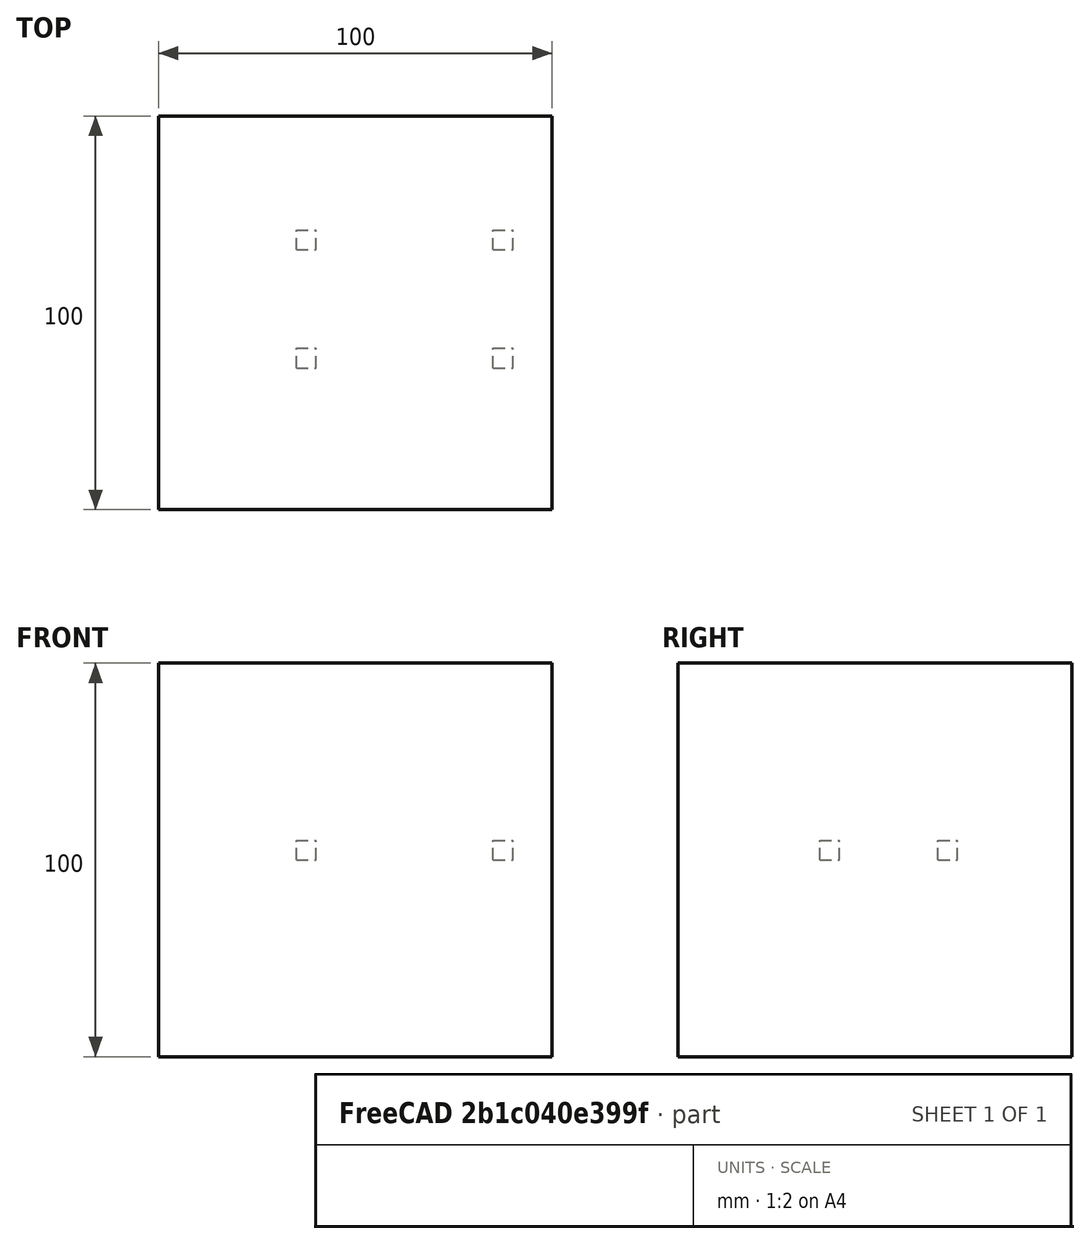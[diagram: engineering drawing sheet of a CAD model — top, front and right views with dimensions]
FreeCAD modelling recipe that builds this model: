
FCSTD DOCUMENT  (FreeCAD 0.19RUnknown)
Label: arrayTest-3
License: All rights reserved
LicenseURL: http://en.wikipedia.org/wiki/All_rights_reserved
objects: App::DocumentObjectGroupPython×1248, Part::FeaturePython×2, App::Part×2, Part::Box×1
note: 3 computed .brp shape members not serialized (recipe doc carries the construction recipe); baked Part::Feature solids carry a one-line shape summary decoded from their .brp

FEATURE [App::DocumentObjectGroupPython] HALFPI  # scripted group (container) (typed FeaturePython)
  name = HALFPI
  value = pi/2.
FEATURE [App::DocumentObjectGroupPython] PI  # scripted group (container) (typed FeaturePython)
  name = PI
  value = 1.*pi
FEATURE [App::DocumentObjectGroupPython] TWOPI  # scripted group (container) (typed FeaturePython)
  name = TWOPI
  value = 2.*pi
FEATURE [App::DocumentObjectGroupPython] Constants  # scripted group (container) (typed FeaturePython)
  Group = -> [HALFPI,PI,TWOPI]
FEATURE [App::DocumentObjectGroupPython] Variables  # scripted group (container) (typed FeaturePython)
FEATURE [App::DocumentObjectGroupPython] Quantities  # scripted group (container) (typed FeaturePython)
FEATURE [App::DocumentObjectGroupPython] Isotopes  # scripted group (container) (typed FeaturePython)
FEATURE [App::DocumentObjectGroupPython] Elements  # scripted group (container) (typed FeaturePython)
FEATURE [App::DocumentObjectGroupPython] G4Isotopes  # scripted group (container) (typed FeaturePython)
FEATURE [App::DocumentObjectGroupPython] H_element  # scripted group (container) (typed FeaturePython)
  Z = 1
  atom_value = 1.008
  formula = H
  name = H_element
FEATURE [App::DocumentObjectGroupPython] He_element  # scripted group (container) (typed FeaturePython)
  Z = 2
  atom_value = 4.0026
  formula = He
  name = He_element
FEATURE [App::DocumentObjectGroupPython] Li_element  # scripted group (container) (typed FeaturePython)
  Z = 3
  atom_value = 6.94
  formula = Li
  name = Li_element
FEATURE [App::DocumentObjectGroupPython] Be_element  # scripted group (container) (typed FeaturePython)
  Z = 4
  atom_value = 9.01218
  formula = Be
  name = Be_element
FEATURE [App::DocumentObjectGroupPython] B_element  # scripted group (container) (typed FeaturePython)
  Z = 5
  atom_value = 10.81
  formula = B
  name = B_element
FEATURE [App::DocumentObjectGroupPython] C_element  # scripted group (container) (typed FeaturePython)
  Z = 6
  atom_value = 12.011
  formula = C
  name = C_element
FEATURE [App::DocumentObjectGroupPython] N_element  # scripted group (container) (typed FeaturePython)
  Z = 7
  atom_value = 14.007
  formula = N
  name = N_element
FEATURE [App::DocumentObjectGroupPython] O_element  # scripted group (container) (typed FeaturePython)
  Z = 8
  atom_value = 15.999
  formula = O
  name = O_element
FEATURE [App::DocumentObjectGroupPython] F_element  # scripted group (container) (typed FeaturePython)
  Z = 9
  atom_value = 18.9984
  formula = F
  name = F_element
FEATURE [App::DocumentObjectGroupPython] Ne_element  # scripted group (container) (typed FeaturePython)
  Z = 10
  atom_value = 20.1797
  formula = Ne
  name = Ne_element
FEATURE [App::DocumentObjectGroupPython] Na_element  # scripted group (container) (typed FeaturePython)
  Z = 11
  atom_value = 22.9898
  formula = Na
  name = Na_element
FEATURE [App::DocumentObjectGroupPython] Mg_element  # scripted group (container) (typed FeaturePython)
  Z = 12
  atom_value = 24.305
  formula = Mg
  name = Mg_element
FEATURE [App::DocumentObjectGroupPython] Al_element  # scripted group (container) (typed FeaturePython)
  Z = 13
  atom_value = 26.9815
  formula = Al
  name = Al_element
FEATURE [App::DocumentObjectGroupPython] Si_element  # scripted group (container) (typed FeaturePython)
  Z = 14
  atom_value = 28.085
  formula = Si
  name = Si_element
FEATURE [App::DocumentObjectGroupPython] P_element  # scripted group (container) (typed FeaturePython)
  Z = 15
  atom_value = 30.9738
  formula = P
  name = P_element
FEATURE [App::DocumentObjectGroupPython] S_element  # scripted group (container) (typed FeaturePython)
  Z = 16
  atom_value = 32.06
  formula = S
  name = S_element
FEATURE [App::DocumentObjectGroupPython] Cl_element  # scripted group (container) (typed FeaturePython)
  Z = 17
  atom_value = 35.45
  formula = Cl
  name = Cl_element
FEATURE [App::DocumentObjectGroupPython] Ar_element  # scripted group (container) (typed FeaturePython)
  Z = 18
  atom_value = 39.95
  formula = Ar
  name = Ar_element
FEATURE [App::DocumentObjectGroupPython] K_element  # scripted group (container) (typed FeaturePython)
  Z = 19
  atom_value = 39.0983
  formula = K
  name = K_element
FEATURE [App::DocumentObjectGroupPython] Ca_element  # scripted group (container) (typed FeaturePython)
  Z = 20
  atom_value = 40.078
  formula = Ca
  name = Ca_element
FEATURE [App::DocumentObjectGroupPython] Sc_element  # scripted group (container) (typed FeaturePython)
  Z = 21
  atom_value = 44.9559
  formula = Sc
  name = Sc_element
FEATURE [App::DocumentObjectGroupPython] Ti_element  # scripted group (container) (typed FeaturePython)
  Z = 22
  atom_value = 47.867
  formula = Ti
  name = Ti_element
FEATURE [App::DocumentObjectGroupPython] V_element  # scripted group (container) (typed FeaturePython)
  Z = 23
  atom_value = 50.9415
  formula = V
  name = V_element
FEATURE [App::DocumentObjectGroupPython] Cr_element  # scripted group (container) (typed FeaturePython)
  Z = 24
  atom_value = 51.9961
  formula = Cr
  name = Cr_element
FEATURE [App::DocumentObjectGroupPython] Mn_element  # scripted group (container) (typed FeaturePython)
  Z = 25
  atom_value = 54.938
  formula = Mn
  name = Mn_element
FEATURE [App::DocumentObjectGroupPython] Fe_element  # scripted group (container) (typed FeaturePython)
  Z = 26
  atom_value = 55.845
  formula = Fe
  name = Fe_element
FEATURE [App::DocumentObjectGroupPython] Co_element  # scripted group (container) (typed FeaturePython)
  Z = 27
  atom_value = 58.9332
  formula = Co
  name = Co_element
FEATURE [App::DocumentObjectGroupPython] Ni_element  # scripted group (container) (typed FeaturePython)
  Z = 28
  atom_value = 58.6934
  formula = Ni
  name = Ni_element
FEATURE [App::DocumentObjectGroupPython] Cu_element  # scripted group (container) (typed FeaturePython)
  Z = 29
  atom_value = 63.546
  formula = Cu
  name = Cu_element
FEATURE [App::DocumentObjectGroupPython] Zn_element  # scripted group (container) (typed FeaturePython)
  Z = 30
  atom_value = 65.38
  formula = Zn
  name = Zn_element
FEATURE [App::DocumentObjectGroupPython] Ga_element  # scripted group (container) (typed FeaturePython)
  Z = 31
  atom_value = 69.723
  formula = Ga
  name = Ga_element
FEATURE [App::DocumentObjectGroupPython] Ge_element  # scripted group (container) (typed FeaturePython)
  Z = 32
  atom_value = 72.63
  formula = Ge
  name = Ge_element
FEATURE [App::DocumentObjectGroupPython] As_element  # scripted group (container) (typed FeaturePython)
  Z = 33
  atom_value = 74.9216
  formula = As
  name = As_element
FEATURE [App::DocumentObjectGroupPython] Se_element  # scripted group (container) (typed FeaturePython)
  Z = 34
  atom_value = 78.971
  formula = Se
  name = Se_element
FEATURE [App::DocumentObjectGroupPython] Br_element  # scripted group (container) (typed FeaturePython)
  Z = 35
  atom_value = 79.904
  formula = Br
  name = Br_element
FEATURE [App::DocumentObjectGroupPython] Kr_element  # scripted group (container) (typed FeaturePython)
  Z = 36
  atom_value = 83.798
  formula = Kr
  name = Kr_element
FEATURE [App::DocumentObjectGroupPython] Rb_element  # scripted group (container) (typed FeaturePython)
  Z = 37
  atom_value = 85.4678
  formula = Rb
  name = Rb_element
FEATURE [App::DocumentObjectGroupPython] Sr_element  # scripted group (container) (typed FeaturePython)
  Z = 38
  atom_value = 87.62
  formula = Sr
  name = Sr_element
FEATURE [App::DocumentObjectGroupPython] Y_element  # scripted group (container) (typed FeaturePython)
  Z = 39
  atom_value = 88.9058
  formula = Y
  name = Y_element
FEATURE [App::DocumentObjectGroupPython] Zr_element  # scripted group (container) (typed FeaturePython)
  Z = 40
  atom_value = 91.224
  formula = Zr
  name = Zr_element
FEATURE [App::DocumentObjectGroupPython] Nb_element  # scripted group (container) (typed FeaturePython)
  Z = 41
  atom_value = 92.9064
  formula = Nb
  name = Nb_element
FEATURE [App::DocumentObjectGroupPython] Mo_element  # scripted group (container) (typed FeaturePython)
  Z = 42
  atom_value = 95.95
  formula = Mo
  name = Mo_element
FEATURE [App::DocumentObjectGroupPython] Tc_element  # scripted group (container) (typed FeaturePython)
  Z = 43
  atom_value = 97
  formula = Tc
  name = Tc_element
FEATURE [App::DocumentObjectGroupPython] Ru_element  # scripted group (container) (typed FeaturePython)
  Z = 44
  atom_value = 101.07
  formula = Ru
  name = Ru_element
FEATURE [App::DocumentObjectGroupPython] Rh_element  # scripted group (container) (typed FeaturePython)
  Z = 45
  atom_value = 102.905
  formula = Rh
  name = Rh_element
FEATURE [App::DocumentObjectGroupPython] Pd_element  # scripted group (container) (typed FeaturePython)
  Z = 46
  atom_value = 106.42
  formula = Pd
  name = Pd_element
FEATURE [App::DocumentObjectGroupPython] Ag_element  # scripted group (container) (typed FeaturePython)
  Z = 47
  atom_value = 107.868
  formula = Ag
  name = Ag_element
FEATURE [App::DocumentObjectGroupPython] Cd_element  # scripted group (container) (typed FeaturePython)
  Z = 48
  atom_value = 112.414
  formula = Cd
  name = Cd_element
FEATURE [App::DocumentObjectGroupPython] In_element  # scripted group (container) (typed FeaturePython)
  Z = 49
  atom_value = 114.818
  formula = In
  name = In_element
FEATURE [App::DocumentObjectGroupPython] Sn_element  # scripted group (container) (typed FeaturePython)
  Z = 50
  atom_value = 118.71
  formula = Sn
  name = Sn_element
FEATURE [App::DocumentObjectGroupPython] Sb_element  # scripted group (container) (typed FeaturePython)
  Z = 51
  atom_value = 121.76
  formula = Sb
  name = Sb_element
FEATURE [App::DocumentObjectGroupPython] Te_element  # scripted group (container) (typed FeaturePython)
  Z = 52
  atom_value = 127.6
  formula = Te
  name = Te_element
FEATURE [App::DocumentObjectGroupPython] I_element  # scripted group (container) (typed FeaturePython)
  Z = 53
  atom_value = 126.904
  formula = I
  name = I_element
FEATURE [App::DocumentObjectGroupPython] Xe_element  # scripted group (container) (typed FeaturePython)
  Z = 54
  atom_value = 131.293
  formula = Xe
  name = Xe_element
FEATURE [App::DocumentObjectGroupPython] Cs_element  # scripted group (container) (typed FeaturePython)
  Z = 55
  atom_value = 132.905
  formula = Cs
  name = Cs_element
FEATURE [App::DocumentObjectGroupPython] Ba_element  # scripted group (container) (typed FeaturePython)
  Z = 56
  atom_value = 137.327
  formula = Ba
  name = Ba_element
FEATURE [App::DocumentObjectGroupPython] La_element  # scripted group (container) (typed FeaturePython)
  Z = 57
  atom_value = 138.905
  formula = La
  name = La_element
FEATURE [App::DocumentObjectGroupPython] Ce_element  # scripted group (container) (typed FeaturePython)
  Z = 58
  atom_value = 140.116
  formula = Ce
  name = Ce_element
FEATURE [App::DocumentObjectGroupPython] Pr_element  # scripted group (container) (typed FeaturePython)
  Z = 59
  atom_value = 140.908
  formula = Pr
  name = Pr_element
FEATURE [App::DocumentObjectGroupPython] Nd_element  # scripted group (container) (typed FeaturePython)
  Z = 60
  atom_value = 144.242
  formula = Nd
  name = Nd_element
FEATURE [App::DocumentObjectGroupPython] Pm_element  # scripted group (container) (typed FeaturePython)
  Z = 61
  atom_value = 145
  formula = Pm
  name = Pm_element
FEATURE [App::DocumentObjectGroupPython] Sm_element  # scripted group (container) (typed FeaturePython)
  Z = 62
  atom_value = 150.36
  formula = Sm
  name = Sm_element
FEATURE [App::DocumentObjectGroupPython] Eu_element  # scripted group (container) (typed FeaturePython)
  Z = 63
  atom_value = 151.964
  formula = Eu
  name = Eu_element
FEATURE [App::DocumentObjectGroupPython] Gd_element  # scripted group (container) (typed FeaturePython)
  Z = 64
  atom_value = 157.25
  formula = Gd
  name = Gd_element
FEATURE [App::DocumentObjectGroupPython] Tb_element  # scripted group (container) (typed FeaturePython)
  Z = 65
  atom_value = 158.925
  formula = Tb
  name = Tb_element
FEATURE [App::DocumentObjectGroupPython] Dy_element  # scripted group (container) (typed FeaturePython)
  Z = 66
  atom_value = 162.5
  formula = Dy
  name = Dy_element
FEATURE [App::DocumentObjectGroupPython] Ho_element  # scripted group (container) (typed FeaturePython)
  Z = 67
  atom_value = 164.93
  formula = Ho
  name = Ho_element
FEATURE [App::DocumentObjectGroupPython] Er_element  # scripted group (container) (typed FeaturePython)
  Z = 68
  atom_value = 167.259
  formula = Er
  name = Er_element
FEATURE [App::DocumentObjectGroupPython] Tm_element  # scripted group (container) (typed FeaturePython)
  Z = 69
  atom_value = 168.934
  formula = Tm
  name = Tm_element
FEATURE [App::DocumentObjectGroupPython] Yb_element  # scripted group (container) (typed FeaturePython)
  Z = 70
  atom_value = 173.045
  formula = Yb
  name = Yb_element
FEATURE [App::DocumentObjectGroupPython] Lu_element  # scripted group (container) (typed FeaturePython)
  Z = 71
  atom_value = 174.967
  formula = Lu
  name = Lu_element
FEATURE [App::DocumentObjectGroupPython] Hf_element  # scripted group (container) (typed FeaturePython)
  Z = 72
  atom_value = 178.49
  formula = Hf
  name = Hf_element
FEATURE [App::DocumentObjectGroupPython] Ta_element  # scripted group (container) (typed FeaturePython)
  Z = 73
  atom_value = 180.948
  formula = Ta
  name = Ta_element
FEATURE [App::DocumentObjectGroupPython] W_element  # scripted group (container) (typed FeaturePython)
  Z = 74
  atom_value = 183.84
  formula = W
  name = W_element
FEATURE [App::DocumentObjectGroupPython] Re_element  # scripted group (container) (typed FeaturePython)
  Z = 75
  atom_value = 186.207
  formula = Re
  name = Re_element
FEATURE [App::DocumentObjectGroupPython] Os_element  # scripted group (container) (typed FeaturePython)
  Z = 76
  atom_value = 190.23
  formula = Os
  name = Os_element
FEATURE [App::DocumentObjectGroupPython] Ir_element  # scripted group (container) (typed FeaturePython)
  Z = 77
  atom_value = 192.217
  formula = Ir
  name = Ir_element
FEATURE [App::DocumentObjectGroupPython] Pt_element  # scripted group (container) (typed FeaturePython)
  Z = 78
  atom_value = 195.084
  formula = Pt
  name = Pt_element
FEATURE [App::DocumentObjectGroupPython] Au_element  # scripted group (container) (typed FeaturePython)
  Z = 79
  atom_value = 196.967
  formula = Au
  name = Au_element
FEATURE [App::DocumentObjectGroupPython] Hg_element  # scripted group (container) (typed FeaturePython)
  Z = 80
  atom_value = 200.592
  formula = Hg
  name = Hg_element
FEATURE [App::DocumentObjectGroupPython] Tl_element  # scripted group (container) (typed FeaturePython)
  Z = 81
  atom_value = 204.38
  formula = Tl
  name = Tl_element
FEATURE [App::DocumentObjectGroupPython] Pb_element  # scripted group (container) (typed FeaturePython)
  Z = 82
  atom_value = 207.2
  formula = Pb
  name = Pb_element
FEATURE [App::DocumentObjectGroupPython] Bi_element  # scripted group (container) (typed FeaturePython)
  Z = 83
  atom_value = 208.98
  formula = Bi
  name = Bi_element
FEATURE [App::DocumentObjectGroupPython] Po_element  # scripted group (container) (typed FeaturePython)
  Z = 84
  atom_value = 209
  formula = Po
  name = Po_element
FEATURE [App::DocumentObjectGroupPython] At_element  # scripted group (container) (typed FeaturePython)
  Z = 85
  atom_value = 210
  formula = At
  name = At_element
FEATURE [App::DocumentObjectGroupPython] Rn_element  # scripted group (container) (typed FeaturePython)
  Z = 86
  atom_value = 222
  formula = Rn
  name = Rn_element
FEATURE [App::DocumentObjectGroupPython] Fr_element  # scripted group (container) (typed FeaturePython)
  Z = 87
  atom_value = 223
  formula = Fr
  name = Fr_element
FEATURE [App::DocumentObjectGroupPython] Ra_element  # scripted group (container) (typed FeaturePython)
  Z = 88
  atom_value = 226
  formula = Ra
  name = Ra_element
FEATURE [App::DocumentObjectGroupPython] Ac_element  # scripted group (container) (typed FeaturePython)
  Z = 89
  atom_value = 227
  formula = Ac
  name = Ac_element
FEATURE [App::DocumentObjectGroupPython] Th_element  # scripted group (container) (typed FeaturePython)
  Z = 90
  atom_value = 232.038
  formula = Th
  name = Th_element
FEATURE [App::DocumentObjectGroupPython] Pa_element  # scripted group (container) (typed FeaturePython)
  Z = 91
  atom_value = 231.036
  formula = Pa
  name = Pa_element
FEATURE [App::DocumentObjectGroupPython] U_element  # scripted group (container) (typed FeaturePython)
  Z = 92
  atom_value = 238.029
  formula = U
  name = U_element
FEATURE [App::DocumentObjectGroupPython] Np_element  # scripted group (container) (typed FeaturePython)
  Z = 93
  atom_value = 237
  formula = Np
  name = Np_element
FEATURE [App::DocumentObjectGroupPython] Pu_element  # scripted group (container) (typed FeaturePython)
  Z = 94
  atom_value = 244
  formula = Pu
  name = Pu_element
FEATURE [App::DocumentObjectGroupPython] Am_element  # scripted group (container) (typed FeaturePython)
  Z = 95
  atom_value = 243
  formula = Am
  name = Am_element
FEATURE [App::DocumentObjectGroupPython] Cm_element  # scripted group (container) (typed FeaturePython)
  Z = 96
  atom_value = 247
  formula = Cm
  name = Cm_element
FEATURE [App::DocumentObjectGroupPython] Bk_element  # scripted group (container) (typed FeaturePython)
  Z = 97
  atom_value = 247
  formula = Bk
  name = Bk_element
FEATURE [App::DocumentObjectGroupPython] Cf_element  # scripted group (container) (typed FeaturePython)
  Z = 98
  atom_value = 251
  formula = Cf
  name = Cf_element
FEATURE [App::DocumentObjectGroupPython] G4Elements  # scripted group (container) (typed FeaturePython)
  Group = -> [H_element,He_element,Li_element,Be_element,B_element,C_element,N_element,O_element,F_element,Ne_element,Na_element,Mg_element,Al_element,Si_element,P_element,S_element,Cl_element,Ar_element,K_element,Ca_element,Sc_element,Ti_element,V_element,Cr_element,Mn_element,Fe_element,Co_element,Ni_element,Cu_element,Zn_element,Ga_element,Ge_element,As_element,Se_element,Br_element,Kr_element,Rb_element,+61 more]
FEATURE [App::DocumentObjectGroupPython] H_element001  label="H_element : 0.101"  # scripted group (container) (typed FeaturePython)
  n = 0.101327
FEATURE [App::DocumentObjectGroupPython] C_element001  label="C_element : 0.775"  # scripted group (container) (typed FeaturePython)
  n = 0.7755
FEATURE [App::DocumentObjectGroupPython] N_element001  label="N_element : 0.035"  # scripted group (container) (typed FeaturePython)
  n = 0.035057
FEATURE [App::DocumentObjectGroupPython] O_element001  label="O_element : 0.052"  # scripted group (container) (typed FeaturePython)
  n = 0.0523159
FEATURE [App::DocumentObjectGroupPython] F_element001  label="F_element : 0.017"  # scripted group (container) (typed FeaturePython)
  n = 0.017422
FEATURE [App::DocumentObjectGroupPython] Ca_element001  label="Ca_element : 0.018"  # scripted group (container) (typed FeaturePython)
  n = 0.018378
FEATURE [App::DocumentObjectGroupPython] G4_A_150_TISSUE  label="G4_A-150_TISSUE"  # scripted group (container) (typed FeaturePython)
  Dunit = g/cm3
  Dvalue = 1.127
  Group = -> [H_element001,C_element001,N_element001,O_element001,F_element001,Ca_element001]
  conduct = 2
  density = 1
  expand = 3
  formula = G4_A-150_TISSUE
  name = G4_A-150_TISSUE
  specific = 4
FEATURE [App::DocumentObjectGroupPython] C_element002  label="C_element : 3"  # scripted group (container) (typed FeaturePython)
  n = 3
  ref = C_element
FEATURE [App::DocumentObjectGroupPython] H_element002  label="H_element : 6"  # scripted group (container) (typed FeaturePython)
  n = 6
  ref = H_element
FEATURE [App::DocumentObjectGroupPython] O_element002  label="O_element : 1"  # scripted group (container) (typed FeaturePython)
  n = 1
  ref = O_element
FEATURE [App::DocumentObjectGroupPython] G4_ACETONE  # scripted group (container) (typed FeaturePython)
  Dunit = g/cm3
  Dvalue = 0.7899
  Group = -> [C_element002,H_element002,O_element002]
  conduct = 2
  density = 1
  expand = 3
  formula = G4_ACETONE
  name = G4_ACETONE
  specific = 4
FEATURE [App::DocumentObjectGroupPython] C_element003  label="C_element : 2"  # scripted group (container) (typed FeaturePython)
  n = 2
  ref = C_element
FEATURE [App::DocumentObjectGroupPython] H_element003  label="H_element : 2"  # scripted group (container) (typed FeaturePython)
  n = 2
  ref = H_element
FEATURE [App::DocumentObjectGroupPython] G4_ACETYLENE  # scripted group (container) (typed FeaturePython)
  Dunit = g/cm3
  Dvalue = 0.0010967
  Group = -> [C_element003,H_element003]
  conduct = 2
  density = 1
  expand = 3
  formula = G4_ACETYLENE
  name = G4_ACETYLENE
  specific = 4
FEATURE [App::DocumentObjectGroupPython] C_element004  label="C_element : 5"  # scripted group (container) (typed FeaturePython)
  n = 5
  ref = C_element
FEATURE [App::DocumentObjectGroupPython] H_element004  label="H_element : 5"  # scripted group (container) (typed FeaturePython)
  n = 5
  ref = H_element
FEATURE [App::DocumentObjectGroupPython] N_element002  label="N_element : 5"  # scripted group (container) (typed FeaturePython)
  n = 5
  ref = N_element
FEATURE [App::DocumentObjectGroupPython] G4_ADENINE  # scripted group (container) (typed FeaturePython)
  Dunit = g/cm3
  Dvalue = 1.6
  Group = -> [C_element004,H_element004,N_element002]
  conduct = 2
  density = 1
  expand = 3
  formula = G4_ADENINE
  name = G4_ADENINE
  specific = 4
FEATURE [App::DocumentObjectGroupPython] H_element005  label="H_element : 0.114"  # scripted group (container) (typed FeaturePython)
  n = 0.114
FEATURE [App::DocumentObjectGroupPython] C_element005  label="C_element : 0.598"  # scripted group (container) (typed FeaturePython)
  n = 0.598
FEATURE [App::DocumentObjectGroupPython] N_element003  label="N_element : 0.007"  # scripted group (container) (typed FeaturePython)
  n = 0.007
FEATURE [App::DocumentObjectGroupPython] O_element003  label="O_element : 0.278"  # scripted group (container) (typed FeaturePython)
  n = 0.278
FEATURE [App::DocumentObjectGroupPython] Na_element001  label="Na_element : 0.001"  # scripted group (container) (typed FeaturePython)
  n = 0.001
FEATURE [App::DocumentObjectGroupPython] S_element001  label="S_element : 0.001"  # scripted group (container) (typed FeaturePython)
  n = 0.001
FEATURE [App::DocumentObjectGroupPython] Cl_element001  label="Cl_element : 0.001"  # scripted group (container) (typed FeaturePython)
  n = 0.001
FEATURE [App::DocumentObjectGroupPython] G4_ADIPOSE_TISSUE_ICRP  # scripted group (container) (typed FeaturePython)
  Dunit = g/cm3
  Dvalue = 0.95
  Group = -> [H_element005,C_element005,N_element003,O_element003,Na_element001,S_element001,Cl_element001]
  conduct = 2
  density = 1
  expand = 3
  formula = G4_ADIPOSE_TISSUE_ICRP
  name = G4_ADIPOSE_TISSUE_ICRP
  specific = 4
FEATURE [App::DocumentObjectGroupPython] C_element006  label="C_element : 0.000"  # scripted group (container) (typed FeaturePython)
  n = 0.000124
FEATURE [App::DocumentObjectGroupPython] N_element004  label="N_element : 0.755"  # scripted group (container) (typed FeaturePython)
  n = 0.755268
FEATURE [App::DocumentObjectGroupPython] O_element004  label="O_element : 0.232"  # scripted group (container) (typed FeaturePython)
  n = 0.231781
FEATURE [App::DocumentObjectGroupPython] Ar_element001  label="Ar_element : 0.013"  # scripted group (container) (typed FeaturePython)
  n = 0.012827
FEATURE [App::DocumentObjectGroupPython] G4_AIR  # scripted group (container) (typed FeaturePython)
  Dunit = g/cm3
  Dvalue = 0.00120479
  Group = -> [C_element006,N_element004,O_element004,Ar_element001]
  conduct = 2
  density = 1
  expand = 3
  formula = G4_AIR
  name = G4_AIR
  specific = 4
FEATURE [App::DocumentObjectGroupPython] C_element007  label="C_element : 006"  # scripted group (container) (typed FeaturePython)
  n = 3
  ref = C_element
FEATURE [App::DocumentObjectGroupPython] H_element006  label="H_element : 7"  # scripted group (container) (typed FeaturePython)
  n = 7
  ref = H_element
FEATURE [App::DocumentObjectGroupPython] N_element005  label="N_element : 1"  # scripted group (container) (typed FeaturePython)
  n = 1
  ref = N_element
FEATURE [App::DocumentObjectGroupPython] O_element005  label="O_element : 2"  # scripted group (container) (typed FeaturePython)
  n = 2
  ref = O_element
FEATURE [App::DocumentObjectGroupPython] G4_ALANINE  # scripted group (container) (typed FeaturePython)
  Dunit = g/cm3
  Dvalue = 1.42
  Group = -> [C_element007,H_element006,N_element005,O_element005]
  conduct = 2
  density = 1
  expand = 3
  formula = G4_ALANINE
  name = G4_ALANINE
  specific = 4
FEATURE [App::DocumentObjectGroupPython] Al_element001  label="Al_element : 2"  # scripted group (container) (typed FeaturePython)
  n = 2
  ref = Al_element
FEATURE [App::DocumentObjectGroupPython] O_element006  label="O_element : 3"  # scripted group (container) (typed FeaturePython)
  n = 3
  ref = O_element
FEATURE [App::DocumentObjectGroupPython] G4_ALUMINUM_OXIDE  # scripted group (container) (typed FeaturePython)
  Dunit = g/cm3
  Dvalue = 3.97
  Group = -> [Al_element001,O_element006]
  conduct = 2
  density = 1
  expand = 3
  formula = G4_ALUMINUM_OXIDE
  name = G4_ALUMINUM_OXIDE
  specific = 4
FEATURE [App::DocumentObjectGroupPython] H_element007  label="H_element : 0.106"  # scripted group (container) (typed FeaturePython)
  n = 0.10593
FEATURE [App::DocumentObjectGroupPython] C_element008  label="C_element : 0.789"  # scripted group (container) (typed FeaturePython)
  n = 0.788974
FEATURE [App::DocumentObjectGroupPython] O_element007  label="O_element : 0.105"  # scripted group (container) (typed FeaturePython)
  n = 0.105096
FEATURE [App::DocumentObjectGroupPython] G4_AMBER  # scripted group (container) (typed FeaturePython)
  Dunit = g/cm3
  Dvalue = 1.1
  Group = -> [H_element007,C_element008,O_element007]
  conduct = 2
  density = 1
  expand = 3
  formula = G4_AMBER
  name = G4_AMBER
  specific = 4
FEATURE [App::DocumentObjectGroupPython] N_element006  label="N_element : 006"  # scripted group (container) (typed FeaturePython)
  n = 1
  ref = N_element
FEATURE [App::DocumentObjectGroupPython] H_element008  label="H_element : 3"  # scripted group (container) (typed FeaturePython)
  n = 3
  ref = H_element
FEATURE [App::DocumentObjectGroupPython] G4_AMMONIA  # scripted group (container) (typed FeaturePython)
  Dunit = g/cm3
  Dvalue = 0.000826019
  Group = -> [N_element006,H_element008]
  conduct = 2
  density = 1
  expand = 3
  formula = G4_AMMONIA
  name = G4_AMMONIA
  specific = 4
FEATURE [App::DocumentObjectGroupPython] C_element009  label="C_element : 6"  # scripted group (container) (typed FeaturePython)
  n = 6
  ref = C_element
FEATURE [App::DocumentObjectGroupPython] H_element009  label="H_element : 008"  # scripted group (container) (typed FeaturePython)
  n = 7
  ref = H_element
FEATURE [App::DocumentObjectGroupPython] N_element007  label="N_element : 007"  # scripted group (container) (typed FeaturePython)
  n = 1
  ref = N_element
FEATURE [App::DocumentObjectGroupPython] G4_ANILINE  # scripted group (container) (typed FeaturePython)
  Dunit = g/cm3
  Dvalue = 1.0235
  Group = -> [C_element009,H_element009,N_element007]
  conduct = 2
  density = 1
  expand = 3
  formula = G4_ANILINE
  name = G4_ANILINE
  specific = 4
FEATURE [App::DocumentObjectGroupPython] C_element010  label="C_element : 14"  # scripted group (container) (typed FeaturePython)
  n = 14
  ref = C_element
FEATURE [App::DocumentObjectGroupPython] H_element010  label="H_element : 10"  # scripted group (container) (typed FeaturePython)
  n = 10
  ref = H_element
FEATURE [App::DocumentObjectGroupPython] G4_ANTHRACENE  # scripted group (container) (typed FeaturePython)
  Dunit = g/cm3
  Dvalue = 1.283
  Group = -> [C_element010,H_element010]
  conduct = 2
  density = 1
  expand = 3
  formula = G4_ANTHRACENE
  name = G4_ANTHRACENE
  specific = 4
FEATURE [App::DocumentObjectGroupPython] H_element011  label="H_element : 0.065"  # scripted group (container) (typed FeaturePython)
  n = 0.0654709
FEATURE [App::DocumentObjectGroupPython] C_element011  label="C_element : 0.537"  # scripted group (container) (typed FeaturePython)
  n = 0.536944
FEATURE [App::DocumentObjectGroupPython] N_element008  label="N_element : 0.021"  # scripted group (container) (typed FeaturePython)
  n = 0.0215
FEATURE [App::DocumentObjectGroupPython] O_element008  label="O_element : 0.032"  # scripted group (container) (typed FeaturePython)
  n = 0.032085
FEATURE [App::DocumentObjectGroupPython] F_element002  label="F_element : 0.167"  # scripted group (container) (typed FeaturePython)
  n = 0.167411
FEATURE [App::DocumentObjectGroupPython] Ca_element002  label="Ca_element : 0.177"  # scripted group (container) (typed FeaturePython)
  n = 0.176589
FEATURE [App::DocumentObjectGroupPython] G4_B_100_BONE  label="G4_B-100_BONE"  # scripted group (container) (typed FeaturePython)
  Dunit = g/cm3
  Dvalue = 1.45
  Group = -> [H_element011,C_element011,N_element008,O_element008,F_element002,Ca_element002]
  conduct = 2
  density = 1
  expand = 3
  formula = G4_B-100_BONE
  name = G4_B-100_BONE
  specific = 4
FEATURE [App::DocumentObjectGroupPython] H_element012  label="H_element : 0.057"  # scripted group (container) (typed FeaturePython)
  n = 0.057441
FEATURE [App::DocumentObjectGroupPython] C_element012  label="C_element : 0.790"  # scripted group (container) (typed FeaturePython)
  n = 0.774591
FEATURE [App::DocumentObjectGroupPython] O_element009  label="O_element : 0.168"  # scripted group (container) (typed FeaturePython)
  n = 0.167968
FEATURE [App::DocumentObjectGroupPython] G4_BAKELITE  # scripted group (container) (typed FeaturePython)
  Dunit = g/cm3
  Dvalue = 1.25
  Group = -> [H_element012,C_element012,O_element009]
  conduct = 2
  density = 1
  expand = 3
  formula = G4_BAKELITE
  name = G4_BAKELITE
  specific = 4
FEATURE [App::DocumentObjectGroupPython] Ba_element001  label="Ba_element : 1"  # scripted group (container) (typed FeaturePython)
  n = 1
  ref = Ba_element
FEATURE [App::DocumentObjectGroupPython] F_element003  label="F_element : 2"  # scripted group (container) (typed FeaturePython)
  n = 2
  ref = F_element
FEATURE [App::DocumentObjectGroupPython] G4_BARIUM_FLUORIDE  # scripted group (container) (typed FeaturePython)
  Dunit = g/cm3
  Dvalue = 4.89
  Group = -> [Ba_element001,F_element003]
  conduct = 2
  density = 1
  expand = 3
  formula = G4_BARIUM_FLUORIDE
  name = G4_BARIUM_FLUORIDE
  specific = 4
FEATURE [App::DocumentObjectGroupPython] Ba_element002  label="Ba_element : 002"  # scripted group (container) (typed FeaturePython)
  n = 1
  ref = Ba_element
FEATURE [App::DocumentObjectGroupPython] S_element002  label="S_element : 1"  # scripted group (container) (typed FeaturePython)
  n = 1
  ref = S_element
FEATURE [App::DocumentObjectGroupPython] O_element010  label="O_element : 4"  # scripted group (container) (typed FeaturePython)
  n = 4
  ref = O_element
FEATURE [App::DocumentObjectGroupPython] G4_BARIUM_SULFATE  # scripted group (container) (typed FeaturePython)
  Dunit = g/cm3
  Dvalue = 4.5
  Group = -> [Ba_element002,S_element002,O_element010]
  conduct = 2
  density = 1
  expand = 3
  formula = G4_BARIUM_SULFATE
  name = G4_BARIUM_SULFATE
  specific = 4
FEATURE [App::DocumentObjectGroupPython] C_element013  label="C_element : 007"  # scripted group (container) (typed FeaturePython)
  n = 6
  ref = C_element
FEATURE [App::DocumentObjectGroupPython] H_element013  label="H_element : 009"  # scripted group (container) (typed FeaturePython)
  n = 6
  ref = H_element
FEATURE [App::DocumentObjectGroupPython] G4_BENZENE  # scripted group (container) (typed FeaturePython)
  Dunit = g/cm3
  Dvalue = 0.87865
  Group = -> [C_element013,H_element013]
  conduct = 2
  density = 1
  expand = 3
  formula = G4_BENZENE
  name = G4_BENZENE
  specific = 4
FEATURE [App::DocumentObjectGroupPython] Be_element001  label="Be_element : 1"  # scripted group (container) (typed FeaturePython)
  n = 1
  ref = Be_element
FEATURE [App::DocumentObjectGroupPython] O_element011  label="O_element : 005"  # scripted group (container) (typed FeaturePython)
  n = 1
  ref = O_element
FEATURE [App::DocumentObjectGroupPython] G4_BERYLLIUM_OXIDE  # scripted group (container) (typed FeaturePython)
  Dunit = g/cm3
  Dvalue = 3.01
  Group = -> [Be_element001,O_element011]
  conduct = 2
  density = 1
  expand = 3
  formula = G4_BERYLLIUM_OXIDE
  name = G4_BERYLLIUM_OXIDE
  specific = 4
FEATURE [App::DocumentObjectGroupPython] Bi_element001  label="Bi_element : 4"  # scripted group (container) (typed FeaturePython)
  n = 4
  ref = Bi_element
FEATURE [App::DocumentObjectGroupPython] Ge_element001  label="Ge_element : 3"  # scripted group (container) (typed FeaturePython)
  n = 3
  ref = Ge_element
FEATURE [App::DocumentObjectGroupPython] O_element012  label="O_element : 12"  # scripted group (container) (typed FeaturePython)
  n = 12
  ref = O_element
FEATURE [App::DocumentObjectGroupPython] G4_BGO  # scripted group (container) (typed FeaturePython)
  Dunit = g/cm3
  Dvalue = 7.13
  Group = -> [Bi_element001,Ge_element001,O_element012]
  conduct = 2
  density = 1
  expand = 3
  formula = G4_BGO
  name = G4_BGO
  specific = 4
FEATURE [App::DocumentObjectGroupPython] H_element014  label="H_element : 0.102"  # scripted group (container) (typed FeaturePython)
  n = 0.102
FEATURE [App::DocumentObjectGroupPython] C_element014  label="C_element : 0.110"  # scripted group (container) (typed FeaturePython)
  n = 0.11
FEATURE [App::DocumentObjectGroupPython] N_element009  label="N_element : 0.033"  # scripted group (container) (typed FeaturePython)
  n = 0.033
FEATURE [App::DocumentObjectGroupPython] O_element013  label="O_element : 0.745"  # scripted group (container) (typed FeaturePython)
  n = 0.745
FEATURE [App::DocumentObjectGroupPython] Na_element002  label="Na_element : 0.002"  # scripted group (container) (typed FeaturePython)
  n = 0.001
FEATURE [App::DocumentObjectGroupPython] P_element001  label="P_element : 0.001"  # scripted group (container) (typed FeaturePython)
  n = 0.001
FEATURE [App::DocumentObjectGroupPython] S_element003  label="S_element : 0.002"  # scripted group (container) (typed FeaturePython)
  n = 0.002
FEATURE [App::DocumentObjectGroupPython] Cl_element002  label="Cl_element : 0.003"  # scripted group (container) (typed FeaturePython)
  n = 0.003
FEATURE [App::DocumentObjectGroupPython] K_element001  label="K_element : 0.002"  # scripted group (container) (typed FeaturePython)
  n = 0.002
FEATURE [App::DocumentObjectGroupPython] Fe_element001  label="Fe_element : 0.001"  # scripted group (container) (typed FeaturePython)
  n = 0.001
FEATURE [App::DocumentObjectGroupPython] G4_BLOOD_ICRP  # scripted group (container) (typed FeaturePython)
  Dunit = g/cm3
  Dvalue = 1.06
  Group = -> [H_element014,C_element014,N_element009,O_element013,Na_element002,P_element001,S_element003,Cl_element002,K_element001,Fe_element001]
  conduct = 2
  density = 1
  expand = 3
  formula = G4_BLOOD_ICRP
  name = G4_BLOOD_ICRP
  specific = 4
FEATURE [App::DocumentObjectGroupPython] H_element015  label="H_element : 0.064"  # scripted group (container) (typed FeaturePython)
  n = 0.064
FEATURE [App::DocumentObjectGroupPython] C_element015  label="C_element : 0.278"  # scripted group (container) (typed FeaturePython)
  n = 0.278
FEATURE [App::DocumentObjectGroupPython] N_element010  label="N_element : 0.027"  # scripted group (container) (typed FeaturePython)
  n = 0.027
FEATURE [App::DocumentObjectGroupPython] O_element014  label="O_element : 0.410"  # scripted group (container) (typed FeaturePython)
  n = 0.41
FEATURE [App::DocumentObjectGroupPython] Mg_element001  label="Mg_element : 0.002"  # scripted group (container) (typed FeaturePython)
  n = 0.002
FEATURE [App::DocumentObjectGroupPython] P_element002  label="P_element : 0.070"  # scripted group (container) (typed FeaturePython)
  n = 0.07
FEATURE [App::DocumentObjectGroupPython] S_element004  label="S_element : 0.003"  # scripted group (container) (typed FeaturePython)
  n = 0.002
FEATURE [App::DocumentObjectGroupPython] Ca_element003  label="Ca_element : 0.147"  # scripted group (container) (typed FeaturePython)
  n = 0.147
FEATURE [App::DocumentObjectGroupPython] G4_BONE_COMPACT_ICRU  # scripted group (container) (typed FeaturePython)
  Dunit = g/cm3
  Dvalue = 1.85
  Group = -> [H_element015,C_element015,N_element010,O_element014,Mg_element001,P_element002,S_element004,Ca_element003]
  conduct = 2
  density = 1
  expand = 3
  formula = G4_BONE_COMPACT_ICRU
  name = G4_BONE_COMPACT_ICRU
  specific = 4
FEATURE [App::DocumentObjectGroupPython] H_element016  label="H_element : 0.034"  # scripted group (container) (typed FeaturePython)
  n = 0.034
FEATURE [App::DocumentObjectGroupPython] C_element016  label="C_element : 0.155"  # scripted group (container) (typed FeaturePython)
  n = 0.155
FEATURE [App::DocumentObjectGroupPython] N_element011  label="N_element : 0.042"  # scripted group (container) (typed FeaturePython)
  n = 0.042
FEATURE [App::DocumentObjectGroupPython] O_element015  label="O_element : 0.435"  # scripted group (container) (typed FeaturePython)
  n = 0.435
FEATURE [App::DocumentObjectGroupPython] Na_element003  label="Na_element : 0.003"  # scripted group (container) (typed FeaturePython)
  n = 0.001
FEATURE [App::DocumentObjectGroupPython] Mg_element002  label="Mg_element : 0.003"  # scripted group (container) (typed FeaturePython)
  n = 0.002
FEATURE [App::DocumentObjectGroupPython] P_element003  label="P_element : 0.103"  # scripted group (container) (typed FeaturePython)
  n = 0.103
FEATURE [App::DocumentObjectGroupPython] S_element005  label="S_element : 0.004"  # scripted group (container) (typed FeaturePython)
  n = 0.003
FEATURE [App::DocumentObjectGroupPython] Ca_element004  label="Ca_element : 0.225"  # scripted group (container) (typed FeaturePython)
  n = 0.225
FEATURE [App::DocumentObjectGroupPython] G4_BONE_CORTICAL_ICRP  # scripted group (container) (typed FeaturePython)
  Dunit = g/cm3
  Dvalue = 1.92
  Group = -> [H_element016,C_element016,N_element011,O_element015,Na_element003,Mg_element002,P_element003,S_element005,Ca_element004]
  conduct = 2
  density = 1
  expand = 3
  formula = G4_BONE_CORTICAL_ICRP
  name = G4_BONE_CORTICAL_ICRP
  specific = 4
FEATURE [App::DocumentObjectGroupPython] B_element001  label="B_element : 4"  # scripted group (container) (typed FeaturePython)
  n = 4
  ref = B_element
FEATURE [App::DocumentObjectGroupPython] C_element017  label="C_element : 1"  # scripted group (container) (typed FeaturePython)
  n = 1
  ref = C_element
FEATURE [App::DocumentObjectGroupPython] G4_BORON_CARBIDE  # scripted group (container) (typed FeaturePython)
  Dunit = g/cm3
  Dvalue = 2.52
  Group = -> [B_element001,C_element017]
  conduct = 2
  density = 1
  expand = 3
  formula = G4_BORON_CARBIDE
  name = G4_BORON_CARBIDE
  specific = 4
FEATURE [App::DocumentObjectGroupPython] B_element002  label="B_element : 2"  # scripted group (container) (typed FeaturePython)
  n = 2
  ref = B_element
FEATURE [App::DocumentObjectGroupPython] O_element016  label="O_element : 006"  # scripted group (container) (typed FeaturePython)
  n = 3
  ref = O_element
FEATURE [App::DocumentObjectGroupPython] G4_BORON_OXIDE  # scripted group (container) (typed FeaturePython)
  Dunit = g/cm3
  Dvalue = 1.812
  Group = -> [B_element002,O_element016]
  conduct = 2
  density = 1
  expand = 3
  formula = G4_BORON_OXIDE
  name = G4_BORON_OXIDE
  specific = 4
FEATURE [App::DocumentObjectGroupPython] H_element017  label="H_element : 0.107"  # scripted group (container) (typed FeaturePython)
  n = 0.107
FEATURE [App::DocumentObjectGroupPython] C_element018  label="C_element : 0.145"  # scripted group (container) (typed FeaturePython)
  n = 0.145
FEATURE [App::DocumentObjectGroupPython] N_element012  label="N_element : 0.022"  # scripted group (container) (typed FeaturePython)
  n = 0.022
FEATURE [App::DocumentObjectGroupPython] O_element017  label="O_element : 0.712"  # scripted group (container) (typed FeaturePython)
  n = 0.712
FEATURE [App::DocumentObjectGroupPython] Na_element004  label="Na_element : 0.004"  # scripted group (container) (typed FeaturePython)
  n = 0.002
FEATURE [App::DocumentObjectGroupPython] P_element004  label="P_element : 0.004"  # scripted group (container) (typed FeaturePython)
  n = 0.004
FEATURE [App::DocumentObjectGroupPython] S_element006  label="S_element : 0.005"  # scripted group (container) (typed FeaturePython)
  n = 0.002
FEATURE [App::DocumentObjectGroupPython] Cl_element003  label="Cl_element : 0.004"  # scripted group (container) (typed FeaturePython)
  n = 0.003
FEATURE [App::DocumentObjectGroupPython] K_element002  label="K_element : 0.003"  # scripted group (container) (typed FeaturePython)
  n = 0.003
FEATURE [App::DocumentObjectGroupPython] G4_BRAIN_ICRP  # scripted group (container) (typed FeaturePython)
  Dunit = g/cm3
  Dvalue = 1.04
  Group = -> [H_element017,C_element018,N_element012,O_element017,Na_element004,P_element004,S_element006,Cl_element003,K_element002]
  conduct = 2
  density = 1
  expand = 3
  formula = G4_BRAIN_ICRP
  name = G4_BRAIN_ICRP
  specific = 4
FEATURE [App::DocumentObjectGroupPython] C_element019  label="C_element : 4"  # scripted group (container) (typed FeaturePython)
  n = 4
  ref = C_element
FEATURE [App::DocumentObjectGroupPython] H_element018  label="H_element : 010"  # scripted group (container) (typed FeaturePython)
  n = 10
  ref = H_element
FEATURE [App::DocumentObjectGroupPython] G4_BUTANE  # scripted group (container) (typed FeaturePython)
  Dunit = g/cm3
  Dvalue = 0.00249343
  Group = -> [C_element019,H_element018]
  conduct = 2
  density = 1
  expand = 3
  formula = G4_BUTANE
  name = G4_BUTANE
  specific = 4
FEATURE [App::DocumentObjectGroupPython] C_element020  label="C_element : 008"  # scripted group (container) (typed FeaturePython)
  n = 4
  ref = C_element
FEATURE [App::DocumentObjectGroupPython] H_element019  label="H_element : 011"  # scripted group (container) (typed FeaturePython)
  n = 10
  ref = H_element
FEATURE [App::DocumentObjectGroupPython] O_element018  label="O_element : 007"  # scripted group (container) (typed FeaturePython)
  n = 1
  ref = O_element
FEATURE [App::DocumentObjectGroupPython] G4_N_BUTYL_ALCOHOL  label="G4_N-BUTYL_ALCOHOL"  # scripted group (container) (typed FeaturePython)
  Dunit = g/cm3
  Dvalue = 0.8098
  Group = -> [C_element020,H_element019,O_element018]
  conduct = 2
  density = 1
  expand = 3
  formula = G4_N-BUTYL_ALCOHOL
  name = G4_N-BUTYL_ALCOHOL
  specific = 4
FEATURE [App::DocumentObjectGroupPython] H_element020  label="H_element : 0.025"  # scripted group (container) (typed FeaturePython)
  n = 0.02468
FEATURE [App::DocumentObjectGroupPython] C_element021  label="C_element : 0.502"  # scripted group (container) (typed FeaturePython)
  n = 0.501611
FEATURE [App::DocumentObjectGroupPython] O_element019  label="O_element : 0.005"  # scripted group (container) (typed FeaturePython)
  n = 0.004527
FEATURE [App::DocumentObjectGroupPython] F_element004  label="F_element : 0.465"  # scripted group (container) (typed FeaturePython)
  n = 0.465209
FEATURE [App::DocumentObjectGroupPython] Si_element001  label="Si_element : 0.004"  # scripted group (container) (typed FeaturePython)
  n = 0.003973
FEATURE [App::DocumentObjectGroupPython] G4_C_552  label="G4_C-552"  # scripted group (container) (typed FeaturePython)
  Dunit = g/cm3
  Dvalue = 1.76
  Group = -> [H_element020,C_element021,O_element019,F_element004,Si_element001]
  conduct = 2
  density = 1
  expand = 3
  formula = G4_C-552
  name = G4_C-552
  specific = 4
FEATURE [App::DocumentObjectGroupPython] Cd_element001  label="Cd_element : 1"  # scripted group (container) (typed FeaturePython)
  n = 1
  ref = Cd_element
FEATURE [App::DocumentObjectGroupPython] Te_element001  label="Te_element : 1"  # scripted group (container) (typed FeaturePython)
  n = 1
  ref = Te_element
FEATURE [App::DocumentObjectGroupPython] G4_CADMIUM_TELLURIDE  # scripted group (container) (typed FeaturePython)
  Dunit = g/cm3
  Dvalue = 6.2
  Group = -> [Cd_element001,Te_element001]
  conduct = 2
  density = 1
  expand = 3
  formula = G4_CADMIUM_TELLURIDE
  name = G4_CADMIUM_TELLURIDE
  specific = 4
FEATURE [App::DocumentObjectGroupPython] Cd_element002  label="Cd_element : 002"  # scripted group (container) (typed FeaturePython)
  n = 1
  ref = Cd_element
FEATURE [App::DocumentObjectGroupPython] W_element001  label="W_element : 1"  # scripted group (container) (typed FeaturePython)
  n = 1
  ref = W_element
FEATURE [App::DocumentObjectGroupPython] O_element020  label="O_element : 008"  # scripted group (container) (typed FeaturePython)
  n = 4
  ref = O_element
FEATURE [App::DocumentObjectGroupPython] G4_CADMIUM_TUNGSTATE  # scripted group (container) (typed FeaturePython)
  Dunit = g/cm3
  Dvalue = 7.9
  Group = -> [Cd_element002,W_element001,O_element020]
  conduct = 2
  density = 1
  expand = 3
  formula = G4_CADMIUM_TUNGSTATE
  name = G4_CADMIUM_TUNGSTATE
  specific = 4
FEATURE [App::DocumentObjectGroupPython] Ca_element005  label="Ca_element : 1"  # scripted group (container) (typed FeaturePython)
  n = 1
  ref = Ca_element
FEATURE [App::DocumentObjectGroupPython] C_element022  label="C_element : 009"  # scripted group (container) (typed FeaturePython)
  n = 1
  ref = C_element
FEATURE [App::DocumentObjectGroupPython] O_element021  label="O_element : 009"  # scripted group (container) (typed FeaturePython)
  n = 3
  ref = O_element
FEATURE [App::DocumentObjectGroupPython] G4_CALCIUM_CARBONATE  # scripted group (container) (typed FeaturePython)
  Dunit = g/cm3
  Dvalue = 2.8
  Group = -> [Ca_element005,C_element022,O_element021]
  conduct = 2
  density = 1
  expand = 3
  formula = G4_CALCIUM_CARBONATE
  name = G4_CALCIUM_CARBONATE
  specific = 4
FEATURE [App::DocumentObjectGroupPython] Ca_element006  label="Ca_element : 002"  # scripted group (container) (typed FeaturePython)
  n = 1
  ref = Ca_element
FEATURE [App::DocumentObjectGroupPython] F_element005  label="F_element : 003"  # scripted group (container) (typed FeaturePython)
  n = 2
  ref = F_element
FEATURE [App::DocumentObjectGroupPython] G4_CALCIUM_FLUORIDE  # scripted group (container) (typed FeaturePython)
  Dunit = g/cm3
  Dvalue = 3.18
  Group = -> [Ca_element006,F_element005]
  conduct = 2
  density = 1
  expand = 3
  formula = G4_CALCIUM_FLUORIDE
  name = G4_CALCIUM_FLUORIDE
  specific = 4
FEATURE [App::DocumentObjectGroupPython] Ca_element007  label="Ca_element : 003"  # scripted group (container) (typed FeaturePython)
  n = 1
  ref = Ca_element
FEATURE [App::DocumentObjectGroupPython] O_element022  label="O_element : 010"  # scripted group (container) (typed FeaturePython)
  n = 1
  ref = O_element
FEATURE [App::DocumentObjectGroupPython] G4_CALCIUM_OXIDE  # scripted group (container) (typed FeaturePython)
  Dunit = g/cm3
  Dvalue = 3.3
  Group = -> [Ca_element007,O_element022]
  conduct = 2
  density = 1
  expand = 3
  formula = G4_CALCIUM_OXIDE
  name = G4_CALCIUM_OXIDE
  specific = 4
FEATURE [App::DocumentObjectGroupPython] Ca_element008  label="Ca_element : 004"  # scripted group (container) (typed FeaturePython)
  n = 1
  ref = Ca_element
FEATURE [App::DocumentObjectGroupPython] S_element007  label="S_element : 002"  # scripted group (container) (typed FeaturePython)
  n = 1
  ref = S_element
FEATURE [App::DocumentObjectGroupPython] O_element023  label="O_element : 011"  # scripted group (container) (typed FeaturePython)
  n = 4
  ref = O_element
FEATURE [App::DocumentObjectGroupPython] G4_CALCIUM_SULFATE  # scripted group (container) (typed FeaturePython)
  Dunit = g/cm3
  Dvalue = 2.96
  Group = -> [Ca_element008,S_element007,O_element023]
  conduct = 2
  density = 1
  expand = 3
  formula = G4_CALCIUM_SULFATE
  name = G4_CALCIUM_SULFATE
  specific = 4
FEATURE [App::DocumentObjectGroupPython] Ca_element009  label="Ca_element : 005"  # scripted group (container) (typed FeaturePython)
  n = 1
  ref = Ca_element
FEATURE [App::DocumentObjectGroupPython] W_element002  label="W_element : 002"  # scripted group (container) (typed FeaturePython)
  n = 1
  ref = W_element
FEATURE [App::DocumentObjectGroupPython] O_element024  label="O_element : 012"  # scripted group (container) (typed FeaturePython)
  n = 4
  ref = O_element
FEATURE [App::DocumentObjectGroupPython] G4_CALCIUM_TUNGSTATE  # scripted group (container) (typed FeaturePython)
  Dunit = g/cm3
  Dvalue = 6.062
  Group = -> [Ca_element009,W_element002,O_element024]
  conduct = 2
  density = 1
  expand = 3
  formula = G4_CALCIUM_TUNGSTATE
  name = G4_CALCIUM_TUNGSTATE
  specific = 4
FEATURE [App::DocumentObjectGroupPython] C_element023  label="C_element : 010"  # scripted group (container) (typed FeaturePython)
  n = 1
  ref = C_element
FEATURE [App::DocumentObjectGroupPython] O_element025  label="O_element : 013"  # scripted group (container) (typed FeaturePython)
  n = 2
  ref = O_element
FEATURE [App::DocumentObjectGroupPython] G4_CARBON_DIOXIDE  # scripted group (container) (typed FeaturePython)
  Dunit = g/cm3
  Dvalue = 0.00184212
  Group = -> [C_element023,O_element025]
  conduct = 2
  density = 1
  expand = 3
  formula = G4_CARBON_DIOXIDE
  name = G4_CARBON_DIOXIDE
  specific = 4
FEATURE [App::DocumentObjectGroupPython] C_element024  label="C_element : 011"  # scripted group (container) (typed FeaturePython)
  n = 1
  ref = C_element
FEATURE [App::DocumentObjectGroupPython] Cl_element004  label="Cl_element : 4"  # scripted group (container) (typed FeaturePython)
  n = 4
  ref = Cl_element
FEATURE [App::DocumentObjectGroupPython] G4_CARBON_TETRACHLORIDE  # scripted group (container) (typed FeaturePython)
  Dunit = g/cm3
  Dvalue = 1.594
  Group = -> [C_element024,Cl_element004]
  conduct = 2
  density = 1
  expand = 3
  formula = G4_CARBON_TETRACHLORIDE
  name = G4_CARBON_TETRACHLORIDE
  specific = 4
FEATURE [App::DocumentObjectGroupPython] C_element025  label="C_element : 012"  # scripted group (container) (typed FeaturePython)
  n = 6
  ref = C_element
FEATURE [App::DocumentObjectGroupPython] H_element021  label="H_element : 012"  # scripted group (container) (typed FeaturePython)
  n = 10
  ref = H_element
FEATURE [App::DocumentObjectGroupPython] O_element026  label="O_element : 5"  # scripted group (container) (typed FeaturePython)
  n = 5
  ref = O_element
FEATURE [App::DocumentObjectGroupPython] G4_CELLULOSE_CELLOPHANE  # scripted group (container) (typed FeaturePython)
  Dunit = g/cm3
  Dvalue = 1.42
  Group = -> [C_element025,H_element021,O_element026]
  conduct = 2
  density = 1
  expand = 3
  formula = G4_CELLULOSE_CELLOPHANE
  name = G4_CELLULOSE_CELLOPHANE
  specific = 4
FEATURE [App::DocumentObjectGroupPython] H_element022  label="H_element : 0.067"  # scripted group (container) (typed FeaturePython)
  n = 0.067125
FEATURE [App::DocumentObjectGroupPython] C_element026  label="C_element : 0.545"  # scripted group (container) (typed FeaturePython)
  n = 0.545403
FEATURE [App::DocumentObjectGroupPython] O_element027  label="O_element : 0.387"  # scripted group (container) (typed FeaturePython)
  n = 0.387472
FEATURE [App::DocumentObjectGroupPython] G4_CELLULOSE_BUTYRATE  # scripted group (container) (typed FeaturePython)
  Dunit = g/cm3
  Dvalue = 1.2
  Group = -> [H_element022,C_element026,O_element027]
  conduct = 2
  density = 1
  expand = 3
  formula = G4_CELLULOSE_BUTYRATE
  name = G4_CELLULOSE_BUTYRATE
  specific = 4
FEATURE [App::DocumentObjectGroupPython] H_element023  label="H_element : 0.029"  # scripted group (container) (typed FeaturePython)
  n = 0.029216
FEATURE [App::DocumentObjectGroupPython] C_element027  label="C_element : 0.271"  # scripted group (container) (typed FeaturePython)
  n = 0.271296
FEATURE [App::DocumentObjectGroupPython] N_element013  label="N_element : 0.121"  # scripted group (container) (typed FeaturePython)
  n = 0.121276
FEATURE [App::DocumentObjectGroupPython] O_element028  label="O_element : 0.578"  # scripted group (container) (typed FeaturePython)
  n = 0.578212
FEATURE [App::DocumentObjectGroupPython] G4_CELLULOSE_NITRATE  # scripted group (container) (typed FeaturePython)
  Dunit = g/cm3
  Dvalue = 1.49
  Group = -> [H_element023,C_element027,N_element013,O_element028]
  conduct = 2
  density = 1
  expand = 3
  formula = G4_CELLULOSE_NITRATE
  name = G4_CELLULOSE_NITRATE
  specific = 4
FEATURE [App::DocumentObjectGroupPython] H_element024  label="H_element : 0.108"  # scripted group (container) (typed FeaturePython)
  n = 0.107596
FEATURE [App::DocumentObjectGroupPython] N_element014  label="N_element : 0.001"  # scripted group (container) (typed FeaturePython)
  n = 0.0008
FEATURE [App::DocumentObjectGroupPython] O_element029  label="O_element : 0.875"  # scripted group (container) (typed FeaturePython)
  n = 0.874976
FEATURE [App::DocumentObjectGroupPython] S_element008  label="S_element : 0.015"  # scripted group (container) (typed FeaturePython)
  n = 0.014627
FEATURE [App::DocumentObjectGroupPython] Ce_element001  label="Ce_element : 0.002"  # scripted group (container) (typed FeaturePython)
  n = 0.002001
FEATURE [App::DocumentObjectGroupPython] G4_CERIC_SULFATE  # scripted group (container) (typed FeaturePython)
  Dunit = g/cm3
  Dvalue = 1.03
  Group = -> [H_element024,N_element014,O_element029,S_element008,Ce_element001]
  conduct = 2
  density = 1
  expand = 3
  formula = G4_CERIC_SULFATE
  name = G4_CERIC_SULFATE
  specific = 4
FEATURE [App::DocumentObjectGroupPython] Cs_element001  label="Cs_element : 1"  # scripted group (container) (typed FeaturePython)
  n = 1
  ref = Cs_element
FEATURE [App::DocumentObjectGroupPython] F_element006  label="F_element : 1"  # scripted group (container) (typed FeaturePython)
  n = 1
  ref = F_element
FEATURE [App::DocumentObjectGroupPython] G4_CESIUM_FLUORIDE  # scripted group (container) (typed FeaturePython)
  Dunit = g/cm3
  Dvalue = 4.115
  Group = -> [Cs_element001,F_element006]
  conduct = 2
  density = 1
  expand = 3
  formula = G4_CESIUM_FLUORIDE
  name = G4_CESIUM_FLUORIDE
  specific = 4
FEATURE [App::DocumentObjectGroupPython] Cs_element002  label="Cs_element : 002"  # scripted group (container) (typed FeaturePython)
  n = 1
  ref = Cs_element
FEATURE [App::DocumentObjectGroupPython] I_element001  label="I_element : 1"  # scripted group (container) (typed FeaturePython)
  n = 1
  ref = I_element
FEATURE [App::DocumentObjectGroupPython] G4_CESIUM_IODIDE  # scripted group (container) (typed FeaturePython)
  Dunit = g/cm3
  Dvalue = 4.51
  Group = -> [Cs_element002,I_element001]
  conduct = 2
  density = 1
  expand = 3
  formula = G4_CESIUM_IODIDE
  name = G4_CESIUM_IODIDE
  specific = 4
FEATURE [App::DocumentObjectGroupPython] C_element028  label="C_element : 013"  # scripted group (container) (typed FeaturePython)
  n = 6
  ref = C_element
FEATURE [App::DocumentObjectGroupPython] H_element025  label="H_element : 013"  # scripted group (container) (typed FeaturePython)
  n = 5
  ref = H_element
FEATURE [App::DocumentObjectGroupPython] Cl_element005  label="Cl_element : 1"  # scripted group (container) (typed FeaturePython)
  n = 1
  ref = Cl_element
FEATURE [App::DocumentObjectGroupPython] G4_CHLOROBENZENE  # scripted group (container) (typed FeaturePython)
  Dunit = g/cm3
  Dvalue = 1.1058
  Group = -> [C_element028,H_element025,Cl_element005]
  conduct = 2
  density = 1
  expand = 3
  formula = G4_CHLOROBENZENE
  name = G4_CHLOROBENZENE
  specific = 4
FEATURE [App::DocumentObjectGroupPython] C_element029  label="C_element : 014"  # scripted group (container) (typed FeaturePython)
  n = 1
  ref = C_element
FEATURE [App::DocumentObjectGroupPython] H_element026  label="H_element : 1"  # scripted group (container) (typed FeaturePython)
  n = 1
  ref = H_element
FEATURE [App::DocumentObjectGroupPython] Cl_element006  label="Cl_element : 3"  # scripted group (container) (typed FeaturePython)
  n = 3
  ref = Cl_element
FEATURE [App::DocumentObjectGroupPython] G4_CHLOROFORM  # scripted group (container) (typed FeaturePython)
  Dunit = g/cm3
  Dvalue = 1.4832
  Group = -> [C_element029,H_element026,Cl_element006]
  conduct = 2
  density = 1
  expand = 3
  formula = G4_CHLOROFORM
  name = G4_CHLOROFORM
  specific = 4
FEATURE [App::DocumentObjectGroupPython] H_element027  label="H_element : 0.010"  # scripted group (container) (typed FeaturePython)
  n = 0.01
FEATURE [App::DocumentObjectGroupPython] C_element030  label="C_element : 0.001"  # scripted group (container) (typed FeaturePython)
  n = 0.001
FEATURE [App::DocumentObjectGroupPython] O_element030  label="O_element : 0.529"  # scripted group (container) (typed FeaturePython)
  n = 0.529107
FEATURE [App::DocumentObjectGroupPython] Na_element005  label="Na_element : 0.016"  # scripted group (container) (typed FeaturePython)
  n = 0.016
FEATURE [App::DocumentObjectGroupPython] Mg_element003  label="Mg_element : 0.004"  # scripted group (container) (typed FeaturePython)
  n = 0.002
FEATURE [App::DocumentObjectGroupPython] Al_element002  label="Al_element : 0.034"  # scripted group (container) (typed FeaturePython)
  n = 0.033872
FEATURE [App::DocumentObjectGroupPython] Si_element002  label="Si_element : 0.337"  # scripted group (container) (typed FeaturePython)
  n = 0.337021
FEATURE [App::DocumentObjectGroupPython] K_element003  label="K_element : 0.013"  # scripted group (container) (typed FeaturePython)
  n = 0.013
FEATURE [App::DocumentObjectGroupPython] Ca_element010  label="Ca_element : 0.044"  # scripted group (container) (typed FeaturePython)
  n = 0.044
FEATURE [App::DocumentObjectGroupPython] Fe_element002  label="Fe_element : 0.014"  # scripted group (container) (typed FeaturePython)
  n = 0.014
FEATURE [App::DocumentObjectGroupPython] G4_CONCRETE  # scripted group (container) (typed FeaturePython)
  Dunit = g/cm3
  Dvalue = 2.3
  Group = -> [H_element027,C_element030,O_element030,Na_element005,Mg_element003,Al_element002,Si_element002,K_element003,Ca_element010,Fe_element002]
  conduct = 2
  density = 1
  expand = 3
  formula = G4_CONCRETE
  name = G4_CONCRETE
  specific = 4
FEATURE [App::DocumentObjectGroupPython] C_element031  label="C_element : 015"  # scripted group (container) (typed FeaturePython)
  n = 6
  ref = C_element
FEATURE [App::DocumentObjectGroupPython] H_element028  label="H_element : 12"  # scripted group (container) (typed FeaturePython)
  n = 12
  ref = H_element
FEATURE [App::DocumentObjectGroupPython] G4_CYCLOHEXANE  # scripted group (container) (typed FeaturePython)
  Dunit = g/cm3
  Dvalue = 0.779
  Group = -> [C_element031,H_element028]
  conduct = 2
  density = 1
  expand = 3
  formula = G4_CYCLOHEXANE
  name = G4_CYCLOHEXANE
  specific = 4
FEATURE [App::DocumentObjectGroupPython] C_element032  label="C_element : 016"  # scripted group (container) (typed FeaturePython)
  n = 6
  ref = C_element
FEATURE [App::DocumentObjectGroupPython] H_element029  label="H_element : 4"  # scripted group (container) (typed FeaturePython)
  n = 4
  ref = H_element
FEATURE [App::DocumentObjectGroupPython] Cl_element007  label="Cl_element : 2"  # scripted group (container) (typed FeaturePython)
  n = 2
  ref = Cl_element
FEATURE [App::DocumentObjectGroupPython] G4_1_2_DICHLOROBENZENE  label="G4_1.2-DICHLOROBENZENE"  # scripted group (container) (typed FeaturePython)
  Dunit = g/cm3
  Dvalue = 1.3048
  Group = -> [C_element032,H_element029,Cl_element007]
  conduct = 2
  density = 1
  expand = 3
  formula = G4_1.2-DICHLOROBENZENE
  name = G4_1.2-DICHLOROBENZENE
  specific = 4
FEATURE [App::DocumentObjectGroupPython] C_element033  label="C_element : 017"  # scripted group (container) (typed FeaturePython)
  n = 4
  ref = C_element
FEATURE [App::DocumentObjectGroupPython] H_element030  label="H_element : 8"  # scripted group (container) (typed FeaturePython)
  n = 8
  ref = H_element
FEATURE [App::DocumentObjectGroupPython] O_element031  label="O_element : 014"  # scripted group (container) (typed FeaturePython)
  n = 1
  ref = O_element
FEATURE [App::DocumentObjectGroupPython] Cl_element008  label="Cl_element : 005"  # scripted group (container) (typed FeaturePython)
  n = 2
  ref = Cl_element
FEATURE [App::DocumentObjectGroupPython] G4_DICHLORODIETHYL_ETHER  # scripted group (container) (typed FeaturePython)
  Dunit = g/cm3
  Dvalue = 1.2199
  Group = -> [C_element033,H_element030,O_element031,Cl_element008]
  conduct = 2
  density = 1
  expand = 3
  formula = G4_DICHLORODIETHYL_ETHER
  name = G4_DICHLORODIETHYL_ETHER
  specific = 4
FEATURE [App::DocumentObjectGroupPython] C_element034  label="C_element : 018"  # scripted group (container) (typed FeaturePython)
  n = 2
  ref = C_element
FEATURE [App::DocumentObjectGroupPython] H_element031  label="H_element : 014"  # scripted group (container) (typed FeaturePython)
  n = 4
  ref = H_element
FEATURE [App::DocumentObjectGroupPython] Cl_element009  label="Cl_element : 006"  # scripted group (container) (typed FeaturePython)
  n = 2
  ref = Cl_element
FEATURE [App::DocumentObjectGroupPython] G4_1_2_DICHLOROETHANE  label="G4_1.2-DICHLOROETHANE"  # scripted group (container) (typed FeaturePython)
  Dunit = g/cm3
  Dvalue = 1.2351
  Group = -> [C_element034,H_element031,Cl_element009]
  conduct = 2
  density = 1
  expand = 3
  formula = G4_1.2-DICHLOROETHANE
  name = G4_1.2-DICHLOROETHANE
  specific = 4
FEATURE [App::DocumentObjectGroupPython] C_element035  label="C_element : 019"  # scripted group (container) (typed FeaturePython)
  n = 4
  ref = C_element
FEATURE [App::DocumentObjectGroupPython] H_element032  label="H_element : 015"  # scripted group (container) (typed FeaturePython)
  n = 10
  ref = H_element
FEATURE [App::DocumentObjectGroupPython] O_element032  label="O_element : 015"  # scripted group (container) (typed FeaturePython)
  n = 1
  ref = O_element
FEATURE [App::DocumentObjectGroupPython] G4_DIETHYL_ETHER  # scripted group (container) (typed FeaturePython)
  Dunit = g/cm3
  Dvalue = 0.71378
  Group = -> [C_element035,H_element032,O_element032]
  conduct = 2
  density = 1
  expand = 3
  formula = G4_DIETHYL_ETHER
  name = G4_DIETHYL_ETHER
  specific = 4
FEATURE [App::DocumentObjectGroupPython] C_element036  label="C_element : 020"  # scripted group (container) (typed FeaturePython)
  n = 3
  ref = C_element
FEATURE [App::DocumentObjectGroupPython] H_element033  label="H_element : 016"  # scripted group (container) (typed FeaturePython)
  n = 7
  ref = H_element
FEATURE [App::DocumentObjectGroupPython] N_element015  label="N_element : 008"  # scripted group (container) (typed FeaturePython)
  n = 1
  ref = N_element
FEATURE [App::DocumentObjectGroupPython] O_element033  label="O_element : 016"  # scripted group (container) (typed FeaturePython)
  n = 1
  ref = O_element
FEATURE [App::DocumentObjectGroupPython] G4_N_N_DIMETHYL_FORMAMIDE  label="G4_N.N-DIMETHYL_FORMAMIDE"  # scripted group (container) (typed FeaturePython)
  Dunit = g/cm3
  Dvalue = 0.9487
  Group = -> [C_element036,H_element033,N_element015,O_element033]
  conduct = 2
  density = 1
  expand = 3
  formula = G4_N.N-DIMETHYL_FORMAMIDE
  name = G4_N.N-DIMETHYL_FORMAMIDE
  specific = 4
FEATURE [App::DocumentObjectGroupPython] C_element037  label="C_element : 021"  # scripted group (container) (typed FeaturePython)
  n = 2
  ref = C_element
FEATURE [App::DocumentObjectGroupPython] H_element034  label="H_element : 017"  # scripted group (container) (typed FeaturePython)
  n = 6
  ref = H_element
FEATURE [App::DocumentObjectGroupPython] O_element034  label="O_element : 017"  # scripted group (container) (typed FeaturePython)
  n = 1
  ref = O_element
FEATURE [App::DocumentObjectGroupPython] S_element009  label="S_element : 003"  # scripted group (container) (typed FeaturePython)
  n = 1
  ref = S_element
FEATURE [App::DocumentObjectGroupPython] G4_DIMETHYL_SULFOXIDE  # scripted group (container) (typed FeaturePython)
  Dunit = g/cm3
  Dvalue = 1.1014
  Group = -> [C_element037,H_element034,O_element034,S_element009]
  conduct = 2
  density = 1
  expand = 3
  formula = G4_DIMETHYL_SULFOXIDE
  name = G4_DIMETHYL_SULFOXIDE
  specific = 4
FEATURE [App::DocumentObjectGroupPython] C_element038  label="C_element : 022"  # scripted group (container) (typed FeaturePython)
  n = 2
  ref = C_element
FEATURE [App::DocumentObjectGroupPython] H_element035  label="H_element : 018"  # scripted group (container) (typed FeaturePython)
  n = 6
  ref = H_element
FEATURE [App::DocumentObjectGroupPython] G4_ETHANE  # scripted group (container) (typed FeaturePython)
  Dunit = g/cm3
  Dvalue = 0.00125324
  Group = -> [C_element038,H_element035]
  conduct = 2
  density = 1
  expand = 3
  formula = G4_ETHANE
  name = G4_ETHANE
  specific = 4
FEATURE [App::DocumentObjectGroupPython] C_element039  label="C_element : 023"  # scripted group (container) (typed FeaturePython)
  n = 2
  ref = C_element
FEATURE [App::DocumentObjectGroupPython] H_element036  label="H_element : 019"  # scripted group (container) (typed FeaturePython)
  n = 6
  ref = H_element
FEATURE [App::DocumentObjectGroupPython] O_element035  label="O_element : 018"  # scripted group (container) (typed FeaturePython)
  n = 1
  ref = O_element
FEATURE [App::DocumentObjectGroupPython] G4_ETHYL_ALCOHOL  # scripted group (container) (typed FeaturePython)
  Dunit = g/cm3
  Dvalue = 0.7893
  Group = -> [C_element039,H_element036,O_element035]
  conduct = 2
  density = 1
  expand = 3
  formula = G4_ETHYL_ALCOHOL
  name = G4_ETHYL_ALCOHOL
  specific = 4
FEATURE [App::DocumentObjectGroupPython] H_element037  label="H_element : 0.090"  # scripted group (container) (typed FeaturePython)
  n = 0.090027
FEATURE [App::DocumentObjectGroupPython] C_element040  label="C_element : 0.585"  # scripted group (container) (typed FeaturePython)
  n = 0.585182
FEATURE [App::DocumentObjectGroupPython] O_element036  label="O_element : 0.325"  # scripted group (container) (typed FeaturePython)
  n = 0.324791
FEATURE [App::DocumentObjectGroupPython] G4_ETHYL_CELLULOSE  # scripted group (container) (typed FeaturePython)
  Dunit = g/cm3
  Dvalue = 1.13
  Group = -> [H_element037,C_element040,O_element036]
  conduct = 2
  density = 1
  expand = 3
  formula = G4_ETHYL_CELLULOSE
  name = G4_ETHYL_CELLULOSE
  specific = 4
FEATURE [App::DocumentObjectGroupPython] C_element041  label="C_element : 024"  # scripted group (container) (typed FeaturePython)
  n = 2
  ref = C_element
FEATURE [App::DocumentObjectGroupPython] H_element038  label="H_element : 020"  # scripted group (container) (typed FeaturePython)
  n = 4
  ref = H_element
FEATURE [App::DocumentObjectGroupPython] G4_ETHYLENE  # scripted group (container) (typed FeaturePython)
  Dunit = g/cm3
  Dvalue = 0.00117497
  Group = -> [C_element041,H_element038]
  conduct = 2
  density = 1
  expand = 3
  formula = G4_ETHYLENE
  name = G4_ETHYLENE
  specific = 4
FEATURE [App::DocumentObjectGroupPython] H_element039  label="H_element : 0.096"  # scripted group (container) (typed FeaturePython)
  n = 0.096
FEATURE [App::DocumentObjectGroupPython] C_element042  label="C_element : 0.195"  # scripted group (container) (typed FeaturePython)
  n = 0.195
FEATURE [App::DocumentObjectGroupPython] N_element016  label="N_element : 0.057"  # scripted group (container) (typed FeaturePython)
  n = 0.057
FEATURE [App::DocumentObjectGroupPython] O_element037  label="O_element : 0.646"  # scripted group (container) (typed FeaturePython)
  n = 0.646
FEATURE [App::DocumentObjectGroupPython] Na_element006  label="Na_element : 0.017"  # scripted group (container) (typed FeaturePython)
  n = 0.001
FEATURE [App::DocumentObjectGroupPython] P_element005  label="P_element : 0.104"  # scripted group (container) (typed FeaturePython)
  n = 0.001
FEATURE [App::DocumentObjectGroupPython] S_element010  label="S_element : 0.016"  # scripted group (container) (typed FeaturePython)
  n = 0.003
FEATURE [App::DocumentObjectGroupPython] Cl_element010  label="Cl_element : 0.005"  # scripted group (container) (typed FeaturePython)
  n = 0.001
FEATURE [App::DocumentObjectGroupPython] G4_EYE_LENS_ICRP  # scripted group (container) (typed FeaturePython)
  Dunit = g/cm3
  Dvalue = 1.07
  Group = -> [H_element039,C_element042,N_element016,O_element037,Na_element006,P_element005,S_element010,Cl_element010]
  conduct = 2
  density = 1
  expand = 3
  formula = G4_EYE_LENS_ICRP
  name = G4_EYE_LENS_ICRP
  specific = 4
FEATURE [App::DocumentObjectGroupPython] Fe_element003  label="Fe_element : 2"  # scripted group (container) (typed FeaturePython)
  n = 2
  ref = Fe_element
FEATURE [App::DocumentObjectGroupPython] O_element038  label="O_element : 019"  # scripted group (container) (typed FeaturePython)
  n = 3
  ref = O_element
FEATURE [App::DocumentObjectGroupPython] G4_FERRIC_OXIDE  # scripted group (container) (typed FeaturePython)
  Dunit = g/cm3
  Dvalue = 5.2
  Group = -> [Fe_element003,O_element038]
  conduct = 2
  density = 1
  expand = 3
  formula = G4_FERRIC_OXIDE
  name = G4_FERRIC_OXIDE
  specific = 4
FEATURE [App::DocumentObjectGroupPython] Fe_element004  label="Fe_element : 1"  # scripted group (container) (typed FeaturePython)
  n = 1
  ref = Fe_element
FEATURE [App::DocumentObjectGroupPython] B_element003  label="B_element : 1"  # scripted group (container) (typed FeaturePython)
  n = 1
  ref = B_element
FEATURE [App::DocumentObjectGroupPython] G4_FERROBORIDE  # scripted group (container) (typed FeaturePython)
  Dunit = g/cm3
  Dvalue = 7.15
  Group = -> [Fe_element004,B_element003]
  conduct = 2
  density = 1
  expand = 3
  formula = G4_FERROBORIDE
  name = G4_FERROBORIDE
  specific = 4
FEATURE [App::DocumentObjectGroupPython] Fe_element005  label="Fe_element : 003"  # scripted group (container) (typed FeaturePython)
  n = 1
  ref = Fe_element
FEATURE [App::DocumentObjectGroupPython] O_element039  label="O_element : 020"  # scripted group (container) (typed FeaturePython)
  n = 1
  ref = O_element
FEATURE [App::DocumentObjectGroupPython] G4_FERROUS_OXIDE  # scripted group (container) (typed FeaturePython)
  Dunit = g/cm3
  Dvalue = 5.7
  Group = -> [Fe_element005,O_element039]
  conduct = 2
  density = 1
  expand = 3
  formula = G4_FERROUS_OXIDE
  name = G4_FERROUS_OXIDE
  specific = 4
FEATURE [App::DocumentObjectGroupPython] H_element040  label="H_element : 0.115"  # scripted group (container) (typed FeaturePython)
  n = 0.108259
FEATURE [App::DocumentObjectGroupPython] N_element017  label="N_element : 0.000"  # scripted group (container) (typed FeaturePython)
  n = 2.7e-05
FEATURE [App::DocumentObjectGroupPython] O_element040  label="O_element : 0.879"  # scripted group (container) (typed FeaturePython)
  n = 0.878636
FEATURE [App::DocumentObjectGroupPython] Na_element007  label="Na_element : 0.000"  # scripted group (container) (typed FeaturePython)
  n = 2.2e-05
FEATURE [App::DocumentObjectGroupPython] S_element011  label="S_element : 0.013"  # scripted group (container) (typed FeaturePython)
  n = 0.012968
FEATURE [App::DocumentObjectGroupPython] Cl_element011  label="Cl_element : 0.000"  # scripted group (container) (typed FeaturePython)
  n = 3.4e-05
FEATURE [App::DocumentObjectGroupPython] Fe_element006  label="Fe_element : 0.000"  # scripted group (container) (typed FeaturePython)
  n = 5.4e-05
FEATURE [App::DocumentObjectGroupPython] G4_FERROUS_SULFATE  # scripted group (container) (typed FeaturePython)
  Dunit = g/cm3
  Dvalue = 1.024
  Group = -> [H_element040,N_element017,O_element040,Na_element007,S_element011,Cl_element011,Fe_element006]
  conduct = 2
  density = 1
  expand = 3
  formula = G4_FERROUS_SULFATE
  name = G4_FERROUS_SULFATE
  specific = 4
FEATURE [App::DocumentObjectGroupPython] C_element043  label="C_element : 0.099"  # scripted group (container) (typed FeaturePython)
  n = 0.099335
FEATURE [App::DocumentObjectGroupPython] F_element007  label="F_element : 0.314"  # scripted group (container) (typed FeaturePython)
  n = 0.314247
FEATURE [App::DocumentObjectGroupPython] Cl_element012  label="Cl_element : 0.586"  # scripted group (container) (typed FeaturePython)
  n = 0.586418
FEATURE [App::DocumentObjectGroupPython] G4_FREON_12  label="G4_FREON-12"  # scripted group (container) (typed FeaturePython)
  Dunit = g/cm3
  Dvalue = 1.12
  Group = -> [C_element043,F_element007,Cl_element012]
  conduct = 2
  density = 1
  expand = 3
  formula = G4_FREON-12
  name = G4_FREON-12
  specific = 4
FEATURE [App::DocumentObjectGroupPython] C_element044  label="C_element : 0.057"  # scripted group (container) (typed FeaturePython)
  n = 0.057245
FEATURE [App::DocumentObjectGroupPython] F_element008  label="F_element : 0.181"  # scripted group (container) (typed FeaturePython)
  n = 0.181096
FEATURE [App::DocumentObjectGroupPython] Br_element001  label="Br_element : 0.762"  # scripted group (container) (typed FeaturePython)
  n = 0.761659
FEATURE [App::DocumentObjectGroupPython] G4_FREON_12B2  label="G4_FREON-12B2"  # scripted group (container) (typed FeaturePython)
  Dunit = g/cm3
  Dvalue = 1.8
  Group = -> [C_element044,F_element008,Br_element001]
  conduct = 2
  density = 1
  expand = 3
  formula = G4_FREON-12B2
  name = G4_FREON-12B2
  specific = 4
FEATURE [App::DocumentObjectGroupPython] C_element045  label="C_element : 0.115"  # scripted group (container) (typed FeaturePython)
  n = 0.114983
FEATURE [App::DocumentObjectGroupPython] F_element009  label="F_element : 0.546"  # scripted group (container) (typed FeaturePython)
  n = 0.545621
FEATURE [App::DocumentObjectGroupPython] Cl_element013  label="Cl_element : 0.339"  # scripted group (container) (typed FeaturePython)
  n = 0.339396
FEATURE [App::DocumentObjectGroupPython] G4_FREON_13  label="G4_FREON-13"  # scripted group (container) (typed FeaturePython)
  Dunit = g/cm3
  Dvalue = 0.95
  Group = -> [C_element045,F_element009,Cl_element013]
  conduct = 2
  density = 1
  expand = 3
  formula = G4_FREON-13
  name = G4_FREON-13
  specific = 4
FEATURE [App::DocumentObjectGroupPython] C_element046  label="C_element : 025"  # scripted group (container) (typed FeaturePython)
  n = 1
  ref = C_element
FEATURE [App::DocumentObjectGroupPython] F_element010  label="F_element : 3"  # scripted group (container) (typed FeaturePython)
  n = 3
  ref = F_element
FEATURE [App::DocumentObjectGroupPython] Br_element002  label="Br_element : 1"  # scripted group (container) (typed FeaturePython)
  n = 1
  ref = Br_element
FEATURE [App::DocumentObjectGroupPython] G4_FREON_13B1  label="G4_FREON-13B1"  # scripted group (container) (typed FeaturePython)
  Dunit = g/cm3
  Dvalue = 1.5
  Group = -> [C_element046,F_element010,Br_element002]
  conduct = 2
  density = 1
  expand = 3
  formula = G4_FREON-13B1
  name = G4_FREON-13B1
  specific = 4
FEATURE [App::DocumentObjectGroupPython] C_element047  label="C_element : 0.061"  # scripted group (container) (typed FeaturePython)
  n = 0.061309
FEATURE [App::DocumentObjectGroupPython] F_element011  label="F_element : 0.291"  # scripted group (container) (typed FeaturePython)
  n = 0.290924
FEATURE [App::DocumentObjectGroupPython] I_element002  label="I_element : 0.648"  # scripted group (container) (typed FeaturePython)
  n = 0.647767
FEATURE [App::DocumentObjectGroupPython] G4_FREON_13I1  label="G4_FREON-13I1"  # scripted group (container) (typed FeaturePython)
  Dunit = g/cm3
  Dvalue = 1.8
  Group = -> [C_element047,F_element011,I_element002]
  conduct = 2
  density = 1
  expand = 3
  formula = G4_FREON-13I1
  name = G4_FREON-13I1
  specific = 4
FEATURE [App::DocumentObjectGroupPython] Gd_element001  label="Gd_element : 2"  # scripted group (container) (typed FeaturePython)
  n = 2
  ref = Gd_element
FEATURE [App::DocumentObjectGroupPython] O_element041  label="O_element : 021"  # scripted group (container) (typed FeaturePython)
  n = 2
  ref = O_element
FEATURE [App::DocumentObjectGroupPython] S_element012  label="S_element : 004"  # scripted group (container) (typed FeaturePython)
  n = 1
  ref = S_element
FEATURE [App::DocumentObjectGroupPython] G4_GADOLINIUM_OXYSULFIDE  # scripted group (container) (typed FeaturePython)
  Dunit = g/cm3
  Dvalue = 7.44
  Group = -> [Gd_element001,O_element041,S_element012]
  conduct = 2
  density = 1
  expand = 3
  formula = G4_GADOLINIUM_OXYSULFIDE
  name = G4_GADOLINIUM_OXYSULFIDE
  specific = 4
FEATURE [App::DocumentObjectGroupPython] Ga_element001  label="Ga_element : 1"  # scripted group (container) (typed FeaturePython)
  n = 1
  ref = Ga_element
FEATURE [App::DocumentObjectGroupPython] As_element001  label="As_element : 1"  # scripted group (container) (typed FeaturePython)
  n = 1
  ref = As_element
FEATURE [App::DocumentObjectGroupPython] G4_GALLIUM_ARSENIDE  # scripted group (container) (typed FeaturePython)
  Dunit = g/cm3
  Dvalue = 5.31
  Group = -> [Ga_element001,As_element001]
  conduct = 2
  density = 1
  expand = 3
  formula = G4_GALLIUM_ARSENIDE
  name = G4_GALLIUM_ARSENIDE
  specific = 4
FEATURE [App::DocumentObjectGroupPython] H_element041  label="H_element : 0.081"  # scripted group (container) (typed FeaturePython)
  n = 0.08118
FEATURE [App::DocumentObjectGroupPython] C_element048  label="C_element : 0.416"  # scripted group (container) (typed FeaturePython)
  n = 0.41606
FEATURE [App::DocumentObjectGroupPython] N_element018  label="N_element : 0.111"  # scripted group (container) (typed FeaturePython)
  n = 0.11124
FEATURE [App::DocumentObjectGroupPython] O_element042  label="O_element : 0.381"  # scripted group (container) (typed FeaturePython)
  n = 0.38064
FEATURE [App::DocumentObjectGroupPython] S_element013  label="S_element : 0.011"  # scripted group (container) (typed FeaturePython)
  n = 0.01088
FEATURE [App::DocumentObjectGroupPython] G4_GEL_PHOTO_EMULSION  # scripted group (container) (typed FeaturePython)
  Dunit = g/cm3
  Dvalue = 1.2914
  Group = -> [H_element041,C_element048,N_element018,O_element042,S_element013]
  conduct = 2
  density = 1
  expand = 3
  formula = G4_GEL_PHOTO_EMULSION
  name = G4_GEL_PHOTO_EMULSION
  specific = 4
FEATURE [App::DocumentObjectGroupPython] B_element004  label="B_element : 0.040"  # scripted group (container) (typed FeaturePython)
  n = 0.0400639
FEATURE [App::DocumentObjectGroupPython] O_element043  label="O_element : 0.540"  # scripted group (container) (typed FeaturePython)
  n = 0.539561
FEATURE [App::DocumentObjectGroupPython] Na_element008  label="Na_element : 0.028"  # scripted group (container) (typed FeaturePython)
  n = 0.0281909
FEATURE [App::DocumentObjectGroupPython] Al_element003  label="Al_element : 0.012"  # scripted group (container) (typed FeaturePython)
  n = 0.011644
FEATURE [App::DocumentObjectGroupPython] Si_element003  label="Si_element : 0.377"  # scripted group (container) (typed FeaturePython)
  n = 0.377219
FEATURE [App::DocumentObjectGroupPython] K_element004  label="K_element : 0.014"  # scripted group (container) (typed FeaturePython)
  n = 0.00332099
FEATURE [App::DocumentObjectGroupPython] G4_Pyrex_Glass  # scripted group (container) (typed FeaturePython)
  Dunit = g/cm3
  Dvalue = 2.23
  Group = -> [B_element004,O_element043,Na_element008,Al_element003,Si_element003,K_element004]
  conduct = 2
  density = 1
  expand = 3
  formula = G4_Pyrex_Glass
  name = G4_Pyrex_Glass
  specific = 4
FEATURE [App::DocumentObjectGroupPython] O_element044  label="O_element : 0.156"  # scripted group (container) (typed FeaturePython)
  n = 0.156453
FEATURE [App::DocumentObjectGroupPython] Si_element004  label="Si_element : 0.081"  # scripted group (container) (typed FeaturePython)
  n = 0.080866
FEATURE [App::DocumentObjectGroupPython] Ti_element001  label="Ti_element : 0.008"  # scripted group (container) (typed FeaturePython)
  n = 0.008092
FEATURE [App::DocumentObjectGroupPython] As_element002  label="As_element : 0.003"  # scripted group (container) (typed FeaturePython)
  n = 0.002651
FEATURE [App::DocumentObjectGroupPython] Pb_element001  label="Pb_element : 0.752"  # scripted group (container) (typed FeaturePython)
  n = 0.751938
FEATURE [App::DocumentObjectGroupPython] G4_GLASS_LEAD  # scripted group (container) (typed FeaturePython)
  Dunit = g/cm3
  Dvalue = 6.22
  Group = -> [O_element044,Si_element004,Ti_element001,As_element002,Pb_element001]
  conduct = 2
  density = 1
  expand = 3
  formula = G4_GLASS_LEAD
  name = G4_GLASS_LEAD
  specific = 4
FEATURE [App::DocumentObjectGroupPython] O_element045  label="O_element : 0.460"  # scripted group (container) (typed FeaturePython)
  n = 0.4598
FEATURE [App::DocumentObjectGroupPython] Na_element009  label="Na_element : 0.096"  # scripted group (container) (typed FeaturePython)
  n = 0.0964411
FEATURE [App::DocumentObjectGroupPython] Si_element005  label="Si_element : 0.378"  # scripted group (container) (typed FeaturePython)
  n = 0.336553
FEATURE [App::DocumentObjectGroupPython] Ca_element011  label="Ca_element : 0.107"  # scripted group (container) (typed FeaturePython)
  n = 0.107205
FEATURE [App::DocumentObjectGroupPython] G4_GLASS_PLATE  # scripted group (container) (typed FeaturePython)
  Dunit = g/cm3
  Dvalue = 2.4
  Group = -> [O_element045,Na_element009,Si_element005,Ca_element011]
  conduct = 2
  density = 1
  expand = 3
  formula = G4_GLASS_PLATE
  name = G4_GLASS_PLATE
  specific = 4
FEATURE [App::DocumentObjectGroupPython] C_element049  label="C_element : 026"  # scripted group (container) (typed FeaturePython)
  n = 5
  ref = C_element
FEATURE [App::DocumentObjectGroupPython] H_element042  label="H_element : 021"  # scripted group (container) (typed FeaturePython)
  n = 10
  ref = H_element
FEATURE [App::DocumentObjectGroupPython] N_element019  label="N_element : 2"  # scripted group (container) (typed FeaturePython)
  n = 2
  ref = N_element
FEATURE [App::DocumentObjectGroupPython] O_element046  label="O_element : 022"  # scripted group (container) (typed FeaturePython)
  n = 3
  ref = O_element
FEATURE [App::DocumentObjectGroupPython] G4_GLUTAMINE  # scripted group (container) (typed FeaturePython)
  Dunit = g/cm3
  Dvalue = 1.46
  Group = -> [C_element049,H_element042,N_element019,O_element046]
  conduct = 2
  density = 1
  expand = 3
  formula = G4_GLUTAMINE
  name = G4_GLUTAMINE
  specific = 4
FEATURE [App::DocumentObjectGroupPython] C_element050  label="C_element : 027"  # scripted group (container) (typed FeaturePython)
  n = 3
  ref = C_element
FEATURE [App::DocumentObjectGroupPython] H_element043  label="H_element : 022"  # scripted group (container) (typed FeaturePython)
  n = 8
  ref = H_element
FEATURE [App::DocumentObjectGroupPython] O_element047  label="O_element : 023"  # scripted group (container) (typed FeaturePython)
  n = 3
  ref = O_element
FEATURE [App::DocumentObjectGroupPython] G4_GLYCEROL  # scripted group (container) (typed FeaturePython)
  Dunit = g/cm3
  Dvalue = 1.2613
  Group = -> [C_element050,H_element043,O_element047]
  conduct = 2
  density = 1
  expand = 3
  formula = G4_GLYCEROL
  name = G4_GLYCEROL
  specific = 4
FEATURE [App::DocumentObjectGroupPython] C_element051  label="C_element : 028"  # scripted group (container) (typed FeaturePython)
  n = 5
  ref = C_element
FEATURE [App::DocumentObjectGroupPython] H_element044  label="H_element : 023"  # scripted group (container) (typed FeaturePython)
  n = 5
  ref = H_element
FEATURE [App::DocumentObjectGroupPython] N_element020  label="N_element : 009"  # scripted group (container) (typed FeaturePython)
  n = 5
  ref = N_element
FEATURE [App::DocumentObjectGroupPython] O_element048  label="O_element : 024"  # scripted group (container) (typed FeaturePython)
  n = 1
  ref = O_element
FEATURE [App::DocumentObjectGroupPython] G4_GUANINE  # scripted group (container) (typed FeaturePython)
  Dunit = g/cm3
  Dvalue = 2.2
  Group = -> [C_element051,H_element044,N_element020,O_element048]
  conduct = 2
  density = 1
  expand = 3
  formula = G4_GUANINE
  name = G4_GUANINE
  specific = 4
FEATURE [App::DocumentObjectGroupPython] Ca_element012  label="Ca_element : 006"  # scripted group (container) (typed FeaturePython)
  n = 1
  ref = Ca_element
FEATURE [App::DocumentObjectGroupPython] S_element014  label="S_element : 005"  # scripted group (container) (typed FeaturePython)
  n = 1
  ref = S_element
FEATURE [App::DocumentObjectGroupPython] O_element049  label="O_element : 6"  # scripted group (container) (typed FeaturePython)
  n = 6
  ref = O_element
FEATURE [App::DocumentObjectGroupPython] H_element045  label="H_element : 024"  # scripted group (container) (typed FeaturePython)
  n = 4
  ref = H_element
FEATURE [App::DocumentObjectGroupPython] G4_GYPSUM  # scripted group (container) (typed FeaturePython)
  Dunit = g/cm3
  Dvalue = 2.32
  Group = -> [Ca_element012,S_element014,O_element049,H_element045]
  conduct = 2
  density = 1
  expand = 3
  formula = G4_GYPSUM
  name = G4_GYPSUM
  specific = 4
FEATURE [App::DocumentObjectGroupPython] C_element052  label="C_element : 7"  # scripted group (container) (typed FeaturePython)
  n = 7
  ref = C_element
FEATURE [App::DocumentObjectGroupPython] H_element046  label="H_element : 16"  # scripted group (container) (typed FeaturePython)
  n = 16
  ref = H_element
FEATURE [App::DocumentObjectGroupPython] G4_N_HEPTANE  label="G4_N-HEPTANE"  # scripted group (container) (typed FeaturePython)
  Dunit = g/cm3
  Dvalue = 0.68376
  Group = -> [C_element052,H_element046]
  conduct = 2
  density = 1
  expand = 3
  formula = G4_N-HEPTANE
  name = G4_N-HEPTANE
  specific = 4
FEATURE [App::DocumentObjectGroupPython] C_element053  label="C_element : 029"  # scripted group (container) (typed FeaturePython)
  n = 6
  ref = C_element
FEATURE [App::DocumentObjectGroupPython] H_element047  label="H_element : 14"  # scripted group (container) (typed FeaturePython)
  n = 14
  ref = H_element
FEATURE [App::DocumentObjectGroupPython] G4_N_HEXANE  label="G4_N-HEXANE"  # scripted group (container) (typed FeaturePython)
  Dunit = g/cm3
  Dvalue = 0.6603
  Group = -> [C_element053,H_element047]
  conduct = 2
  density = 1
  expand = 3
  formula = G4_N-HEXANE
  name = G4_N-HEXANE
  specific = 4
FEATURE [App::DocumentObjectGroupPython] C_element054  label="C_element : 22"  # scripted group (container) (typed FeaturePython)
  n = 22
  ref = C_element
FEATURE [App::DocumentObjectGroupPython] H_element048  label="H_element : 025"  # scripted group (container) (typed FeaturePython)
  n = 10
  ref = H_element
FEATURE [App::DocumentObjectGroupPython] N_element021  label="N_element : 010"  # scripted group (container) (typed FeaturePython)
  n = 2
  ref = N_element
FEATURE [App::DocumentObjectGroupPython] O_element050  label="O_element : 025"  # scripted group (container) (typed FeaturePython)
  n = 5
  ref = O_element
FEATURE [App::DocumentObjectGroupPython] G4_KAPTON  # scripted group (container) (typed FeaturePython)
  Dunit = g/cm3
  Dvalue = 1.42
  Group = -> [C_element054,H_element048,N_element021,O_element050]
  conduct = 2
  density = 1
  expand = 3
  formula = G4_KAPTON
  name = G4_KAPTON
  specific = 4
FEATURE [App::DocumentObjectGroupPython] La_element001  label="La_element : 1"  # scripted group (container) (typed FeaturePython)
  n = 1
  ref = La_element
FEATURE [App::DocumentObjectGroupPython] Br_element003  label="Br_element : 002"  # scripted group (container) (typed FeaturePython)
  n = 1
  ref = Br_element
FEATURE [App::DocumentObjectGroupPython] O_element051  label="O_element : 026"  # scripted group (container) (typed FeaturePython)
  n = 1
  ref = O_element
FEATURE [App::DocumentObjectGroupPython] G4_LANTHANUM_OXYBROMIDE  # scripted group (container) (typed FeaturePython)
  Dunit = g/cm3
  Dvalue = 6.28
  Group = -> [La_element001,Br_element003,O_element051]
  conduct = 2
  density = 1
  expand = 3
  formula = G4_LANTHANUM_OXYBROMIDE
  name = G4_LANTHANUM_OXYBROMIDE
  specific = 4
FEATURE [App::DocumentObjectGroupPython] La_element002  label="La_element : 2"  # scripted group (container) (typed FeaturePython)
  n = 2
  ref = La_element
FEATURE [App::DocumentObjectGroupPython] O_element052  label="O_element : 027"  # scripted group (container) (typed FeaturePython)
  n = 2
  ref = O_element
FEATURE [App::DocumentObjectGroupPython] S_element015  label="S_element : 006"  # scripted group (container) (typed FeaturePython)
  n = 1
  ref = S_element
FEATURE [App::DocumentObjectGroupPython] G4_LANTHANUM_OXYSULFIDE  # scripted group (container) (typed FeaturePython)
  Dunit = g/cm3
  Dvalue = 5.86
  Group = -> [La_element002,O_element052,S_element015]
  conduct = 2
  density = 1
  expand = 3
  formula = G4_LANTHANUM_OXYSULFIDE
  name = G4_LANTHANUM_OXYSULFIDE
  specific = 4
FEATURE [App::DocumentObjectGroupPython] O_element053  label="O_element : 0.072"  # scripted group (container) (typed FeaturePython)
  n = 0.071682
FEATURE [App::DocumentObjectGroupPython] Pb_element002  label="Pb_element : 0.928"  # scripted group (container) (typed FeaturePython)
  n = 0.928318
FEATURE [App::DocumentObjectGroupPython] G4_LEAD_OXIDE  # scripted group (container) (typed FeaturePython)
  Dunit = g/cm3
  Dvalue = 9.53
  Group = -> [O_element053,Pb_element002]
  conduct = 2
  density = 1
  expand = 3
  formula = G4_LEAD_OXIDE
  name = G4_LEAD_OXIDE
  specific = 4
FEATURE [App::DocumentObjectGroupPython] Li_element001  label="Li_element : 1"  # scripted group (container) (typed FeaturePython)
  n = 1
  ref = Li_element
FEATURE [App::DocumentObjectGroupPython] N_element022  label="N_element : 011"  # scripted group (container) (typed FeaturePython)
  n = 1
  ref = N_element
FEATURE [App::DocumentObjectGroupPython] H_element049  label="H_element : 026"  # scripted group (container) (typed FeaturePython)
  n = 2
  ref = H_element
FEATURE [App::DocumentObjectGroupPython] G4_LITHIUM_AMIDE  # scripted group (container) (typed FeaturePython)
  Dunit = g/cm3
  Dvalue = 1.178
  Group = -> [Li_element001,N_element022,H_element049]
  conduct = 2
  density = 1
  expand = 3
  formula = G4_LITHIUM_AMIDE
  name = G4_LITHIUM_AMIDE
  specific = 4
FEATURE [App::DocumentObjectGroupPython] Li_element002  label="Li_element : 2"  # scripted group (container) (typed FeaturePython)
  n = 2
  ref = Li_element
FEATURE [App::DocumentObjectGroupPython] C_element055  label="C_element : 030"  # scripted group (container) (typed FeaturePython)
  n = 1
  ref = C_element
FEATURE [App::DocumentObjectGroupPython] O_element054  label="O_element : 028"  # scripted group (container) (typed FeaturePython)
  n = 3
  ref = O_element
FEATURE [App::DocumentObjectGroupPython] G4_LITHIUM_CARBONATE  # scripted group (container) (typed FeaturePython)
  Dunit = g/cm3
  Dvalue = 2.11
  Group = -> [Li_element002,C_element055,O_element054]
  conduct = 2
  density = 1
  expand = 3
  formula = G4_LITHIUM_CARBONATE
  name = G4_LITHIUM_CARBONATE
  specific = 4
FEATURE [App::DocumentObjectGroupPython] Li_element003  label="Li_element : 003"  # scripted group (container) (typed FeaturePython)
  n = 1
  ref = Li_element
FEATURE [App::DocumentObjectGroupPython] F_element012  label="F_element : 004"  # scripted group (container) (typed FeaturePython)
  n = 1
  ref = F_element
FEATURE [App::DocumentObjectGroupPython] G4_LITHIUM_FLUORIDE  # scripted group (container) (typed FeaturePython)
  Dunit = g/cm3
  Dvalue = 2.635
  Group = -> [Li_element003,F_element012]
  conduct = 2
  density = 1
  expand = 3
  formula = G4_LITHIUM_FLUORIDE
  name = G4_LITHIUM_FLUORIDE
  specific = 4
FEATURE [App::DocumentObjectGroupPython] Li_element004  label="Li_element : 004"  # scripted group (container) (typed FeaturePython)
  n = 1
  ref = Li_element
FEATURE [App::DocumentObjectGroupPython] H_element050  label="H_element : 027"  # scripted group (container) (typed FeaturePython)
  n = 1
  ref = H_element
FEATURE [App::DocumentObjectGroupPython] G4_LITHIUM_HYDRIDE  # scripted group (container) (typed FeaturePython)
  Dunit = g/cm3
  Dvalue = 0.82
  Group = -> [Li_element004,H_element050]
  conduct = 2
  density = 1
  expand = 3
  formula = G4_LITHIUM_HYDRIDE
  name = G4_LITHIUM_HYDRIDE
  specific = 4
FEATURE [App::DocumentObjectGroupPython] Li_element005  label="Li_element : 005"  # scripted group (container) (typed FeaturePython)
  n = 1
  ref = Li_element
FEATURE [App::DocumentObjectGroupPython] I_element003  label="I_element : 002"  # scripted group (container) (typed FeaturePython)
  n = 1
  ref = I_element
FEATURE [App::DocumentObjectGroupPython] G4_LITHIUM_IODIDE  # scripted group (container) (typed FeaturePython)
  Dunit = g/cm3
  Dvalue = 3.494
  Group = -> [Li_element005,I_element003]
  conduct = 2
  density = 1
  expand = 3
  formula = G4_LITHIUM_IODIDE
  name = G4_LITHIUM_IODIDE
  specific = 4
FEATURE [App::DocumentObjectGroupPython] Li_element006  label="Li_element : 006"  # scripted group (container) (typed FeaturePython)
  n = 2
  ref = Li_element
FEATURE [App::DocumentObjectGroupPython] O_element055  label="O_element : 029"  # scripted group (container) (typed FeaturePython)
  n = 1
  ref = O_element
FEATURE [App::DocumentObjectGroupPython] G4_LITHIUM_OXIDE  # scripted group (container) (typed FeaturePython)
  Dunit = g/cm3
  Dvalue = 2.013
  Group = -> [Li_element006,O_element055]
  conduct = 2
  density = 1
  expand = 3
  formula = G4_LITHIUM_OXIDE
  name = G4_LITHIUM_OXIDE
  specific = 4
FEATURE [App::DocumentObjectGroupPython] Li_element007  label="Li_element : 007"  # scripted group (container) (typed FeaturePython)
  n = 2
  ref = Li_element
FEATURE [App::DocumentObjectGroupPython] B_element005  label="B_element : 005"  # scripted group (container) (typed FeaturePython)
  n = 4
  ref = B_element
FEATURE [App::DocumentObjectGroupPython] O_element056  label="O_element : 7"  # scripted group (container) (typed FeaturePython)
  n = 7
  ref = O_element
FEATURE [App::DocumentObjectGroupPython] G4_LITHIUM_TETRABORATE  # scripted group (container) (typed FeaturePython)
  Dunit = g/cm3
  Dvalue = 2.44
  Group = -> [Li_element007,B_element005,O_element056]
  conduct = 2
  density = 1
  expand = 3
  formula = G4_LITHIUM_TETRABORATE
  name = G4_LITHIUM_TETRABORATE
  specific = 4
FEATURE [App::DocumentObjectGroupPython] H_element051  label="H_element : 0.105"  # scripted group (container) (typed FeaturePython)
  n = 0.105
FEATURE [App::DocumentObjectGroupPython] C_element056  label="C_element : 0.083"  # scripted group (container) (typed FeaturePython)
  n = 0.083
FEATURE [App::DocumentObjectGroupPython] N_element023  label="N_element : 0.023"  # scripted group (container) (typed FeaturePython)
  n = 0.023
FEATURE [App::DocumentObjectGroupPython] O_element057  label="O_element : 0.779"  # scripted group (container) (typed FeaturePython)
  n = 0.779
FEATURE [App::DocumentObjectGroupPython] Na_element010  label="Na_element : 0.097"  # scripted group (container) (typed FeaturePython)
  n = 0.002
FEATURE [App::DocumentObjectGroupPython] P_element006  label="P_element : 0.105"  # scripted group (container) (typed FeaturePython)
  n = 0.001
FEATURE [App::DocumentObjectGroupPython] S_element016  label="S_element : 0.017"  # scripted group (container) (typed FeaturePython)
  n = 0.002
FEATURE [App::DocumentObjectGroupPython] Cl_element014  label="Cl_element : 0.587"  # scripted group (container) (typed FeaturePython)
  n = 0.003
FEATURE [App::DocumentObjectGroupPython] K_element005  label="K_element : 0.015"  # scripted group (container) (typed FeaturePython)
  n = 0.002
FEATURE [App::DocumentObjectGroupPython] G4_LUNG_ICRP  # scripted group (container) (typed FeaturePython)
  Dunit = g/cm3
  Dvalue = 1.04
  Group = -> [H_element051,C_element056,N_element023,O_element057,Na_element010,P_element006,S_element016,Cl_element014,K_element005]
  conduct = 2
  density = 1
  expand = 3
  formula = G4_LUNG_ICRP
  name = G4_LUNG_ICRP
  specific = 4
FEATURE [App::DocumentObjectGroupPython] H_element052  label="H_element : 0.116"  # scripted group (container) (typed FeaturePython)
  n = 0.114318
FEATURE [App::DocumentObjectGroupPython] C_element057  label="C_element : 0.656"  # scripted group (container) (typed FeaturePython)
  n = 0.655824
FEATURE [App::DocumentObjectGroupPython] O_element058  label="O_element : 0.092"  # scripted group (container) (typed FeaturePython)
  n = 0.0921831
FEATURE [App::DocumentObjectGroupPython] Mg_element004  label="Mg_element : 0.135"  # scripted group (container) (typed FeaturePython)
  n = 0.134792
FEATURE [App::DocumentObjectGroupPython] Ca_element013  label="Ca_element : 0.003"  # scripted group (container) (typed FeaturePython)
  n = 0.002883
FEATURE [App::DocumentObjectGroupPython] G4_M3_WAX  # scripted group (container) (typed FeaturePython)
  Dunit = g/cm3
  Dvalue = 1.05
  Group = -> [H_element052,C_element057,O_element058,Mg_element004,Ca_element013]
  conduct = 2
  density = 1
  expand = 3
  formula = G4_M3_WAX
  name = G4_M3_WAX
  specific = 4
FEATURE [App::DocumentObjectGroupPython] Mg_element005  label="Mg_element : 1"  # scripted group (container) (typed FeaturePython)
  n = 1
  ref = Mg_element
FEATURE [App::DocumentObjectGroupPython] C_element058  label="C_element : 031"  # scripted group (container) (typed FeaturePython)
  n = 1
  ref = C_element
FEATURE [App::DocumentObjectGroupPython] O_element059  label="O_element : 030"  # scripted group (container) (typed FeaturePython)
  n = 3
  ref = O_element
FEATURE [App::DocumentObjectGroupPython] G4_MAGNESIUM_CARBONATE  # scripted group (container) (typed FeaturePython)
  Dunit = g/cm3
  Dvalue = 2.958
  Group = -> [Mg_element005,C_element058,O_element059]
  conduct = 2
  density = 1
  expand = 3
  formula = G4_MAGNESIUM_CARBONATE
  name = G4_MAGNESIUM_CARBONATE
  specific = 4
FEATURE [App::DocumentObjectGroupPython] Mg_element006  label="Mg_element : 002"  # scripted group (container) (typed FeaturePython)
  n = 1
  ref = Mg_element
FEATURE [App::DocumentObjectGroupPython] F_element013  label="F_element : 005"  # scripted group (container) (typed FeaturePython)
  n = 2
  ref = F_element
FEATURE [App::DocumentObjectGroupPython] G4_MAGNESIUM_FLUORIDE  # scripted group (container) (typed FeaturePython)
  Dunit = g/cm3
  Dvalue = 3
  Group = -> [Mg_element006,F_element013]
  conduct = 2
  density = 1
  expand = 3
  formula = G4_MAGNESIUM_FLUORIDE
  name = G4_MAGNESIUM_FLUORIDE
  specific = 4
FEATURE [App::DocumentObjectGroupPython] Mg_element007  label="Mg_element : 003"  # scripted group (container) (typed FeaturePython)
  n = 1
  ref = Mg_element
FEATURE [App::DocumentObjectGroupPython] O_element060  label="O_element : 031"  # scripted group (container) (typed FeaturePython)
  n = 1
  ref = O_element
FEATURE [App::DocumentObjectGroupPython] G4_MAGNESIUM_OXIDE  # scripted group (container) (typed FeaturePython)
  Dunit = g/cm3
  Dvalue = 3.58
  Group = -> [Mg_element007,O_element060]
  conduct = 2
  density = 1
  expand = 3
  formula = G4_MAGNESIUM_OXIDE
  name = G4_MAGNESIUM_OXIDE
  specific = 4
FEATURE [App::DocumentObjectGroupPython] Mg_element008  label="Mg_element : 004"  # scripted group (container) (typed FeaturePython)
  n = 1
  ref = Mg_element
FEATURE [App::DocumentObjectGroupPython] B_element006  label="B_element : 006"  # scripted group (container) (typed FeaturePython)
  n = 4
  ref = B_element
FEATURE [App::DocumentObjectGroupPython] O_element061  label="O_element : 032"  # scripted group (container) (typed FeaturePython)
  n = 7
  ref = O_element
FEATURE [App::DocumentObjectGroupPython] G4_MAGNESIUM_TETRABORATE  # scripted group (container) (typed FeaturePython)
  Dunit = g/cm3
  Dvalue = 2.53
  Group = -> [Mg_element008,B_element006,O_element061]
  conduct = 2
  density = 1
  expand = 3
  formula = G4_MAGNESIUM_TETRABORATE
  name = G4_MAGNESIUM_TETRABORATE
  specific = 4
FEATURE [App::DocumentObjectGroupPython] Hg_element001  label="Hg_element : 1"  # scripted group (container) (typed FeaturePython)
  n = 1
  ref = Hg_element
FEATURE [App::DocumentObjectGroupPython] I_element004  label="I_element : 2"  # scripted group (container) (typed FeaturePython)
  n = 2
  ref = I_element
FEATURE [App::DocumentObjectGroupPython] G4_MERCURIC_IODIDE  # scripted group (container) (typed FeaturePython)
  Dunit = g/cm3
  Dvalue = 6.36
  Group = -> [Hg_element001,I_element004]
  conduct = 2
  density = 1
  expand = 3
  formula = G4_MERCURIC_IODIDE
  name = G4_MERCURIC_IODIDE
  specific = 4
FEATURE [App::DocumentObjectGroupPython] C_element059  label="C_element : 032"  # scripted group (container) (typed FeaturePython)
  n = 1
  ref = C_element
FEATURE [App::DocumentObjectGroupPython] H_element053  label="H_element : 028"  # scripted group (container) (typed FeaturePython)
  n = 4
  ref = H_element
FEATURE [App::DocumentObjectGroupPython] G4_METHANE  # scripted group (container) (typed FeaturePython)
  Dunit = g/cm3
  Dvalue = 0.000667151
  Group = -> [C_element059,H_element053]
  conduct = 2
  density = 1
  expand = 3
  formula = G4_METHANE
  name = G4_METHANE
  specific = 4
FEATURE [App::DocumentObjectGroupPython] C_element060  label="C_element : 033"  # scripted group (container) (typed FeaturePython)
  n = 1
  ref = C_element
FEATURE [App::DocumentObjectGroupPython] H_element054  label="H_element : 029"  # scripted group (container) (typed FeaturePython)
  n = 4
  ref = H_element
FEATURE [App::DocumentObjectGroupPython] O_element062  label="O_element : 033"  # scripted group (container) (typed FeaturePython)
  n = 1
  ref = O_element
FEATURE [App::DocumentObjectGroupPython] G4_METHANOL  # scripted group (container) (typed FeaturePython)
  Dunit = g/cm3
  Dvalue = 0.7914
  Group = -> [C_element060,H_element054,O_element062]
  conduct = 2
  density = 1
  expand = 3
  formula = G4_METHANOL
  name = G4_METHANOL
  specific = 4
FEATURE [App::DocumentObjectGroupPython] H_element055  label="H_element : 0.134"  # scripted group (container) (typed FeaturePython)
  n = 0.13404
FEATURE [App::DocumentObjectGroupPython] C_element061  label="C_element : 0.778"  # scripted group (container) (typed FeaturePython)
  n = 0.77796
FEATURE [App::DocumentObjectGroupPython] O_element063  label="O_element : 0.035"  # scripted group (container) (typed FeaturePython)
  n = 0.03502
FEATURE [App::DocumentObjectGroupPython] Mg_element009  label="Mg_element : 0.039"  # scripted group (container) (typed FeaturePython)
  n = 0.038594
FEATURE [App::DocumentObjectGroupPython] Ti_element002  label="Ti_element : 0.014"  # scripted group (container) (typed FeaturePython)
  n = 0.014386
FEATURE [App::DocumentObjectGroupPython] G4_MIX_D_WAX  # scripted group (container) (typed FeaturePython)
  Dunit = g/cm3
  Dvalue = 0.99
  Group = -> [H_element055,C_element061,O_element063,Mg_element009,Ti_element002]
  conduct = 2
  density = 1
  expand = 3
  formula = G4_MIX_D_WAX
  name = G4_MIX_D_WAX
  specific = 4
FEATURE [App::DocumentObjectGroupPython] H_element056  label="H_element : 0.135"  # scripted group (container) (typed FeaturePython)
  n = 0.081192
FEATURE [App::DocumentObjectGroupPython] C_element062  label="C_element : 0.583"  # scripted group (container) (typed FeaturePython)
  n = 0.583442
FEATURE [App::DocumentObjectGroupPython] N_element024  label="N_element : 0.018"  # scripted group (container) (typed FeaturePython)
  n = 0.017798
FEATURE [App::DocumentObjectGroupPython] O_element064  label="O_element : 0.186"  # scripted group (container) (typed FeaturePython)
  n = 0.186381
FEATURE [App::DocumentObjectGroupPython] Mg_element010  label="Mg_element : 0.130"  # scripted group (container) (typed FeaturePython)
  n = 0.130287
FEATURE [App::DocumentObjectGroupPython] Cl_element015  label="Cl_element : 0.588"  # scripted group (container) (typed FeaturePython)
  n = 0.0009
FEATURE [App::DocumentObjectGroupPython] G4_MS20_TISSUE  # scripted group (container) (typed FeaturePython)
  Dunit = g/cm3
  Dvalue = 1
  Group = -> [H_element056,C_element062,N_element024,O_element064,Mg_element010,Cl_element015]
  conduct = 2
  density = 1
  expand = 3
  formula = G4_MS20_TISSUE
  name = G4_MS20_TISSUE
  specific = 4
FEATURE [App::DocumentObjectGroupPython] H_element057  label="H_element : 0.136"  # scripted group (container) (typed FeaturePython)
  n = 0.102
FEATURE [App::DocumentObjectGroupPython] C_element063  label="C_element : 0.143"  # scripted group (container) (typed FeaturePython)
  n = 0.143
FEATURE [App::DocumentObjectGroupPython] N_element025  label="N_element : 0.034"  # scripted group (container) (typed FeaturePython)
  n = 0.034
FEATURE [App::DocumentObjectGroupPython] O_element065  label="O_element : 0.710"  # scripted group (container) (typed FeaturePython)
  n = 0.71
FEATURE [App::DocumentObjectGroupPython] Na_element011  label="Na_element : 0.098"  # scripted group (container) (typed FeaturePython)
  n = 0.001
FEATURE [App::DocumentObjectGroupPython] P_element007  label="P_element : 0.002"  # scripted group (container) (typed FeaturePython)
  n = 0.002
FEATURE [App::DocumentObjectGroupPython] S_element017  label="S_element : 0.018"  # scripted group (container) (typed FeaturePython)
  n = 0.003
FEATURE [App::DocumentObjectGroupPython] Cl_element016  label="Cl_element : 0.589"  # scripted group (container) (typed FeaturePython)
  n = 0.001
FEATURE [App::DocumentObjectGroupPython] K_element006  label="K_element : 0.004"  # scripted group (container) (typed FeaturePython)
  n = 0.004
FEATURE [App::DocumentObjectGroupPython] G4_MUSCLE_SKELETAL_ICRP  # scripted group (container) (typed FeaturePython)
  Dunit = g/cm3
  Dvalue = 1.05
  Group = -> [H_element057,C_element063,N_element025,O_element065,Na_element011,P_element007,S_element017,Cl_element016,K_element006]
  conduct = 2
  density = 1
  expand = 3
  formula = G4_MUSCLE_SKELETAL_ICRP
  name = G4_MUSCLE_SKELETAL_ICRP
  specific = 4
FEATURE [App::DocumentObjectGroupPython] H_element058  label="H_element : 0.137"  # scripted group (container) (typed FeaturePython)
  n = 0.102102
FEATURE [App::DocumentObjectGroupPython] C_element064  label="C_element : 0.123"  # scripted group (container) (typed FeaturePython)
  n = 0.123123
FEATURE [App::DocumentObjectGroupPython] N_element026  label="N_element : 0.756"  # scripted group (container) (typed FeaturePython)
  n = 0.035035
FEATURE [App::DocumentObjectGroupPython] O_element066  label="O_element : 0.730"  # scripted group (container) (typed FeaturePython)
  n = 0.72973
FEATURE [App::DocumentObjectGroupPython] Na_element012  label="Na_element : 0.099"  # scripted group (container) (typed FeaturePython)
  n = 0.001001
FEATURE [App::DocumentObjectGroupPython] P_element008  label="P_element : 0.106"  # scripted group (container) (typed FeaturePython)
  n = 0.002002
FEATURE [App::DocumentObjectGroupPython] S_element018  label="S_element : 0.019"  # scripted group (container) (typed FeaturePython)
  n = 0.004004
FEATURE [App::DocumentObjectGroupPython] K_element007  label="K_element : 0.016"  # scripted group (container) (typed FeaturePython)
  n = 0.003003
FEATURE [App::DocumentObjectGroupPython] G4_MUSCLE_STRIATED_ICRU  # scripted group (container) (typed FeaturePython)
  Dunit = g/cm3
  Dvalue = 1.04
  Group = -> [H_element058,C_element064,N_element026,O_element066,Na_element012,P_element008,S_element018,K_element007]
  conduct = 2
  density = 1
  expand = 3
  formula = G4_MUSCLE_STRIATED_ICRU
  name = G4_MUSCLE_STRIATED_ICRU
  specific = 4
FEATURE [App::DocumentObjectGroupPython] H_element059  label="H_element : 0.098"  # scripted group (container) (typed FeaturePython)
  n = 0.0982341
FEATURE [App::DocumentObjectGroupPython] C_element065  label="C_element : 0.156"  # scripted group (container) (typed FeaturePython)
  n = 0.156214
FEATURE [App::DocumentObjectGroupPython] N_element027  label="N_element : 0.757"  # scripted group (container) (typed FeaturePython)
  n = 0.035451
FEATURE [App::DocumentObjectGroupPython] O_element067  label="O_element : 0.880"  # scripted group (container) (typed FeaturePython)
  n = 0.710101
FEATURE [App::DocumentObjectGroupPython] G4_MUSCLE_WITH_SUCROSE  # scripted group (container) (typed FeaturePython)
  Dunit = g/cm3
  Dvalue = 1.11
  Group = -> [H_element059,C_element065,N_element027,O_element067]
  conduct = 2
  density = 1
  expand = 3
  formula = G4_MUSCLE_WITH_SUCROSE
  name = G4_MUSCLE_WITH_SUCROSE
  specific = 4
FEATURE [App::DocumentObjectGroupPython] H_element060  label="H_element : 0.138"  # scripted group (container) (typed FeaturePython)
  n = 0.101969
FEATURE [App::DocumentObjectGroupPython] C_element066  label="C_element : 0.120"  # scripted group (container) (typed FeaturePython)
  n = 0.120058
FEATURE [App::DocumentObjectGroupPython] N_element028  label="N_element : 0.758"  # scripted group (container) (typed FeaturePython)
  n = 0.035451
FEATURE [App::DocumentObjectGroupPython] O_element068  label="O_element : 0.743"  # scripted group (container) (typed FeaturePython)
  n = 0.742522
FEATURE [App::DocumentObjectGroupPython] G4_MUSCLE_WITHOUT_SUCROSE  # scripted group (container) (typed FeaturePython)
  Dunit = g/cm3
  Dvalue = 1.07
  Group = -> [H_element060,C_element066,N_element028,O_element068]
  conduct = 2
  density = 1
  expand = 3
  formula = G4_MUSCLE_WITHOUT_SUCROSE
  name = G4_MUSCLE_WITHOUT_SUCROSE
  specific = 4
FEATURE [App::DocumentObjectGroupPython] C_element067  label="C_element : 10"  # scripted group (container) (typed FeaturePython)
  n = 10
  ref = C_element
FEATURE [App::DocumentObjectGroupPython] H_element061  label="H_element : 030"  # scripted group (container) (typed FeaturePython)
  n = 8
  ref = H_element
FEATURE [App::DocumentObjectGroupPython] G4_NAPHTHALENE  # scripted group (container) (typed FeaturePython)
  Dunit = g/cm3
  Dvalue = 1.145
  Group = -> [C_element067,H_element061]
  conduct = 2
  density = 1
  expand = 3
  formula = G4_NAPHTHALENE
  name = G4_NAPHTHALENE
  specific = 4
FEATURE [App::DocumentObjectGroupPython] C_element068  label="C_element : 034"  # scripted group (container) (typed FeaturePython)
  n = 6
  ref = C_element
FEATURE [App::DocumentObjectGroupPython] H_element062  label="H_element : 031"  # scripted group (container) (typed FeaturePython)
  n = 5
  ref = H_element
FEATURE [App::DocumentObjectGroupPython] N_element029  label="N_element : 012"  # scripted group (container) (typed FeaturePython)
  n = 1
  ref = N_element
FEATURE [App::DocumentObjectGroupPython] O_element069  label="O_element : 034"  # scripted group (container) (typed FeaturePython)
  n = 2
  ref = O_element
FEATURE [App::DocumentObjectGroupPython] G4_NITROBENZENE  # scripted group (container) (typed FeaturePython)
  Dunit = g/cm3
  Dvalue = 1.19867
  Group = -> [C_element068,H_element062,N_element029,O_element069]
  conduct = 2
  density = 1
  expand = 3
  formula = G4_NITROBENZENE
  name = G4_NITROBENZENE
  specific = 4
FEATURE [App::DocumentObjectGroupPython] N_element030  label="N_element : 013"  # scripted group (container) (typed FeaturePython)
  n = 2
  ref = N_element
FEATURE [App::DocumentObjectGroupPython] O_element070  label="O_element : 035"  # scripted group (container) (typed FeaturePython)
  n = 1
  ref = O_element
FEATURE [App::DocumentObjectGroupPython] G4_NITROUS_OXIDE  # scripted group (container) (typed FeaturePython)
  Dunit = g/cm3
  Dvalue = 0.00183094
  Group = -> [N_element030,O_element070]
  conduct = 2
  density = 1
  expand = 3
  formula = G4_NITROUS_OXIDE
  name = G4_NITROUS_OXIDE
  specific = 4
FEATURE [App::DocumentObjectGroupPython] H_element063  label="H_element : 0.104"  # scripted group (container) (typed FeaturePython)
  n = 0.103509
FEATURE [App::DocumentObjectGroupPython] C_element069  label="C_element : 0.648"  # scripted group (container) (typed FeaturePython)
  n = 0.648416
FEATURE [App::DocumentObjectGroupPython] N_element031  label="N_element : 0.100"  # scripted group (container) (typed FeaturePython)
  n = 0.0995361
FEATURE [App::DocumentObjectGroupPython] O_element071  label="O_element : 0.149"  # scripted group (container) (typed FeaturePython)
  n = 0.148539
FEATURE [App::DocumentObjectGroupPython] G4_NYLON_8062  label="G4_NYLON-8062"  # scripted group (container) (typed FeaturePython)
  Dunit = g/cm3
  Dvalue = 1.08
  Group = -> [H_element063,C_element069,N_element031,O_element071]
  conduct = 2
  density = 1
  expand = 3
  formula = G4_NYLON-8062
  name = G4_NYLON-8062
  specific = 4
FEATURE [App::DocumentObjectGroupPython] C_element070  label="C_element : 035"  # scripted group (container) (typed FeaturePython)
  n = 6
  ref = C_element
FEATURE [App::DocumentObjectGroupPython] H_element064  label="H_element : 11"  # scripted group (container) (typed FeaturePython)
  n = 11
  ref = H_element
FEATURE [App::DocumentObjectGroupPython] N_element032  label="N_element : 014"  # scripted group (container) (typed FeaturePython)
  n = 1
  ref = N_element
FEATURE [App::DocumentObjectGroupPython] O_element072  label="O_element : 036"  # scripted group (container) (typed FeaturePython)
  n = 1
  ref = O_element
FEATURE [App::DocumentObjectGroupPython] G4_NYLON_6_6  label="G4_NYLON-6-6"  # scripted group (container) (typed FeaturePython)
  Dunit = g/cm3
  Dvalue = 1.14
  Group = -> [C_element070,H_element064,N_element032,O_element072]
  conduct = 2
  density = 1
  expand = 3
  formula = G4_NYLON-6-6
  name = G4_NYLON-6-6
  specific = 4
FEATURE [App::DocumentObjectGroupPython] H_element065  label="H_element : 0.139"  # scripted group (container) (typed FeaturePython)
  n = 0.107062
FEATURE [App::DocumentObjectGroupPython] C_element071  label="C_element : 0.680"  # scripted group (container) (typed FeaturePython)
  n = 0.680449
FEATURE [App::DocumentObjectGroupPython] N_element033  label="N_element : 0.099"  # scripted group (container) (typed FeaturePython)
  n = 0.099189
FEATURE [App::DocumentObjectGroupPython] O_element073  label="O_element : 0.113"  # scripted group (container) (typed FeaturePython)
  n = 0.1133
FEATURE [App::DocumentObjectGroupPython] G4_NYLON_6_10  label="G4_NYLON-6-10"  # scripted group (container) (typed FeaturePython)
  Dunit = g/cm3
  Dvalue = 1.14
  Group = -> [H_element065,C_element071,N_element033,O_element073]
  conduct = 2
  density = 1
  expand = 3
  formula = G4_NYLON-6-10
  name = G4_NYLON-6-10
  specific = 4
FEATURE [App::DocumentObjectGroupPython] H_element066  label="H_element : 0.140"  # scripted group (container) (typed FeaturePython)
  n = 0.115476
FEATURE [App::DocumentObjectGroupPython] C_element072  label="C_element : 0.721"  # scripted group (container) (typed FeaturePython)
  n = 0.720818
FEATURE [App::DocumentObjectGroupPython] N_element034  label="N_element : 0.076"  # scripted group (container) (typed FeaturePython)
  n = 0.0764169
FEATURE [App::DocumentObjectGroupPython] O_element074  label="O_element : 0.087"  # scripted group (container) (typed FeaturePython)
  n = 0.0872889
FEATURE [App::DocumentObjectGroupPython] G4_NYLON_11_RILSAN  label="G4_NYLON-11_RILSAN"  # scripted group (container) (typed FeaturePython)
  Dunit = g/cm3
  Dvalue = 1.425
  Group = -> [H_element066,C_element072,N_element034,O_element074]
  conduct = 2
  density = 1
  expand = 3
  formula = G4_NYLON-11_RILSAN
  name = G4_NYLON-11_RILSAN
  specific = 4
FEATURE [App::DocumentObjectGroupPython] C_element073  label="C_element : 8"  # scripted group (container) (typed FeaturePython)
  n = 8
  ref = C_element
FEATURE [App::DocumentObjectGroupPython] H_element067  label="H_element : 18"  # scripted group (container) (typed FeaturePython)
  n = 18
  ref = H_element
FEATURE [App::DocumentObjectGroupPython] G4_OCTANE  # scripted group (container) (typed FeaturePython)
  Dunit = g/cm3
  Dvalue = 0.7026
  Group = -> [C_element073,H_element067]
  conduct = 2
  density = 1
  expand = 3
  formula = G4_OCTANE
  name = G4_OCTANE
  specific = 4
FEATURE [App::DocumentObjectGroupPython] C_element074  label="C_element : 25"  # scripted group (container) (typed FeaturePython)
  n = 25
  ref = C_element
FEATURE [App::DocumentObjectGroupPython] H_element068  label="H_element : 52"  # scripted group (container) (typed FeaturePython)
  n = 52
  ref = H_element
FEATURE [App::DocumentObjectGroupPython] G4_PARAFFIN  # scripted group (container) (typed FeaturePython)
  Dunit = g/cm3
  Dvalue = 0.93
  Group = -> [C_element074,H_element068]
  conduct = 2
  density = 1
  expand = 3
  formula = G4_PARAFFIN
  name = G4_PARAFFIN
  specific = 4
FEATURE [App::DocumentObjectGroupPython] C_element075  label="C_element : 036"  # scripted group (container) (typed FeaturePython)
  n = 5
  ref = C_element
FEATURE [App::DocumentObjectGroupPython] H_element069  label="H_element : 032"  # scripted group (container) (typed FeaturePython)
  n = 12
  ref = H_element
FEATURE [App::DocumentObjectGroupPython] G4_N_PENTANE  label="G4_N-PENTANE"  # scripted group (container) (typed FeaturePython)
  Dunit = g/cm3
  Dvalue = 0.6262
  Group = -> [C_element075,H_element069]
  conduct = 2
  density = 1
  expand = 3
  formula = G4_N-PENTANE
  name = G4_N-PENTANE
  specific = 4
FEATURE [App::DocumentObjectGroupPython] H_element070  label="H_element : 0.014"  # scripted group (container) (typed FeaturePython)
  n = 0.0141
FEATURE [App::DocumentObjectGroupPython] C_element076  label="C_element : 0.072"  # scripted group (container) (typed FeaturePython)
  n = 0.072261
FEATURE [App::DocumentObjectGroupPython] N_element035  label="N_element : 0.019"  # scripted group (container) (typed FeaturePython)
  n = 0.01932
FEATURE [App::DocumentObjectGroupPython] O_element075  label="O_element : 0.066"  # scripted group (container) (typed FeaturePython)
  n = 0.066101
FEATURE [App::DocumentObjectGroupPython] S_element019  label="S_element : 0.020"  # scripted group (container) (typed FeaturePython)
  n = 0.00189
FEATURE [App::DocumentObjectGroupPython] Br_element004  label="Br_element : 0.349"  # scripted group (container) (typed FeaturePython)
  n = 0.349103
FEATURE [App::DocumentObjectGroupPython] Ag_element001  label="Ag_element : 0.474"  # scripted group (container) (typed FeaturePython)
  n = 0.474105
FEATURE [App::DocumentObjectGroupPython] I_element005  label="I_element : 0.003"  # scripted group (container) (typed FeaturePython)
  n = 0.00312
FEATURE [App::DocumentObjectGroupPython] G4_PHOTO_EMULSION  # scripted group (container) (typed FeaturePython)
  Dunit = g/cm3
  Dvalue = 3.815
  Group = -> [H_element070,C_element076,N_element035,O_element075,S_element019,Br_element004,Ag_element001,I_element005]
  conduct = 2
  density = 1
  expand = 3
  formula = G4_PHOTO_EMULSION
  name = G4_PHOTO_EMULSION
  specific = 4
FEATURE [App::DocumentObjectGroupPython] C_element077  label="C_element : 9"  # scripted group (container) (typed FeaturePython)
  n = 9
  ref = C_element
FEATURE [App::DocumentObjectGroupPython] H_element071  label="H_element : 033"  # scripted group (container) (typed FeaturePython)
  n = 10
  ref = H_element
FEATURE [App::DocumentObjectGroupPython] G4_PLASTIC_SC_VINYLTOLUENE  # scripted group (container) (typed FeaturePython)
  Dunit = g/cm3
  Dvalue = 1.032
  Group = -> [C_element077,H_element071]
  conduct = 2
  density = 1
  expand = 3
  formula = G4_PLASTIC_SC_VINYLTOLUENE
  name = G4_PLASTIC_SC_VINYLTOLUENE
  specific = 4
FEATURE [App::DocumentObjectGroupPython] Pu_element001  label="Pu_element : 1"  # scripted group (container) (typed FeaturePython)
  n = 1
  ref = Pu_element
FEATURE [App::DocumentObjectGroupPython] O_element076  label="O_element : 037"  # scripted group (container) (typed FeaturePython)
  n = 2
  ref = O_element
FEATURE [App::DocumentObjectGroupPython] G4_PLUTONIUM_DIOXIDE  # scripted group (container) (typed FeaturePython)
  Dunit = g/cm3
  Dvalue = 11.46
  Group = -> [Pu_element001,O_element076]
  conduct = 2
  density = 1
  expand = 3
  formula = G4_PLUTONIUM_DIOXIDE
  name = G4_PLUTONIUM_DIOXIDE
  specific = 4
FEATURE [App::DocumentObjectGroupPython] C_element078  label="C_element : 037"  # scripted group (container) (typed FeaturePython)
  n = 3
  ref = C_element
FEATURE [App::DocumentObjectGroupPython] H_element072  label="H_element : 034"  # scripted group (container) (typed FeaturePython)
  n = 3
  ref = H_element
FEATURE [App::DocumentObjectGroupPython] N_element036  label="N_element : 015"  # scripted group (container) (typed FeaturePython)
  n = 1
  ref = N_element
FEATURE [App::DocumentObjectGroupPython] G4_POLYACRYLONITRILE  # scripted group (container) (typed FeaturePython)
  Dunit = g/cm3
  Dvalue = 1.17
  Group = -> [C_element078,H_element072,N_element036]
  conduct = 2
  density = 1
  expand = 3
  formula = G4_POLYACRYLONITRILE
  name = G4_POLYACRYLONITRILE
  specific = 4
FEATURE [App::DocumentObjectGroupPython] C_element079  label="C_element : 16"  # scripted group (container) (typed FeaturePython)
  n = 16
  ref = C_element
FEATURE [App::DocumentObjectGroupPython] H_element073  label="H_element : 035"  # scripted group (container) (typed FeaturePython)
  n = 14
  ref = H_element
FEATURE [App::DocumentObjectGroupPython] O_element077  label="O_element : 038"  # scripted group (container) (typed FeaturePython)
  n = 3
  ref = O_element
FEATURE [App::DocumentObjectGroupPython] G4_POLYCARBONATE  # scripted group (container) (typed FeaturePython)
  Dunit = g/cm3
  Dvalue = 1.2
  Group = -> [C_element079,H_element073,O_element077]
  conduct = 2
  density = 1
  expand = 3
  formula = G4_POLYCARBONATE
  name = G4_POLYCARBONATE
  specific = 4
FEATURE [App::DocumentObjectGroupPython] C_element080  label="C_element : 038"  # scripted group (container) (typed FeaturePython)
  n = 8
  ref = C_element
FEATURE [App::DocumentObjectGroupPython] H_element074  label="H_element : 036"  # scripted group (container) (typed FeaturePython)
  n = 7
  ref = H_element
FEATURE [App::DocumentObjectGroupPython] Cl_element017  label="Cl_element : 007"  # scripted group (container) (typed FeaturePython)
  n = 1
  ref = Cl_element
FEATURE [App::DocumentObjectGroupPython] G4_POLYCHLOROSTYRENE  # scripted group (container) (typed FeaturePython)
  Dunit = g/cm3
  Dvalue = 1.3
  Group = -> [C_element080,H_element074,Cl_element017]
  conduct = 2
  density = 1
  expand = 3
  formula = G4_POLYCHLOROSTYRENE
  name = G4_POLYCHLOROSTYRENE
  specific = 4
FEATURE [App::DocumentObjectGroupPython] C_element081  label="C_element : 039"  # scripted group (container) (typed FeaturePython)
  n = 1
  ref = C_element
FEATURE [App::DocumentObjectGroupPython] H_element075  label="H_element : 037"  # scripted group (container) (typed FeaturePython)
  n = 2
  ref = H_element
FEATURE [App::DocumentObjectGroupPython] G4_POLYETHYLENE  # scripted group (container) (typed FeaturePython)
  Dunit = g/cm3
  Dvalue = 0.94
  Group = -> [C_element081,H_element075]
  conduct = 2
  density = 1
  expand = 3
  formula = G4_POLYETHYLENE
  name = G4_POLYETHYLENE
  specific = 4
FEATURE [App::DocumentObjectGroupPython] C_element082  label="C_element : 040"  # scripted group (container) (typed FeaturePython)
  n = 10
  ref = C_element
FEATURE [App::DocumentObjectGroupPython] H_element076  label="H_element : 038"  # scripted group (container) (typed FeaturePython)
  n = 8
  ref = H_element
FEATURE [App::DocumentObjectGroupPython] O_element078  label="O_element : 039"  # scripted group (container) (typed FeaturePython)
  n = 4
  ref = O_element
FEATURE [App::DocumentObjectGroupPython] G4_MYLAR  # scripted group (container) (typed FeaturePython)
  Dunit = g/cm3
  Dvalue = 1.4
  Group = -> [C_element082,H_element076,O_element078]
  conduct = 2
  density = 1
  expand = 3
  formula = G4_MYLAR
  name = G4_MYLAR
  specific = 4
FEATURE [App::DocumentObjectGroupPython] C_element083  label="C_element : 041"  # scripted group (container) (typed FeaturePython)
  n = 5
  ref = C_element
FEATURE [App::DocumentObjectGroupPython] H_element077  label="H_element : 039"  # scripted group (container) (typed FeaturePython)
  n = 8
  ref = H_element
FEATURE [App::DocumentObjectGroupPython] O_element079  label="O_element : 040"  # scripted group (container) (typed FeaturePython)
  n = 2
  ref = O_element
FEATURE [App::DocumentObjectGroupPython] G4_PLEXIGLASS  # scripted group (container) (typed FeaturePython)
  Dunit = g/cm3
  Dvalue = 1.19
  Group = -> [C_element083,H_element077,O_element079]
  conduct = 2
  density = 1
  expand = 3
  formula = G4_PLEXIGLASS
  name = G4_PLEXIGLASS
  specific = 4
FEATURE [App::DocumentObjectGroupPython] C_element084  label="C_element : 042"  # scripted group (container) (typed FeaturePython)
  n = 1
  ref = C_element
FEATURE [App::DocumentObjectGroupPython] H_element078  label="H_element : 040"  # scripted group (container) (typed FeaturePython)
  n = 2
  ref = H_element
FEATURE [App::DocumentObjectGroupPython] O_element080  label="O_element : 041"  # scripted group (container) (typed FeaturePython)
  n = 1
  ref = O_element
FEATURE [App::DocumentObjectGroupPython] G4_POLYOXYMETHYLENE  # scripted group (container) (typed FeaturePython)
  Dunit = g/cm3
  Dvalue = 1.425
  Group = -> [C_element084,H_element078,O_element080]
  conduct = 2
  density = 1
  expand = 3
  formula = G4_POLYOXYMETHYLENE
  name = G4_POLYOXYMETHYLENE
  specific = 4
FEATURE [App::DocumentObjectGroupPython] C_element085  label="C_element : 043"  # scripted group (container) (typed FeaturePython)
  n = 2
  ref = C_element
FEATURE [App::DocumentObjectGroupPython] H_element079  label="H_element : 041"  # scripted group (container) (typed FeaturePython)
  n = 4
  ref = H_element
FEATURE [App::DocumentObjectGroupPython] G4_POLYPROPYLENE  # scripted group (container) (typed FeaturePython)
  Dunit = g/cm3
  Dvalue = 0.9
  Group = -> [C_element085,H_element079]
  conduct = 2
  density = 1
  expand = 3
  formula = G4_POLYPROPYLENE
  name = G4_POLYPROPYLENE
  specific = 4
FEATURE [App::DocumentObjectGroupPython] C_element086  label="C_element : 044"  # scripted group (container) (typed FeaturePython)
  n = 8
  ref = C_element
FEATURE [App::DocumentObjectGroupPython] H_element080  label="H_element : 042"  # scripted group (container) (typed FeaturePython)
  n = 8
  ref = H_element
FEATURE [App::DocumentObjectGroupPython] G4_POLYSTYRENE  # scripted group (container) (typed FeaturePython)
  Dunit = g/cm3
  Dvalue = 1.06
  Group = -> [C_element086,H_element080]
  conduct = 2
  density = 1
  expand = 3
  formula = G4_POLYSTYRENE
  name = G4_POLYSTYRENE
  specific = 4
FEATURE [App::DocumentObjectGroupPython] C_element087  label="C_element : 045"  # scripted group (container) (typed FeaturePython)
  n = 2
  ref = C_element
FEATURE [App::DocumentObjectGroupPython] F_element014  label="F_element : 4"  # scripted group (container) (typed FeaturePython)
  n = 4
  ref = F_element
FEATURE [App::DocumentObjectGroupPython] G4_TEFLON  # scripted group (container) (typed FeaturePython)
  Dunit = g/cm3
  Dvalue = 2.2
  Group = -> [C_element087,F_element014]
  conduct = 2
  density = 1
  expand = 3
  formula = G4_TEFLON
  name = G4_TEFLON
  specific = 4
FEATURE [App::DocumentObjectGroupPython] C_element088  label="C_element : 046"  # scripted group (container) (typed FeaturePython)
  n = 2
  ref = C_element
FEATURE [App::DocumentObjectGroupPython] F_element015  label="F_element : 006"  # scripted group (container) (typed FeaturePython)
  n = 3
  ref = F_element
FEATURE [App::DocumentObjectGroupPython] Cl_element018  label="Cl_element : 008"  # scripted group (container) (typed FeaturePython)
  n = 1
  ref = Cl_element
FEATURE [App::DocumentObjectGroupPython] G4_POLYTRIFLUOROCHLOROETHYLENE  # scripted group (container) (typed FeaturePython)
  Dunit = g/cm3
  Dvalue = 2.1
  Group = -> [C_element088,F_element015,Cl_element018]
  conduct = 2
  density = 1
  expand = 3
  formula = G4_POLYTRIFLUOROCHLOROETHYLENE
  name = G4_POLYTRIFLUOROCHLOROETHYLENE
  specific = 4
FEATURE [App::DocumentObjectGroupPython] C_element089  label="C_element : 047"  # scripted group (container) (typed FeaturePython)
  n = 4
  ref = C_element
FEATURE [App::DocumentObjectGroupPython] H_element081  label="H_element : 043"  # scripted group (container) (typed FeaturePython)
  n = 6
  ref = H_element
FEATURE [App::DocumentObjectGroupPython] O_element081  label="O_element : 042"  # scripted group (container) (typed FeaturePython)
  n = 2
  ref = O_element
FEATURE [App::DocumentObjectGroupPython] G4_POLYVINYL_ACETATE  # scripted group (container) (typed FeaturePython)
  Dunit = g/cm3
  Dvalue = 1.19
  Group = -> [C_element089,H_element081,O_element081]
  conduct = 2
  density = 1
  expand = 3
  formula = G4_POLYVINYL_ACETATE
  name = G4_POLYVINYL_ACETATE
  specific = 4
FEATURE [App::DocumentObjectGroupPython] C_element090  label="C_element : 048"  # scripted group (container) (typed FeaturePython)
  n = 2
  ref = C_element
FEATURE [App::DocumentObjectGroupPython] H_element082  label="H_element : 044"  # scripted group (container) (typed FeaturePython)
  n = 4
  ref = H_element
FEATURE [App::DocumentObjectGroupPython] O_element082  label="O_element : 043"  # scripted group (container) (typed FeaturePython)
  n = 1
  ref = O_element
FEATURE [App::DocumentObjectGroupPython] G4_POLYVINYL_ALCOHOL  # scripted group (container) (typed FeaturePython)
  Dunit = g/cm3
  Dvalue = 1.3
  Group = -> [C_element090,H_element082,O_element082]
  conduct = 2
  density = 1
  expand = 3
  formula = G4_POLYVINYL_ALCOHOL
  name = G4_POLYVINYL_ALCOHOL
  specific = 4
FEATURE [App::DocumentObjectGroupPython] C_element091  label="C_element : 049"  # scripted group (container) (typed FeaturePython)
  n = 8
  ref = C_element
FEATURE [App::DocumentObjectGroupPython] H_element083  label="H_element : 045"  # scripted group (container) (typed FeaturePython)
  n = 14
  ref = H_element
FEATURE [App::DocumentObjectGroupPython] O_element083  label="O_element : 044"  # scripted group (container) (typed FeaturePython)
  n = 2
  ref = O_element
FEATURE [App::DocumentObjectGroupPython] G4_POLYVINYL_BUTYRAL  # scripted group (container) (typed FeaturePython)
  Dunit = g/cm3
  Dvalue = 1.12
  Group = -> [C_element091,H_element083,O_element083]
  conduct = 2
  density = 1
  expand = 3
  formula = G4_POLYVINYL_BUTYRAL
  name = G4_POLYVINYL_BUTYRAL
  specific = 4
FEATURE [App::DocumentObjectGroupPython] C_element092  label="C_element : 050"  # scripted group (container) (typed FeaturePython)
  n = 2
  ref = C_element
FEATURE [App::DocumentObjectGroupPython] H_element084  label="H_element : 046"  # scripted group (container) (typed FeaturePython)
  n = 3
  ref = H_element
FEATURE [App::DocumentObjectGroupPython] Cl_element019  label="Cl_element : 009"  # scripted group (container) (typed FeaturePython)
  n = 1
  ref = Cl_element
FEATURE [App::DocumentObjectGroupPython] G4_POLYVINYL_CHLORIDE  # scripted group (container) (typed FeaturePython)
  Dunit = g/cm3
  Dvalue = 1.3
  Group = -> [C_element092,H_element084,Cl_element019]
  conduct = 2
  density = 1
  expand = 3
  formula = G4_POLYVINYL_CHLORIDE
  name = G4_POLYVINYL_CHLORIDE
  specific = 4
FEATURE [App::DocumentObjectGroupPython] C_element093  label="C_element : 051"  # scripted group (container) (typed FeaturePython)
  n = 2
  ref = C_element
FEATURE [App::DocumentObjectGroupPython] H_element085  label="H_element : 047"  # scripted group (container) (typed FeaturePython)
  n = 2
  ref = H_element
FEATURE [App::DocumentObjectGroupPython] Cl_element020  label="Cl_element : 010"  # scripted group (container) (typed FeaturePython)
  n = 2
  ref = Cl_element
FEATURE [App::DocumentObjectGroupPython] G4_POLYVINYLIDENE_CHLORIDE  # scripted group (container) (typed FeaturePython)
  Dunit = g/cm3
  Dvalue = 1.7
  Group = -> [C_element093,H_element085,Cl_element020]
  conduct = 2
  density = 1
  expand = 3
  formula = G4_POLYVINYLIDENE_CHLORIDE
  name = G4_POLYVINYLIDENE_CHLORIDE
  specific = 4
FEATURE [App::DocumentObjectGroupPython] C_element094  label="C_element : 052"  # scripted group (container) (typed FeaturePython)
  n = 2
  ref = C_element
FEATURE [App::DocumentObjectGroupPython] H_element086  label="H_element : 048"  # scripted group (container) (typed FeaturePython)
  n = 2
  ref = H_element
FEATURE [App::DocumentObjectGroupPython] F_element016  label="F_element : 007"  # scripted group (container) (typed FeaturePython)
  n = 2
  ref = F_element
FEATURE [App::DocumentObjectGroupPython] G4_POLYVINYLIDENE_FLUORIDE  # scripted group (container) (typed FeaturePython)
  Dunit = g/cm3
  Dvalue = 1.76
  Group = -> [C_element094,H_element086,F_element016]
  conduct = 2
  density = 1
  expand = 3
  formula = G4_POLYVINYLIDENE_FLUORIDE
  name = G4_POLYVINYLIDENE_FLUORIDE
  specific = 4
FEATURE [App::DocumentObjectGroupPython] C_element095  label="C_element : 053"  # scripted group (container) (typed FeaturePython)
  n = 6
  ref = C_element
FEATURE [App::DocumentObjectGroupPython] H_element087  label="H_element : 9"  # scripted group (container) (typed FeaturePython)
  n = 9
  ref = H_element
FEATURE [App::DocumentObjectGroupPython] N_element037  label="N_element : 016"  # scripted group (container) (typed FeaturePython)
  n = 1
  ref = N_element
FEATURE [App::DocumentObjectGroupPython] O_element084  label="O_element : 045"  # scripted group (container) (typed FeaturePython)
  n = 1
  ref = O_element
FEATURE [App::DocumentObjectGroupPython] G4_POLYVINYL_PYRROLIDONE  # scripted group (container) (typed FeaturePython)
  Dunit = g/cm3
  Dvalue = 1.25
  Group = -> [C_element095,H_element087,N_element037,O_element084]
  conduct = 2
  density = 1
  expand = 3
  formula = G4_POLYVINYL_PYRROLIDONE
  name = G4_POLYVINYL_PYRROLIDONE
  specific = 4
FEATURE [App::DocumentObjectGroupPython] K_element008  label="K_element : 1"  # scripted group (container) (typed FeaturePython)
  n = 1
  ref = K_element
FEATURE [App::DocumentObjectGroupPython] I_element006  label="I_element : 003"  # scripted group (container) (typed FeaturePython)
  n = 1
  ref = I_element
FEATURE [App::DocumentObjectGroupPython] G4_POTASSIUM_IODIDE  # scripted group (container) (typed FeaturePython)
  Dunit = g/cm3
  Dvalue = 3.13
  Group = -> [K_element008,I_element006]
  conduct = 2
  density = 1
  expand = 3
  formula = G4_POTASSIUM_IODIDE
  name = G4_POTASSIUM_IODIDE
  specific = 4
FEATURE [App::DocumentObjectGroupPython] K_element009  label="K_element : 2"  # scripted group (container) (typed FeaturePython)
  n = 2
  ref = K_element
FEATURE [App::DocumentObjectGroupPython] O_element085  label="O_element : 046"  # scripted group (container) (typed FeaturePython)
  n = 1
  ref = O_element
FEATURE [App::DocumentObjectGroupPython] G4_POTASSIUM_OXIDE  # scripted group (container) (typed FeaturePython)
  Dunit = g/cm3
  Dvalue = 2.32
  Group = -> [K_element009,O_element085]
  conduct = 2
  density = 1
  expand = 3
  formula = G4_POTASSIUM_OXIDE
  name = G4_POTASSIUM_OXIDE
  specific = 4
FEATURE [App::DocumentObjectGroupPython] C_element096  label="C_element : 054"  # scripted group (container) (typed FeaturePython)
  n = 3
  ref = C_element
FEATURE [App::DocumentObjectGroupPython] H_element088  label="H_element : 049"  # scripted group (container) (typed FeaturePython)
  n = 8
  ref = H_element
FEATURE [App::DocumentObjectGroupPython] G4_PROPANE  # scripted group (container) (typed FeaturePython)
  Dunit = g/cm3
  Dvalue = 0.00187939
  Group = -> [C_element096,H_element088]
  conduct = 2
  density = 1
  expand = 3
  formula = G4_PROPANE
  name = G4_PROPANE
  specific = 4
FEATURE [App::DocumentObjectGroupPython] C_element097  label="C_element : 055"  # scripted group (container) (typed FeaturePython)
  n = 3
  ref = C_element
FEATURE [App::DocumentObjectGroupPython] H_element089  label="H_element : 050"  # scripted group (container) (typed FeaturePython)
  n = 8
  ref = H_element
FEATURE [App::DocumentObjectGroupPython] G4_lPROPANE  # scripted group (container) (typed FeaturePython)
  Dunit = g/cm3
  Dvalue = 0.43
  Group = -> [C_element097,H_element089]
  conduct = 2
  density = 1
  expand = 3
  formula = G4_lPROPANE
  name = G4_lPROPANE
  specific = 4
FEATURE [App::DocumentObjectGroupPython] C_element098  label="C_element : 056"  # scripted group (container) (typed FeaturePython)
  n = 3
  ref = C_element
FEATURE [App::DocumentObjectGroupPython] H_element090  label="H_element : 051"  # scripted group (container) (typed FeaturePython)
  n = 8
  ref = H_element
FEATURE [App::DocumentObjectGroupPython] O_element086  label="O_element : 047"  # scripted group (container) (typed FeaturePython)
  n = 1
  ref = O_element
FEATURE [App::DocumentObjectGroupPython] G4_N_PROPYL_ALCOHOL  label="G4_N-PROPYL_ALCOHOL"  # scripted group (container) (typed FeaturePython)
  Dunit = g/cm3
  Dvalue = 0.8035
  Group = -> [C_element098,H_element090,O_element086]
  conduct = 2
  density = 1
  expand = 3
  formula = G4_N-PROPYL_ALCOHOL
  name = G4_N-PROPYL_ALCOHOL
  specific = 4
FEATURE [App::DocumentObjectGroupPython] C_element099  label="C_element : 057"  # scripted group (container) (typed FeaturePython)
  n = 5
  ref = C_element
FEATURE [App::DocumentObjectGroupPython] H_element091  label="H_element : 052"  # scripted group (container) (typed FeaturePython)
  n = 5
  ref = H_element
FEATURE [App::DocumentObjectGroupPython] N_element038  label="N_element : 017"  # scripted group (container) (typed FeaturePython)
  n = 1
  ref = N_element
FEATURE [App::DocumentObjectGroupPython] G4_PYRIDINE  # scripted group (container) (typed FeaturePython)
  Dunit = g/cm3
  Dvalue = 0.9819
  Group = -> [C_element099,H_element091,N_element038]
  conduct = 2
  density = 1
  expand = 3
  formula = G4_PYRIDINE
  name = G4_PYRIDINE
  specific = 4
FEATURE [App::DocumentObjectGroupPython] H_element092  label="H_element : 0.144"  # scripted group (container) (typed FeaturePython)
  n = 0.143711
FEATURE [App::DocumentObjectGroupPython] C_element100  label="C_element : 0.856"  # scripted group (container) (typed FeaturePython)
  n = 0.856289
FEATURE [App::DocumentObjectGroupPython] G4_RUBBER_BUTYL  # scripted group (container) (typed FeaturePython)
  Dunit = g/cm3
  Dvalue = 0.92
  Group = -> [H_element092,C_element100]
  conduct = 2
  density = 1
  expand = 3
  formula = G4_RUBBER_BUTYL
  name = G4_RUBBER_BUTYL
  specific = 4
FEATURE [App::DocumentObjectGroupPython] H_element093  label="H_element : 0.118"  # scripted group (container) (typed FeaturePython)
  n = 0.118371
FEATURE [App::DocumentObjectGroupPython] C_element101  label="C_element : 0.882"  # scripted group (container) (typed FeaturePython)
  n = 0.881629
FEATURE [App::DocumentObjectGroupPython] G4_RUBBER_NATURAL  # scripted group (container) (typed FeaturePython)
  Dunit = g/cm3
  Dvalue = 0.92
  Group = -> [H_element093,C_element101]
  conduct = 2
  density = 1
  expand = 3
  formula = G4_RUBBER_NATURAL
  name = G4_RUBBER_NATURAL
  specific = 4
FEATURE [App::DocumentObjectGroupPython] H_element094  label="H_element : 0.145"  # scripted group (container) (typed FeaturePython)
  n = 0.05692
FEATURE [App::DocumentObjectGroupPython] C_element102  label="C_element : 0.543"  # scripted group (container) (typed FeaturePython)
  n = 0.542646
FEATURE [App::DocumentObjectGroupPython] Cl_element021  label="Cl_element : 0.400"  # scripted group (container) (typed FeaturePython)
  n = 0.400434
FEATURE [App::DocumentObjectGroupPython] G4_RUBBER_NEOPRENE  # scripted group (container) (typed FeaturePython)
  Dunit = g/cm3
  Dvalue = 1.23
  Group = -> [H_element094,C_element102,Cl_element021]
  conduct = 2
  density = 1
  expand = 3
  formula = G4_RUBBER_NEOPRENE
  name = G4_RUBBER_NEOPRENE
  specific = 4
FEATURE [App::DocumentObjectGroupPython] Si_element006  label="Si_element : 1"  # scripted group (container) (typed FeaturePython)
  n = 1
  ref = Si_element
FEATURE [App::DocumentObjectGroupPython] O_element087  label="O_element : 048"  # scripted group (container) (typed FeaturePython)
  n = 2
  ref = O_element
FEATURE [App::DocumentObjectGroupPython] G4_SILICON_DIOXIDE  # scripted group (container) (typed FeaturePython)
  Dunit = g/cm3
  Dvalue = 2.32
  Group = -> [Si_element006,O_element087]
  conduct = 2
  density = 1
  expand = 3
  formula = G4_SILICON_DIOXIDE
  name = G4_SILICON_DIOXIDE
  specific = 4
FEATURE [App::DocumentObjectGroupPython] Ag_element002  label="Ag_element : 1"  # scripted group (container) (typed FeaturePython)
  n = 1
  ref = Ag_element
FEATURE [App::DocumentObjectGroupPython] Br_element005  label="Br_element : 003"  # scripted group (container) (typed FeaturePython)
  n = 1
  ref = Br_element
FEATURE [App::DocumentObjectGroupPython] G4_SILVER_BROMIDE  # scripted group (container) (typed FeaturePython)
  Dunit = g/cm3
  Dvalue = 6.473
  Group = -> [Ag_element002,Br_element005]
  conduct = 2
  density = 1
  expand = 3
  formula = G4_SILVER_BROMIDE
  name = G4_SILVER_BROMIDE
  specific = 4
FEATURE [App::DocumentObjectGroupPython] Ag_element003  label="Ag_element : 002"  # scripted group (container) (typed FeaturePython)
  n = 1
  ref = Ag_element
FEATURE [App::DocumentObjectGroupPython] Cl_element022  label="Cl_element : 011"  # scripted group (container) (typed FeaturePython)
  n = 1
  ref = Cl_element
FEATURE [App::DocumentObjectGroupPython] G4_SILVER_CHLORIDE  # scripted group (container) (typed FeaturePython)
  Dunit = g/cm3
  Dvalue = 5.56
  Group = -> [Ag_element003,Cl_element022]
  conduct = 2
  density = 1
  expand = 3
  formula = G4_SILVER_CHLORIDE
  name = G4_SILVER_CHLORIDE
  specific = 4
FEATURE [App::DocumentObjectGroupPython] Br_element006  label="Br_element : 0.423"  # scripted group (container) (typed FeaturePython)
  n = 0.422895
FEATURE [App::DocumentObjectGroupPython] Ag_element004  label="Ag_element : 0.574"  # scripted group (container) (typed FeaturePython)
  n = 0.573748
FEATURE [App::DocumentObjectGroupPython] I_element007  label="I_element : 0.649"  # scripted group (container) (typed FeaturePython)
  n = 0.003357
FEATURE [App::DocumentObjectGroupPython] G4_SILVER_HALIDES  # scripted group (container) (typed FeaturePython)
  Dunit = g/cm3
  Dvalue = 6.47
  Group = -> [Br_element006,Ag_element004,I_element007]
  conduct = 2
  density = 1
  expand = 3
  formula = G4_SILVER_HALIDES
  name = G4_SILVER_HALIDES
  specific = 4
FEATURE [App::DocumentObjectGroupPython] Ag_element005  label="Ag_element : 003"  # scripted group (container) (typed FeaturePython)
  n = 1
  ref = Ag_element
FEATURE [App::DocumentObjectGroupPython] I_element008  label="I_element : 004"  # scripted group (container) (typed FeaturePython)
  n = 1
  ref = I_element
FEATURE [App::DocumentObjectGroupPython] G4_SILVER_IODIDE  # scripted group (container) (typed FeaturePython)
  Dunit = g/cm3
  Dvalue = 6.01
  Group = -> [Ag_element005,I_element008]
  conduct = 2
  density = 1
  expand = 3
  formula = G4_SILVER_IODIDE
  name = G4_SILVER_IODIDE
  specific = 4
FEATURE [App::DocumentObjectGroupPython] H_element095  label="H_element : 0.100"  # scripted group (container) (typed FeaturePython)
  n = 0.1
FEATURE [App::DocumentObjectGroupPython] C_element103  label="C_element : 0.204"  # scripted group (container) (typed FeaturePython)
  n = 0.204
FEATURE [App::DocumentObjectGroupPython] N_element039  label="N_element : 0.759"  # scripted group (container) (typed FeaturePython)
  n = 0.042
FEATURE [App::DocumentObjectGroupPython] O_element088  label="O_element : 0.645"  # scripted group (container) (typed FeaturePython)
  n = 0.645
FEATURE [App::DocumentObjectGroupPython] Na_element013  label="Na_element : 0.100"  # scripted group (container) (typed FeaturePython)
  n = 0.002
FEATURE [App::DocumentObjectGroupPython] P_element009  label="P_element : 0.107"  # scripted group (container) (typed FeaturePython)
  n = 0.001
FEATURE [App::DocumentObjectGroupPython] S_element020  label="S_element : 0.021"  # scripted group (container) (typed FeaturePython)
  n = 0.002
FEATURE [App::DocumentObjectGroupPython] Cl_element023  label="Cl_element : 0.590"  # scripted group (container) (typed FeaturePython)
  n = 0.003
FEATURE [App::DocumentObjectGroupPython] K_element010  label="K_element : 0.001"  # scripted group (container) (typed FeaturePython)
  n = 0.001
FEATURE [App::DocumentObjectGroupPython] G4_SKIN_ICRP  # scripted group (container) (typed FeaturePython)
  Dunit = g/cm3
  Dvalue = 1.09
  Group = -> [H_element095,C_element103,N_element039,O_element088,Na_element013,P_element009,S_element020,Cl_element023,K_element010]
  conduct = 2
  density = 1
  expand = 3
  formula = G4_SKIN_ICRP
  name = G4_SKIN_ICRP
  specific = 4
FEATURE [App::DocumentObjectGroupPython] Na_element014  label="Na_element : 2"  # scripted group (container) (typed FeaturePython)
  n = 2
  ref = Na_element
FEATURE [App::DocumentObjectGroupPython] C_element104  label="C_element : 058"  # scripted group (container) (typed FeaturePython)
  n = 1
  ref = C_element
FEATURE [App::DocumentObjectGroupPython] O_element089  label="O_element : 049"  # scripted group (container) (typed FeaturePython)
  n = 3
  ref = O_element
FEATURE [App::DocumentObjectGroupPython] G4_SODIUM_CARBONATE  # scripted group (container) (typed FeaturePython)
  Dunit = g/cm3
  Dvalue = 2.532
  Group = -> [Na_element014,C_element104,O_element089]
  conduct = 2
  density = 1
  expand = 3
  formula = G4_SODIUM_CARBONATE
  name = G4_SODIUM_CARBONATE
  specific = 4
FEATURE [App::DocumentObjectGroupPython] Na_element015  label="Na_element : 1"  # scripted group (container) (typed FeaturePython)
  n = 1
  ref = Na_element
FEATURE [App::DocumentObjectGroupPython] I_element009  label="I_element : 005"  # scripted group (container) (typed FeaturePython)
  n = 1
  ref = I_element
FEATURE [App::DocumentObjectGroupPython] G4_SODIUM_IODIDE  # scripted group (container) (typed FeaturePython)
  Dunit = g/cm3
  Dvalue = 3.667
  Group = -> [Na_element015,I_element009]
  conduct = 2
  density = 1
  expand = 3
  formula = G4_SODIUM_IODIDE
  name = G4_SODIUM_IODIDE
  specific = 4
FEATURE [App::DocumentObjectGroupPython] Na_element016  label="Na_element : 003"  # scripted group (container) (typed FeaturePython)
  n = 2
  ref = Na_element
FEATURE [App::DocumentObjectGroupPython] O_element090  label="O_element : 050"  # scripted group (container) (typed FeaturePython)
  n = 1
  ref = O_element
FEATURE [App::DocumentObjectGroupPython] G4_SODIUM_MONOXIDE  # scripted group (container) (typed FeaturePython)
  Dunit = g/cm3
  Dvalue = 2.27
  Group = -> [Na_element016,O_element090]
  conduct = 2
  density = 1
  expand = 3
  formula = G4_SODIUM_MONOXIDE
  name = G4_SODIUM_MONOXIDE
  specific = 4
FEATURE [App::DocumentObjectGroupPython] Na_element017  label="Na_element : 004"  # scripted group (container) (typed FeaturePython)
  n = 1
  ref = Na_element
FEATURE [App::DocumentObjectGroupPython] N_element040  label="N_element : 018"  # scripted group (container) (typed FeaturePython)
  n = 1
  ref = N_element
FEATURE [App::DocumentObjectGroupPython] O_element091  label="O_element : 051"  # scripted group (container) (typed FeaturePython)
  n = 3
  ref = O_element
FEATURE [App::DocumentObjectGroupPython] G4_SODIUM_NITRATE  # scripted group (container) (typed FeaturePython)
  Dunit = g/cm3
  Dvalue = 2.261
  Group = -> [Na_element017,N_element040,O_element091]
  conduct = 2
  density = 1
  expand = 3
  formula = G4_SODIUM_NITRATE
  name = G4_SODIUM_NITRATE
  specific = 4
FEATURE [App::DocumentObjectGroupPython] C_element105  label="C_element : 059"  # scripted group (container) (typed FeaturePython)
  n = 14
  ref = C_element
FEATURE [App::DocumentObjectGroupPython] H_element096  label="H_element : 053"  # scripted group (container) (typed FeaturePython)
  n = 12
  ref = H_element
FEATURE [App::DocumentObjectGroupPython] G4_STILBENE  # scripted group (container) (typed FeaturePython)
  Dunit = g/cm3
  Dvalue = 0.9707
  Group = -> [C_element105,H_element096]
  conduct = 2
  density = 1
  expand = 3
  formula = G4_STILBENE
  name = G4_STILBENE
  specific = 4
FEATURE [App::DocumentObjectGroupPython] C_element106  label="C_element : 12"  # scripted group (container) (typed FeaturePython)
  n = 12
  ref = C_element
FEATURE [App::DocumentObjectGroupPython] H_element097  label="H_element : 22"  # scripted group (container) (typed FeaturePython)
  n = 22
  ref = H_element
FEATURE [App::DocumentObjectGroupPython] O_element092  label="O_element : 11"  # scripted group (container) (typed FeaturePython)
  n = 11
  ref = O_element
FEATURE [App::DocumentObjectGroupPython] G4_SUCROSE  # scripted group (container) (typed FeaturePython)
  Dunit = g/cm3
  Dvalue = 1.5805
  Group = -> [C_element106,H_element097,O_element092]
  conduct = 2
  density = 1
  expand = 3
  formula = G4_SUCROSE
  name = G4_SUCROSE
  specific = 4
FEATURE [App::DocumentObjectGroupPython] C_element107  label="C_element : 18"  # scripted group (container) (typed FeaturePython)
  n = 18
  ref = C_element
FEATURE [App::DocumentObjectGroupPython] H_element098  label="H_element : 054"  # scripted group (container) (typed FeaturePython)
  n = 14
  ref = H_element
FEATURE [App::DocumentObjectGroupPython] G4_TERPHENYL  # scripted group (container) (typed FeaturePython)
  Dunit = g/cm3
  Dvalue = 1.24
  Group = -> [C_element107,H_element098]
  conduct = 2
  density = 1
  expand = 3
  formula = G4_TERPHENYL
  name = G4_TERPHENYL
  specific = 4
FEATURE [App::DocumentObjectGroupPython] H_element099  label="H_element : 0.146"  # scripted group (container) (typed FeaturePython)
  n = 0.106
FEATURE [App::DocumentObjectGroupPython] C_element108  label="C_element : 0.883"  # scripted group (container) (typed FeaturePython)
  n = 0.099
FEATURE [App::DocumentObjectGroupPython] N_element041  label="N_element : 0.020"  # scripted group (container) (typed FeaturePython)
  n = 0.02
FEATURE [App::DocumentObjectGroupPython] O_element093  label="O_element : 0.766"  # scripted group (container) (typed FeaturePython)
  n = 0.766
FEATURE [App::DocumentObjectGroupPython] Na_element018  label="Na_element : 0.101"  # scripted group (container) (typed FeaturePython)
  n = 0.002
FEATURE [App::DocumentObjectGroupPython] P_element010  label="P_element : 0.108"  # scripted group (container) (typed FeaturePython)
  n = 0.001
FEATURE [App::DocumentObjectGroupPython] S_element021  label="S_element : 0.022"  # scripted group (container) (typed FeaturePython)
  n = 0.002
FEATURE [App::DocumentObjectGroupPython] Cl_element024  label="Cl_element : 0.002"  # scripted group (container) (typed FeaturePython)
  n = 0.002
FEATURE [App::DocumentObjectGroupPython] K_element011  label="K_element : 0.017"  # scripted group (container) (typed FeaturePython)
  n = 0.002
FEATURE [App::DocumentObjectGroupPython] G4_TESTIS_ICRP  # scripted group (container) (typed FeaturePython)
  Dunit = g/cm3
  Dvalue = 1.04
  Group = -> [H_element099,C_element108,N_element041,O_element093,Na_element018,P_element010,S_element021,Cl_element024,K_element011]
  conduct = 2
  density = 1
  expand = 3
  formula = G4_TESTIS_ICRP
  name = G4_TESTIS_ICRP
  specific = 4
FEATURE [App::DocumentObjectGroupPython] C_element109  label="C_element : 060"  # scripted group (container) (typed FeaturePython)
  n = 2
  ref = C_element
FEATURE [App::DocumentObjectGroupPython] Cl_element025  label="Cl_element : 012"  # scripted group (container) (typed FeaturePython)
  n = 4
  ref = Cl_element
FEATURE [App::DocumentObjectGroupPython] G4_TETRACHLOROETHYLENE  # scripted group (container) (typed FeaturePython)
  Dunit = g/cm3
  Dvalue = 1.625
  Group = -> [C_element109,Cl_element025]
  conduct = 2
  density = 1
  expand = 3
  formula = G4_TETRACHLOROETHYLENE
  name = G4_TETRACHLOROETHYLENE
  specific = 4
FEATURE [App::DocumentObjectGroupPython] Tl_element001  label="Tl_element : 1"  # scripted group (container) (typed FeaturePython)
  n = 1
  ref = Tl_element
FEATURE [App::DocumentObjectGroupPython] Cl_element026  label="Cl_element : 013"  # scripted group (container) (typed FeaturePython)
  n = 1
  ref = Cl_element
FEATURE [App::DocumentObjectGroupPython] G4_THALLIUM_CHLORIDE  # scripted group (container) (typed FeaturePython)
  Dunit = g/cm3
  Dvalue = 7.004
  Group = -> [Tl_element001,Cl_element026]
  conduct = 2
  density = 1
  expand = 3
  formula = G4_THALLIUM_CHLORIDE
  name = G4_THALLIUM_CHLORIDE
  specific = 4
FEATURE [App::DocumentObjectGroupPython] H_element100  label="H_element : 0.147"  # scripted group (container) (typed FeaturePython)
  n = 0.105
FEATURE [App::DocumentObjectGroupPython] C_element110  label="C_element : 0.256"  # scripted group (container) (typed FeaturePython)
  n = 0.256
FEATURE [App::DocumentObjectGroupPython] N_element042  label="N_element : 0.760"  # scripted group (container) (typed FeaturePython)
  n = 0.027
FEATURE [App::DocumentObjectGroupPython] O_element094  label="O_element : 0.602"  # scripted group (container) (typed FeaturePython)
  n = 0.602
FEATURE [App::DocumentObjectGroupPython] Na_element019  label="Na_element : 0.102"  # scripted group (container) (typed FeaturePython)
  n = 0.001
FEATURE [App::DocumentObjectGroupPython] P_element011  label="P_element : 0.109"  # scripted group (container) (typed FeaturePython)
  n = 0.002
FEATURE [App::DocumentObjectGroupPython] S_element022  label="S_element : 0.023"  # scripted group (container) (typed FeaturePython)
  n = 0.003
FEATURE [App::DocumentObjectGroupPython] Cl_element027  label="Cl_element : 0.591"  # scripted group (container) (typed FeaturePython)
  n = 0.002
FEATURE [App::DocumentObjectGroupPython] K_element012  label="K_element : 0.018"  # scripted group (container) (typed FeaturePython)
  n = 0.002
FEATURE [App::DocumentObjectGroupPython] G4_TISSUE_SOFT_ICRP  # scripted group (container) (typed FeaturePython)
  Dunit = g/cm3
  Dvalue = 1.03
  Group = -> [H_element100,C_element110,N_element042,O_element094,Na_element019,P_element011,S_element022,Cl_element027,K_element012]
  conduct = 2
  density = 1
  expand = 3
  formula = G4_TISSUE_SOFT_ICRP
  name = G4_TISSUE_SOFT_ICRP
  specific = 4
FEATURE [App::DocumentObjectGroupPython] H_element101  label="H_element : 0.148"  # scripted group (container) (typed FeaturePython)
  n = 0.101
FEATURE [App::DocumentObjectGroupPython] C_element111  label="C_element : 0.111"  # scripted group (container) (typed FeaturePython)
  n = 0.111
FEATURE [App::DocumentObjectGroupPython] N_element043  label="N_element : 0.026"  # scripted group (container) (typed FeaturePython)
  n = 0.026
FEATURE [App::DocumentObjectGroupPython] O_element095  label="O_element : 0.762"  # scripted group (container) (typed FeaturePython)
  n = 0.762
FEATURE [App::DocumentObjectGroupPython] G4_TISSUE_SOFT_ICRU_4  label="G4_TISSUE_SOFT_ICRU-4"  # scripted group (container) (typed FeaturePython)
  Dunit = g/cm3
  Dvalue = 1
  Group = -> [H_element101,C_element111,N_element043,O_element095]
  conduct = 2
  density = 1
  expand = 3
  formula = G4_TISSUE_SOFT_ICRU-4
  name = G4_TISSUE_SOFT_ICRU-4
  specific = 4
FEATURE [App::DocumentObjectGroupPython] H_element102  label="H_element : 0.149"  # scripted group (container) (typed FeaturePython)
  n = 0.101869
FEATURE [App::DocumentObjectGroupPython] C_element112  label="C_element : 0.456"  # scripted group (container) (typed FeaturePython)
  n = 0.456179
FEATURE [App::DocumentObjectGroupPython] N_element044  label="N_element : 0.761"  # scripted group (container) (typed FeaturePython)
  n = 0.035172
FEATURE [App::DocumentObjectGroupPython] O_element096  label="O_element : 0.407"  # scripted group (container) (typed FeaturePython)
  n = 0.40678
FEATURE [App::DocumentObjectGroupPython] G4_TISSUE_METHANE  label="G4_TISSUE-METHANE"  # scripted group (container) (typed FeaturePython)
  Dunit = g/cm3
  Dvalue = 0.00106409
  Group = -> [H_element102,C_element112,N_element044,O_element096]
  conduct = 2
  density = 1
  expand = 3
  formula = G4_TISSUE-METHANE
  name = G4_TISSUE-METHANE
  specific = 4
FEATURE [App::DocumentObjectGroupPython] H_element103  label="H_element : 0.103"  # scripted group (container) (typed FeaturePython)
  n = 0.102672
FEATURE [App::DocumentObjectGroupPython] C_element113  label="C_element : 0.569"  # scripted group (container) (typed FeaturePython)
  n = 0.56894
FEATURE [App::DocumentObjectGroupPython] N_element045  label="N_element : 0.762"  # scripted group (container) (typed FeaturePython)
  n = 0.035022
FEATURE [App::DocumentObjectGroupPython] O_element097  label="O_element : 0.293"  # scripted group (container) (typed FeaturePython)
  n = 0.293366
FEATURE [App::DocumentObjectGroupPython] G4_TISSUE_PROPANE  label="G4_TISSUE-PROPANE"  # scripted group (container) (typed FeaturePython)
  Dunit = g/cm3
  Dvalue = 0.00182628
  Group = -> [H_element103,C_element113,N_element045,O_element097]
  conduct = 2
  density = 1
  expand = 3
  formula = G4_TISSUE-PROPANE
  name = G4_TISSUE-PROPANE
  specific = 4
FEATURE [App::DocumentObjectGroupPython] Ti_element003  label="Ti_element : 1"  # scripted group (container) (typed FeaturePython)
  n = 1
  ref = Ti_element
FEATURE [App::DocumentObjectGroupPython] O_element098  label="O_element : 052"  # scripted group (container) (typed FeaturePython)
  n = 2
  ref = O_element
FEATURE [App::DocumentObjectGroupPython] G4_TITANIUM_DIOXIDE  # scripted group (container) (typed FeaturePython)
  Dunit = g/cm3
  Dvalue = 4.26
  Group = -> [Ti_element003,O_element098]
  conduct = 2
  density = 1
  expand = 3
  formula = G4_TITANIUM_DIOXIDE
  name = G4_TITANIUM_DIOXIDE
  specific = 4
FEATURE [App::DocumentObjectGroupPython] C_element114  label="C_element : 061"  # scripted group (container) (typed FeaturePython)
  n = 7
  ref = C_element
FEATURE [App::DocumentObjectGroupPython] H_element104  label="H_element : 055"  # scripted group (container) (typed FeaturePython)
  n = 8
  ref = H_element
FEATURE [App::DocumentObjectGroupPython] G4_TOLUENE  # scripted group (container) (typed FeaturePython)
  Dunit = g/cm3
  Dvalue = 0.8669
  Group = -> [C_element114,H_element104]
  conduct = 2
  density = 1
  expand = 3
  formula = G4_TOLUENE
  name = G4_TOLUENE
  specific = 4
FEATURE [App::DocumentObjectGroupPython] C_element115  label="C_element : 062"  # scripted group (container) (typed FeaturePython)
  n = 2
  ref = C_element
FEATURE [App::DocumentObjectGroupPython] H_element105  label="H_element : 056"  # scripted group (container) (typed FeaturePython)
  n = 1
  ref = H_element
FEATURE [App::DocumentObjectGroupPython] Cl_element028  label="Cl_element : 014"  # scripted group (container) (typed FeaturePython)
  n = 3
  ref = Cl_element
FEATURE [App::DocumentObjectGroupPython] G4_TRICHLOROETHYLENE  # scripted group (container) (typed FeaturePython)
  Dunit = g/cm3
  Dvalue = 1.46
  Group = -> [C_element115,H_element105,Cl_element028]
  conduct = 2
  density = 1
  expand = 3
  formula = G4_TRICHLOROETHYLENE
  name = G4_TRICHLOROETHYLENE
  specific = 4
FEATURE [App::DocumentObjectGroupPython] C_element116  label="C_element : 063"  # scripted group (container) (typed FeaturePython)
  n = 6
  ref = C_element
FEATURE [App::DocumentObjectGroupPython] H_element106  label="H_element : 15"  # scripted group (container) (typed FeaturePython)
  n = 15
  ref = H_element
FEATURE [App::DocumentObjectGroupPython] O_element099  label="O_element : 053"  # scripted group (container) (typed FeaturePython)
  n = 4
  ref = O_element
FEATURE [App::DocumentObjectGroupPython] P_element012  label="P_element : 1"  # scripted group (container) (typed FeaturePython)
  n = 1
  ref = P_element
FEATURE [App::DocumentObjectGroupPython] G4_TRIETHYL_PHOSPHATE  # scripted group (container) (typed FeaturePython)
  Dunit = g/cm3
  Dvalue = 1.07
  Group = -> [C_element116,H_element106,O_element099,P_element012]
  conduct = 2
  density = 1
  expand = 3
  formula = G4_TRIETHYL_PHOSPHATE
  name = G4_TRIETHYL_PHOSPHATE
  specific = 4
FEATURE [App::DocumentObjectGroupPython] W_element003  label="W_element : 003"  # scripted group (container) (typed FeaturePython)
  n = 1
  ref = W_element
FEATURE [App::DocumentObjectGroupPython] F_element017  label="F_element : 6"  # scripted group (container) (typed FeaturePython)
  n = 6
  ref = F_element
FEATURE [App::DocumentObjectGroupPython] G4_TUNGSTEN_HEXAFLUORIDE  # scripted group (container) (typed FeaturePython)
  Dunit = g/cm3
  Dvalue = 2.4
  Group = -> [W_element003,F_element017]
  conduct = 2
  density = 1
  expand = 3
  formula = G4_TUNGSTEN_HEXAFLUORIDE
  name = G4_TUNGSTEN_HEXAFLUORIDE
  specific = 4
FEATURE [App::DocumentObjectGroupPython] U_element001  label="U_element : 1"  # scripted group (container) (typed FeaturePython)
  n = 1
  ref = U_element
FEATURE [App::DocumentObjectGroupPython] C_element117  label="C_element : 064"  # scripted group (container) (typed FeaturePython)
  n = 2
  ref = C_element
FEATURE [App::DocumentObjectGroupPython] G4_URANIUM_DICARBIDE  # scripted group (container) (typed FeaturePython)
  Dunit = g/cm3
  Dvalue = 11.28
  Group = -> [U_element001,C_element117]
  conduct = 2
  density = 1
  expand = 3
  formula = G4_URANIUM_DICARBIDE
  name = G4_URANIUM_DICARBIDE
  specific = 4
FEATURE [App::DocumentObjectGroupPython] U_element002  label="U_element : 002"  # scripted group (container) (typed FeaturePython)
  n = 1
  ref = U_element
FEATURE [App::DocumentObjectGroupPython] C_element118  label="C_element : 065"  # scripted group (container) (typed FeaturePython)
  n = 1
  ref = C_element
FEATURE [App::DocumentObjectGroupPython] G4_URANIUM_MONOCARBIDE  # scripted group (container) (typed FeaturePython)
  Dunit = g/cm3
  Dvalue = 13.63
  Group = -> [U_element002,C_element118]
  conduct = 2
  density = 1
  expand = 3
  formula = G4_URANIUM_MONOCARBIDE
  name = G4_URANIUM_MONOCARBIDE
  specific = 4
FEATURE [App::DocumentObjectGroupPython] U_element003  label="U_element : 003"  # scripted group (container) (typed FeaturePython)
  n = 1
  ref = U_element
FEATURE [App::DocumentObjectGroupPython] O_element100  label="O_element : 054"  # scripted group (container) (typed FeaturePython)
  n = 2
  ref = O_element
FEATURE [App::DocumentObjectGroupPython] G4_URANIUM_OXIDE  # scripted group (container) (typed FeaturePython)
  Dunit = g/cm3
  Dvalue = 10.96
  Group = -> [U_element003,O_element100]
  conduct = 2
  density = 1
  expand = 3
  formula = G4_URANIUM_OXIDE
  name = G4_URANIUM_OXIDE
  specific = 4
FEATURE [App::DocumentObjectGroupPython] C_element119  label="C_element : 066"  # scripted group (container) (typed FeaturePython)
  n = 1
  ref = C_element
FEATURE [App::DocumentObjectGroupPython] H_element107  label="H_element : 057"  # scripted group (container) (typed FeaturePython)
  n = 4
  ref = H_element
FEATURE [App::DocumentObjectGroupPython] N_element046  label="N_element : 019"  # scripted group (container) (typed FeaturePython)
  n = 2
  ref = N_element
FEATURE [App::DocumentObjectGroupPython] O_element101  label="O_element : 055"  # scripted group (container) (typed FeaturePython)
  n = 1
  ref = O_element
FEATURE [App::DocumentObjectGroupPython] G4_UREA  # scripted group (container) (typed FeaturePython)
  Dunit = g/cm3
  Dvalue = 1.323
  Group = -> [C_element119,H_element107,N_element046,O_element101]
  conduct = 2
  density = 1
  expand = 3
  formula = G4_UREA
  name = G4_UREA
  specific = 4
FEATURE [App::DocumentObjectGroupPython] C_element120  label="C_element : 067"  # scripted group (container) (typed FeaturePython)
  n = 5
  ref = C_element
FEATURE [App::DocumentObjectGroupPython] H_element108  label="H_element : 058"  # scripted group (container) (typed FeaturePython)
  n = 11
  ref = H_element
FEATURE [App::DocumentObjectGroupPython] N_element047  label="N_element : 020"  # scripted group (container) (typed FeaturePython)
  n = 1
  ref = N_element
FEATURE [App::DocumentObjectGroupPython] O_element102  label="O_element : 056"  # scripted group (container) (typed FeaturePython)
  n = 2
  ref = O_element
FEATURE [App::DocumentObjectGroupPython] G4_VALINE  # scripted group (container) (typed FeaturePython)
  Dunit = g/cm3
  Dvalue = 1.23
  Group = -> [C_element120,H_element108,N_element047,O_element102]
  conduct = 2
  density = 1
  expand = 3
  formula = G4_VALINE
  name = G4_VALINE
  specific = 4
FEATURE [App::DocumentObjectGroupPython] H_element109  label="H_element : 0.009"  # scripted group (container) (typed FeaturePython)
  n = 0.009417
FEATURE [App::DocumentObjectGroupPython] C_element121  label="C_element : 0.281"  # scripted group (container) (typed FeaturePython)
  n = 0.280555
FEATURE [App::DocumentObjectGroupPython] F_element018  label="F_element : 0.710"  # scripted group (container) (typed FeaturePython)
  n = 0.710028
FEATURE [App::DocumentObjectGroupPython] G4_VITON  # scripted group (container) (typed FeaturePython)
  Dunit = g/cm3
  Dvalue = 1.8
  Group = -> [H_element109,C_element121,F_element018]
  conduct = 2
  density = 1
  expand = 3
  formula = G4_VITON
  name = G4_VITON
  specific = 4
FEATURE [App::DocumentObjectGroupPython] H_element110  label="H_element : 059"  # scripted group (container) (typed FeaturePython)
  n = 2
  ref = H_element
FEATURE [App::DocumentObjectGroupPython] O_element103  label="O_element : 057"  # scripted group (container) (typed FeaturePython)
  n = 1
  ref = O_element
FEATURE [App::DocumentObjectGroupPython] G4_WATER  # scripted group (container) (typed FeaturePython)
  Dunit = g/cm3
  Dvalue = 1
  Group = -> [H_element110,O_element103]
  conduct = 2
  density = 1
  expand = 3
  formula = G4_WATER
  name = G4_WATER
  specific = 4
FEATURE [App::DocumentObjectGroupPython] H_element111  label="H_element : 060"  # scripted group (container) (typed FeaturePython)
  n = 2
  ref = H_element
FEATURE [App::DocumentObjectGroupPython] O_element104  label="O_element : 058"  # scripted group (container) (typed FeaturePython)
  n = 1
  ref = O_element
FEATURE [App::DocumentObjectGroupPython] G4_WATER_VAPOR  # scripted group (container) (typed FeaturePython)
  Dunit = g/cm3
  Dvalue = 0.000756182
  Group = -> [H_element111,O_element104]
  conduct = 2
  density = 1
  expand = 3
  formula = G4_WATER_VAPOR
  name = G4_WATER_VAPOR
  specific = 4
FEATURE [App::DocumentObjectGroupPython] C_element122  label="C_element : 068"  # scripted group (container) (typed FeaturePython)
  n = 8
  ref = C_element
FEATURE [App::DocumentObjectGroupPython] H_element112  label="H_element : 061"  # scripted group (container) (typed FeaturePython)
  n = 10
  ref = H_element
FEATURE [App::DocumentObjectGroupPython] G4_XYLENE  # scripted group (container) (typed FeaturePython)
  Dunit = g/cm3
  Dvalue = 0.87
  Group = -> [C_element122,H_element112]
  conduct = 2
  density = 1
  expand = 3
  formula = G4_XYLENE
  name = G4_XYLENE
  specific = 4
FEATURE [App::DocumentObjectGroupPython] C_element123  label="C_element : 069"  # scripted group (container) (typed FeaturePython)
  n = 1
  ref = C_element
FEATURE [App::DocumentObjectGroupPython] G4_GRAPHITE  # scripted group (container) (typed FeaturePython)
  Dunit = g/cm3
  Dvalue = 2.21
  Group = -> [C_element123]
  conduct = 2
  density = 1
  expand = 3
  formula = G4_GRAPHITE
  name = G4_GRAPHITE
  specific = 4
FEATURE [App::DocumentObjectGroupPython] NIST  # scripted group (container) (typed FeaturePython)
  Group = -> [G4_A_150_TISSUE,G4_ACETONE,G4_ACETYLENE,G4_ADENINE,G4_ADIPOSE_TISSUE_ICRP,G4_AIR,G4_ALANINE,G4_ALUMINUM_OXIDE,G4_AMBER,G4_AMMONIA,G4_ANILINE,G4_ANTHRACENE,G4_B_100_BONE,G4_BAKELITE,G4_BARIUM_FLUORIDE,G4_BARIUM_SULFATE,G4_BENZENE,G4_BERYLLIUM_OXIDE,G4_BGO,G4_BLOOD_ICRP,G4_BONE_COMPACT_ICRU,G4_BONE_CORTICAL_ICRP,G4_BORON_CARBIDE,G4_BORON_OXIDE,G4_BRAIN_ICRP,G4_BUTANE,G4_N_BUTYL_ALCOHOL,G4_C_552,+152 more]
FEATURE [App::DocumentObjectGroupPython] H_element113  label="H_element : 062"  # scripted group (container) (typed FeaturePython)
  n = 1
  ref = H_element
FEATURE [App::DocumentObjectGroupPython] G4_H  # scripted group (container) (typed FeaturePython)
  Dunit = g/cm3
  Dvalue = 8.3748e-05
  Group = -> [H_element113]
  conduct = 2
  density = 1
  expand = 3
  formula = H
  name = G4_H
  specific = 4
FEATURE [App::DocumentObjectGroupPython] He_element001  label="He_element : 1"  # scripted group (container) (typed FeaturePython)
  n = 1
  ref = He_element
FEATURE [App::DocumentObjectGroupPython] G4_He  # scripted group (container) (typed FeaturePython)
  Dunit = g/cm3
  Dvalue = 0.000166322
  Group = -> [He_element001]
  conduct = 2
  density = 1
  expand = 3
  formula = He
  name = G4_He
  specific = 4
FEATURE [App::DocumentObjectGroupPython] Li_element008  label="Li_element : 008"  # scripted group (container) (typed FeaturePython)
  n = 1
  ref = Li_element
FEATURE [App::DocumentObjectGroupPython] G4_Li  # scripted group (container) (typed FeaturePython)
  Dunit = g/cm3
  Dvalue = 0.534
  Group = -> [Li_element008]
  conduct = 2
  density = 1
  expand = 3
  formula = Li
  name = G4_Li
  specific = 4
FEATURE [App::DocumentObjectGroupPython] Be_element002  label="Be_element : 002"  # scripted group (container) (typed FeaturePython)
  n = 1
  ref = Be_element
FEATURE [App::DocumentObjectGroupPython] G4_Be  # scripted group (container) (typed FeaturePython)
  Dunit = g/cm3
  Dvalue = 1.848
  Group = -> [Be_element002]
  conduct = 2
  density = 1
  expand = 3
  formula = Be
  name = G4_Be
  specific = 4
FEATURE [App::DocumentObjectGroupPython] B_element007  label="B_element : 007"  # scripted group (container) (typed FeaturePython)
  n = 1
  ref = B_element
FEATURE [App::DocumentObjectGroupPython] G4_B  # scripted group (container) (typed FeaturePython)
  Dunit = g/cm3
  Dvalue = 2.37
  Group = -> [B_element007]
  conduct = 2
  density = 1
  expand = 3
  formula = B
  name = G4_B
  specific = 4
FEATURE [App::DocumentObjectGroupPython] C_element124  label="C_element : 070"  # scripted group (container) (typed FeaturePython)
  n = 1
  ref = C_element
FEATURE [App::DocumentObjectGroupPython] G4_C  # scripted group (container) (typed FeaturePython)
  Dunit = g/cm3
  Dvalue = 2
  Group = -> [C_element124]
  conduct = 2
  density = 1
  expand = 3
  formula = C
  name = G4_C
  specific = 4
FEATURE [App::DocumentObjectGroupPython] N_element048  label="N_element : 021"  # scripted group (container) (typed FeaturePython)
  n = 1
  ref = N_element
FEATURE [App::DocumentObjectGroupPython] G4_N  # scripted group (container) (typed FeaturePython)
  Dunit = g/cm3
  Dvalue = 0.0011652
  Group = -> [N_element048]
  conduct = 2
  density = 1
  expand = 3
  formula = N
  name = G4_N
  specific = 4
FEATURE [App::DocumentObjectGroupPython] O_element105  label="O_element : 059"  # scripted group (container) (typed FeaturePython)
  n = 1
  ref = O_element
FEATURE [App::DocumentObjectGroupPython] G4_O  # scripted group (container) (typed FeaturePython)
  Dunit = g/cm3
  Dvalue = 0.00133151
  Group = -> [O_element105]
  conduct = 2
  density = 1
  expand = 3
  formula = O
  name = G4_O
  specific = 4
FEATURE [App::DocumentObjectGroupPython] F_element019  label="F_element : 008"  # scripted group (container) (typed FeaturePython)
  n = 1
  ref = F_element
FEATURE [App::DocumentObjectGroupPython] G4_F  # scripted group (container) (typed FeaturePython)
  Dunit = g/cm3
  Dvalue = 0.00158029
  Group = -> [F_element019]
  conduct = 2
  density = 1
  expand = 3
  formula = F
  name = G4_F
  specific = 4
FEATURE [App::DocumentObjectGroupPython] Ne_element001  label="Ne_element : 1"  # scripted group (container) (typed FeaturePython)
  n = 1
  ref = Ne_element
FEATURE [App::DocumentObjectGroupPython] G4_Ne  # scripted group (container) (typed FeaturePython)
  Dunit = g/cm3
  Dvalue = 0.000838505
  Group = -> [Ne_element001]
  conduct = 2
  density = 1
  expand = 3
  formula = Ne
  name = G4_Ne
  specific = 4
FEATURE [App::DocumentObjectGroupPython] Na_element020  label="Na_element : 005"  # scripted group (container) (typed FeaturePython)
  n = 1
  ref = Na_element
FEATURE [App::DocumentObjectGroupPython] G4_Na  # scripted group (container) (typed FeaturePython)
  Dunit = g/cm3
  Dvalue = 0.971
  Group = -> [Na_element020]
  conduct = 2
  density = 1
  expand = 3
  formula = Na
  name = G4_Na
  specific = 4
FEATURE [App::DocumentObjectGroupPython] Mg_element011  label="Mg_element : 005"  # scripted group (container) (typed FeaturePython)
  n = 1
  ref = Mg_element
FEATURE [App::DocumentObjectGroupPython] G4_Mg  # scripted group (container) (typed FeaturePython)
  Dunit = g/cm3
  Dvalue = 1.74
  Group = -> [Mg_element011]
  conduct = 2
  density = 1
  expand = 3
  formula = Mg
  name = G4_Mg
  specific = 4
FEATURE [App::DocumentObjectGroupPython] Al_element004  label="Al_element : 1"  # scripted group (container) (typed FeaturePython)
  n = 1
  ref = Al_element
FEATURE [App::DocumentObjectGroupPython] G4_Al  # scripted group (container) (typed FeaturePython)
  Dunit = g/cm3
  Dvalue = 2.699
  Group = -> [Al_element004]
  conduct = 2
  density = 1
  expand = 3
  formula = Al
  name = G4_Al
  specific = 4
FEATURE [App::DocumentObjectGroupPython] Si_element007  label="Si_element : 002"  # scripted group (container) (typed FeaturePython)
  n = 1
  ref = Si_element
FEATURE [App::DocumentObjectGroupPython] G4_Si  # scripted group (container) (typed FeaturePython)
  Dunit = g/cm3
  Dvalue = 2.33
  Group = -> [Si_element007]
  conduct = 2
  density = 1
  expand = 3
  formula = Si
  name = G4_Si
  specific = 4
FEATURE [App::DocumentObjectGroupPython] P_element013  label="P_element : 002"  # scripted group (container) (typed FeaturePython)
  n = 1
  ref = P_element
FEATURE [App::DocumentObjectGroupPython] G4_P  # scripted group (container) (typed FeaturePython)
  Dunit = g/cm3
  Dvalue = 2.2
  Group = -> [P_element013]
  conduct = 2
  density = 1
  expand = 3
  formula = P
  name = G4_P
  specific = 4
FEATURE [App::DocumentObjectGroupPython] S_element023  label="S_element : 007"  # scripted group (container) (typed FeaturePython)
  n = 1
  ref = S_element
FEATURE [App::DocumentObjectGroupPython] G4_S  # scripted group (container) (typed FeaturePython)
  Dunit = g/cm3
  Dvalue = 2
  Group = -> [S_element023]
  conduct = 2
  density = 1
  expand = 3
  formula = S
  name = G4_S
  specific = 4
FEATURE [App::DocumentObjectGroupPython] Cl_element029  label="Cl_element : 015"  # scripted group (container) (typed FeaturePython)
  n = 1
  ref = Cl_element
FEATURE [App::DocumentObjectGroupPython] G4_Cl  # scripted group (container) (typed FeaturePython)
  Dunit = g/cm3
  Dvalue = 0.00299473
  Group = -> [Cl_element029]
  conduct = 2
  density = 1
  expand = 3
  formula = Cl
  name = G4_Cl
  specific = 4
FEATURE [App::DocumentObjectGroupPython] Ar_element002  label="Ar_element : 1"  # scripted group (container) (typed FeaturePython)
  n = 1
  ref = Ar_element
FEATURE [App::DocumentObjectGroupPython] G4_Ar  # scripted group (container) (typed FeaturePython)
  Dunit = g/cm3
  Dvalue = 0.00166201
  Group = -> [Ar_element002]
  conduct = 2
  density = 1
  expand = 3
  formula = Ar
  name = G4_Ar
  specific = 4
FEATURE [App::DocumentObjectGroupPython] K_element013  label="K_element : 003"  # scripted group (container) (typed FeaturePython)
  n = 1
  ref = K_element
FEATURE [App::DocumentObjectGroupPython] G4_K  # scripted group (container) (typed FeaturePython)
  Dunit = g/cm3
  Dvalue = 0.862
  Group = -> [K_element013]
  conduct = 2
  density = 1
  expand = 3
  formula = K
  name = G4_K
  specific = 4
FEATURE [App::DocumentObjectGroupPython] Ca_element014  label="Ca_element : 007"  # scripted group (container) (typed FeaturePython)
  n = 1
  ref = Ca_element
FEATURE [App::DocumentObjectGroupPython] G4_Ca  # scripted group (container) (typed FeaturePython)
  Dunit = g/cm3
  Dvalue = 1.55
  Group = -> [Ca_element014]
  conduct = 2
  density = 1
  expand = 3
  formula = Ca
  name = G4_Ca
  specific = 4
FEATURE [App::DocumentObjectGroupPython] Sc_element001  label="Sc_element : 1"  # scripted group (container) (typed FeaturePython)
  n = 1
  ref = Sc_element
FEATURE [App::DocumentObjectGroupPython] G4_Sc  # scripted group (container) (typed FeaturePython)
  Dunit = g/cm3
  Dvalue = 2.989
  Group = -> [Sc_element001]
  conduct = 2
  density = 1
  expand = 3
  formula = Sc
  name = G4_Sc
  specific = 4
FEATURE [App::DocumentObjectGroupPython] Ti_element004  label="Ti_element : 002"  # scripted group (container) (typed FeaturePython)
  n = 1
  ref = Ti_element
FEATURE [App::DocumentObjectGroupPython] G4_Ti  # scripted group (container) (typed FeaturePython)
  Dunit = g/cm3
  Dvalue = 4.54
  Group = -> [Ti_element004]
  conduct = 2
  density = 1
  expand = 3
  formula = Ti
  name = G4_Ti
  specific = 4
FEATURE [App::DocumentObjectGroupPython] V_element001  label="V_element : 1"  # scripted group (container) (typed FeaturePython)
  n = 1
  ref = V_element
FEATURE [App::DocumentObjectGroupPython] G4_V  # scripted group (container) (typed FeaturePython)
  Dunit = g/cm3
  Dvalue = 6.11
  Group = -> [V_element001]
  conduct = 2
  density = 1
  expand = 3
  formula = V
  name = G4_V
  specific = 4
FEATURE [App::DocumentObjectGroupPython] Cr_element001  label="Cr_element : 1"  # scripted group (container) (typed FeaturePython)
  n = 1
  ref = Cr_element
FEATURE [App::DocumentObjectGroupPython] G4_Cr  # scripted group (container) (typed FeaturePython)
  Dunit = g/cm3
  Dvalue = 7.18
  Group = -> [Cr_element001]
  conduct = 2
  density = 1
  expand = 3
  formula = Cr
  name = G4_Cr
  specific = 4
FEATURE [App::DocumentObjectGroupPython] Mn_element001  label="Mn_element : 1"  # scripted group (container) (typed FeaturePython)
  n = 1
  ref = Mn_element
FEATURE [App::DocumentObjectGroupPython] G4_Mn  # scripted group (container) (typed FeaturePython)
  Dunit = g/cm3
  Dvalue = 7.44
  Group = -> [Mn_element001]
  conduct = 2
  density = 1
  expand = 3
  formula = Mn
  name = G4_Mn
  specific = 4
FEATURE [App::DocumentObjectGroupPython] Fe_element007  label="Fe_element : 004"  # scripted group (container) (typed FeaturePython)
  n = 1
  ref = Fe_element
FEATURE [App::DocumentObjectGroupPython] G4_Fe  # scripted group (container) (typed FeaturePython)
  Dunit = g/cm3
  Dvalue = 7.874
  Group = -> [Fe_element007]
  conduct = 2
  density = 1
  expand = 3
  formula = Fe
  name = G4_Fe
  specific = 4
FEATURE [App::DocumentObjectGroupPython] Co_element001  label="Co_element : 1"  # scripted group (container) (typed FeaturePython)
  n = 1
  ref = Co_element
FEATURE [App::DocumentObjectGroupPython] G4_Co  # scripted group (container) (typed FeaturePython)
  Dunit = g/cm3
  Dvalue = 8.9
  Group = -> [Co_element001]
  conduct = 2
  density = 1
  expand = 3
  formula = Co
  name = G4_Co
  specific = 4
FEATURE [App::DocumentObjectGroupPython] Ni_element001  label="Ni_element : 1"  # scripted group (container) (typed FeaturePython)
  n = 1
  ref = Ni_element
FEATURE [App::DocumentObjectGroupPython] G4_Ni  # scripted group (container) (typed FeaturePython)
  Dunit = g/cm3
  Dvalue = 8.902
  Group = -> [Ni_element001]
  conduct = 2
  density = 1
  expand = 3
  formula = Ni
  name = G4_Ni
  specific = 4
FEATURE [App::DocumentObjectGroupPython] Cu_element001  label="Cu_element : 1"  # scripted group (container) (typed FeaturePython)
  n = 1
  ref = Cu_element
FEATURE [App::DocumentObjectGroupPython] G4_Cu  # scripted group (container) (typed FeaturePython)
  Dunit = g/cm3
  Dvalue = 8.96
  Group = -> [Cu_element001]
  conduct = 2
  density = 1
  expand = 3
  formula = Cu
  name = G4_Cu
  specific = 4
FEATURE [App::DocumentObjectGroupPython] Zn_element001  label="Zn_element : 1"  # scripted group (container) (typed FeaturePython)
  n = 1
  ref = Zn_element
FEATURE [App::DocumentObjectGroupPython] G4_Zn  # scripted group (container) (typed FeaturePython)
  Dunit = g/cm3
  Dvalue = 7.133
  Group = -> [Zn_element001]
  conduct = 2
  density = 1
  expand = 3
  formula = Zn
  name = G4_Zn
  specific = 4
FEATURE [App::DocumentObjectGroupPython] Ga_element002  label="Ga_element : 002"  # scripted group (container) (typed FeaturePython)
  n = 1
  ref = Ga_element
FEATURE [App::DocumentObjectGroupPython] G4_Ga  # scripted group (container) (typed FeaturePython)
  Dunit = g/cm3
  Dvalue = 5.904
  Group = -> [Ga_element002]
  conduct = 2
  density = 1
  expand = 3
  formula = Ga
  name = G4_Ga
  specific = 4
FEATURE [App::DocumentObjectGroupPython] Ge_element002  label="Ge_element : 1"  # scripted group (container) (typed FeaturePython)
  n = 1
  ref = Ge_element
FEATURE [App::DocumentObjectGroupPython] G4_Ge  # scripted group (container) (typed FeaturePython)
  Dunit = g/cm3
  Dvalue = 5.323
  Group = -> [Ge_element002]
  conduct = 2
  density = 1
  expand = 3
  formula = Ge
  name = G4_Ge
  specific = 4
FEATURE [App::DocumentObjectGroupPython] As_element003  label="As_element : 002"  # scripted group (container) (typed FeaturePython)
  n = 1
  ref = As_element
FEATURE [App::DocumentObjectGroupPython] G4_As  # scripted group (container) (typed FeaturePython)
  Dunit = g/cm3
  Dvalue = 5.73
  Group = -> [As_element003]
  conduct = 2
  density = 1
  expand = 3
  formula = As
  name = G4_As
  specific = 4
FEATURE [App::DocumentObjectGroupPython] Se_element001  label="Se_element : 1"  # scripted group (container) (typed FeaturePython)
  n = 1
  ref = Se_element
FEATURE [App::DocumentObjectGroupPython] G4_Se  # scripted group (container) (typed FeaturePython)
  Dunit = g/cm3
  Dvalue = 4.5
  Group = -> [Se_element001]
  conduct = 2
  density = 1
  expand = 3
  formula = Se
  name = G4_Se
  specific = 4
FEATURE [App::DocumentObjectGroupPython] Br_element007  label="Br_element : 004"  # scripted group (container) (typed FeaturePython)
  n = 1
  ref = Br_element
FEATURE [App::DocumentObjectGroupPython] G4_Br  # scripted group (container) (typed FeaturePython)
  Dunit = g/cm3
  Dvalue = 0.0070721
  Group = -> [Br_element007]
  conduct = 2
  density = 1
  expand = 3
  formula = Br
  name = G4_Br
  specific = 4
FEATURE [App::DocumentObjectGroupPython] Kr_element001  label="Kr_element : 1"  # scripted group (container) (typed FeaturePython)
  n = 1
  ref = Kr_element
FEATURE [App::DocumentObjectGroupPython] G4_Kr  # scripted group (container) (typed FeaturePython)
  Dunit = g/cm3
  Dvalue = 0.00347832
  Group = -> [Kr_element001]
  conduct = 2
  density = 1
  expand = 3
  formula = Kr
  name = G4_Kr
  specific = 4
FEATURE [App::DocumentObjectGroupPython] Rb_element001  label="Rb_element : 1"  # scripted group (container) (typed FeaturePython)
  n = 1
  ref = Rb_element
FEATURE [App::DocumentObjectGroupPython] G4_Rb  # scripted group (container) (typed FeaturePython)
  Dunit = g/cm3
  Dvalue = 1.532
  Group = -> [Rb_element001]
  conduct = 2
  density = 1
  expand = 3
  formula = Rb
  name = G4_Rb
  specific = 4
FEATURE [App::DocumentObjectGroupPython] Sr_element001  label="Sr_element : 1"  # scripted group (container) (typed FeaturePython)
  n = 1
  ref = Sr_element
FEATURE [App::DocumentObjectGroupPython] G4_Sr  # scripted group (container) (typed FeaturePython)
  Dunit = g/cm3
  Dvalue = 2.54
  Group = -> [Sr_element001]
  conduct = 2
  density = 1
  expand = 3
  formula = Sr
  name = G4_Sr
  specific = 4
FEATURE [App::DocumentObjectGroupPython] Y_element001  label="Y_element : 1"  # scripted group (container) (typed FeaturePython)
  n = 1
  ref = Y_element
FEATURE [App::DocumentObjectGroupPython] G4_Y  # scripted group (container) (typed FeaturePython)
  Dunit = g/cm3
  Dvalue = 4.469
  Group = -> [Y_element001]
  conduct = 2
  density = 1
  expand = 3
  formula = Y
  name = G4_Y
  specific = 4
FEATURE [App::DocumentObjectGroupPython] Zr_element001  label="Zr_element : 1"  # scripted group (container) (typed FeaturePython)
  n = 1
  ref = Zr_element
FEATURE [App::DocumentObjectGroupPython] G4_Zr  # scripted group (container) (typed FeaturePython)
  Dunit = g/cm3
  Dvalue = 6.506
  Group = -> [Zr_element001]
  conduct = 2
  density = 1
  expand = 3
  formula = Zr
  name = G4_Zr
  specific = 4
FEATURE [App::DocumentObjectGroupPython] Nb_element001  label="Nb_element : 1"  # scripted group (container) (typed FeaturePython)
  n = 1
  ref = Nb_element
FEATURE [App::DocumentObjectGroupPython] G4_Nb  # scripted group (container) (typed FeaturePython)
  Dunit = g/cm3
  Dvalue = 8.57
  Group = -> [Nb_element001]
  conduct = 2
  density = 1
  expand = 3
  formula = Nb
  name = G4_Nb
  specific = 4
FEATURE [App::DocumentObjectGroupPython] Mo_element001  label="Mo_element : 1"  # scripted group (container) (typed FeaturePython)
  n = 1
  ref = Mo_element
FEATURE [App::DocumentObjectGroupPython] G4_Mo  # scripted group (container) (typed FeaturePython)
  Dunit = g/cm3
  Dvalue = 10.22
  Group = -> [Mo_element001]
  conduct = 2
  density = 1
  expand = 3
  formula = Mo
  name = G4_Mo
  specific = 4
FEATURE [App::DocumentObjectGroupPython] Tc_element001  label="Tc_element : 1"  # scripted group (container) (typed FeaturePython)
  n = 1
  ref = Tc_element
FEATURE [App::DocumentObjectGroupPython] G4_Tc  # scripted group (container) (typed FeaturePython)
  Dunit = g/cm3
  Dvalue = 11.5
  Group = -> [Tc_element001]
  conduct = 2
  density = 1
  expand = 3
  formula = Tc
  name = G4_Tc
  specific = 4
FEATURE [App::DocumentObjectGroupPython] Ru_element001  label="Ru_element : 1"  # scripted group (container) (typed FeaturePython)
  n = 1
  ref = Ru_element
FEATURE [App::DocumentObjectGroupPython] G4_Ru  # scripted group (container) (typed FeaturePython)
  Dunit = g/cm3
  Dvalue = 12.41
  Group = -> [Ru_element001]
  conduct = 2
  density = 1
  expand = 3
  formula = Ru
  name = G4_Ru
  specific = 4
FEATURE [App::DocumentObjectGroupPython] Rh_element001  label="Rh_element : 1"  # scripted group (container) (typed FeaturePython)
  n = 1
  ref = Rh_element
FEATURE [App::DocumentObjectGroupPython] G4_Rh  # scripted group (container) (typed FeaturePython)
  Dunit = g/cm3
  Dvalue = 12.41
  Group = -> [Rh_element001]
  conduct = 2
  density = 1
  expand = 3
  formula = Rh
  name = G4_Rh
  specific = 4
FEATURE [App::DocumentObjectGroupPython] Pd_element001  label="Pd_element : 1"  # scripted group (container) (typed FeaturePython)
  n = 1
  ref = Pd_element
FEATURE [App::DocumentObjectGroupPython] G4_Pd  # scripted group (container) (typed FeaturePython)
  Dunit = g/cm3
  Dvalue = 12.02
  Group = -> [Pd_element001]
  conduct = 2
  density = 1
  expand = 3
  formula = Pd
  name = G4_Pd
  specific = 4
FEATURE [App::DocumentObjectGroupPython] Ag_element006  label="Ag_element : 004"  # scripted group (container) (typed FeaturePython)
  n = 1
  ref = Ag_element
FEATURE [App::DocumentObjectGroupPython] G4_Ag  # scripted group (container) (typed FeaturePython)
  Dunit = g/cm3
  Dvalue = 10.5
  Group = -> [Ag_element006]
  conduct = 2
  density = 1
  expand = 3
  formula = Ag
  name = G4_Ag
  specific = 4
FEATURE [App::DocumentObjectGroupPython] Cd_element003  label="Cd_element : 003"  # scripted group (container) (typed FeaturePython)
  n = 1
  ref = Cd_element
FEATURE [App::DocumentObjectGroupPython] G4_Cd  # scripted group (container) (typed FeaturePython)
  Dunit = g/cm3
  Dvalue = 8.65
  Group = -> [Cd_element003]
  conduct = 2
  density = 1
  expand = 3
  formula = Cd
  name = G4_Cd
  specific = 4
FEATURE [App::DocumentObjectGroupPython] In_element001  label="In_element : 1"  # scripted group (container) (typed FeaturePython)
  n = 1
  ref = In_element
FEATURE [App::DocumentObjectGroupPython] G4_In  # scripted group (container) (typed FeaturePython)
  Dunit = g/cm3
  Dvalue = 7.31
  Group = -> [In_element001]
  conduct = 2
  density = 1
  expand = 3
  formula = In
  name = G4_In
  specific = 4
FEATURE [App::DocumentObjectGroupPython] Sn_element001  label="Sn_element : 1"  # scripted group (container) (typed FeaturePython)
  n = 1
  ref = Sn_element
FEATURE [App::DocumentObjectGroupPython] G4_Sn  # scripted group (container) (typed FeaturePython)
  Dunit = g/cm3
  Dvalue = 7.31
  Group = -> [Sn_element001]
  conduct = 2
  density = 1
  expand = 3
  formula = Sn
  name = G4_Sn
  specific = 4
FEATURE [App::DocumentObjectGroupPython] Sb_element001  label="Sb_element : 1"  # scripted group (container) (typed FeaturePython)
  n = 1
  ref = Sb_element
FEATURE [App::DocumentObjectGroupPython] G4_Sb  # scripted group (container) (typed FeaturePython)
  Dunit = g/cm3
  Dvalue = 6.691
  Group = -> [Sb_element001]
  conduct = 2
  density = 1
  expand = 3
  formula = Sb
  name = G4_Sb
  specific = 4
FEATURE [App::DocumentObjectGroupPython] Te_element002  label="Te_element : 002"  # scripted group (container) (typed FeaturePython)
  n = 1
  ref = Te_element
FEATURE [App::DocumentObjectGroupPython] G4_Te  # scripted group (container) (typed FeaturePython)
  Dunit = g/cm3
  Dvalue = 6.24
  Group = -> [Te_element002]
  conduct = 2
  density = 1
  expand = 3
  formula = Te
  name = G4_Te
  specific = 4
FEATURE [App::DocumentObjectGroupPython] I_element010  label="I_element : 006"  # scripted group (container) (typed FeaturePython)
  n = 1
  ref = I_element
FEATURE [App::DocumentObjectGroupPython] G4_I  # scripted group (container) (typed FeaturePython)
  Dunit = g/cm3
  Dvalue = 4.93
  Group = -> [I_element010]
  conduct = 2
  density = 1
  expand = 3
  formula = I
  name = G4_I
  specific = 4
FEATURE [App::DocumentObjectGroupPython] Xe_element001  label="Xe_element : 1"  # scripted group (container) (typed FeaturePython)
  n = 1
  ref = Xe_element
FEATURE [App::DocumentObjectGroupPython] G4_Xe  # scripted group (container) (typed FeaturePython)
  Dunit = g/cm3
  Dvalue = 0.00548536
  Group = -> [Xe_element001]
  conduct = 2
  density = 1
  expand = 3
  formula = Xe
  name = G4_Xe
  specific = 4
FEATURE [App::DocumentObjectGroupPython] Cs_element003  label="Cs_element : 003"  # scripted group (container) (typed FeaturePython)
  n = 1
  ref = Cs_element
FEATURE [App::DocumentObjectGroupPython] G4_Cs  # scripted group (container) (typed FeaturePython)
  Dunit = g/cm3
  Dvalue = 1.873
  Group = -> [Cs_element003]
  conduct = 2
  density = 1
  expand = 3
  formula = Cs
  name = G4_Cs
  specific = 4
FEATURE [App::DocumentObjectGroupPython] Ba_element003  label="Ba_element : 003"  # scripted group (container) (typed FeaturePython)
  n = 1
  ref = Ba_element
FEATURE [App::DocumentObjectGroupPython] G4_Ba  # scripted group (container) (typed FeaturePython)
  Dunit = g/cm3
  Dvalue = 3.5
  Group = -> [Ba_element003]
  conduct = 2
  density = 1
  expand = 3
  formula = Ba
  name = G4_Ba
  specific = 4
FEATURE [App::DocumentObjectGroupPython] La_element003  label="La_element : 003"  # scripted group (container) (typed FeaturePython)
  n = 1
  ref = La_element
FEATURE [App::DocumentObjectGroupPython] G4_La  # scripted group (container) (typed FeaturePython)
  Dunit = g/cm3
  Dvalue = 6.154
  Group = -> [La_element003]
  conduct = 2
  density = 1
  expand = 3
  formula = La
  name = G4_La
  specific = 4
FEATURE [App::DocumentObjectGroupPython] Ce_element002  label="Ce_element : 1"  # scripted group (container) (typed FeaturePython)
  n = 1
  ref = Ce_element
FEATURE [App::DocumentObjectGroupPython] G4_Ce  # scripted group (container) (typed FeaturePython)
  Dunit = g/cm3
  Dvalue = 6.657
  Group = -> [Ce_element002]
  conduct = 2
  density = 1
  expand = 3
  formula = Ce
  name = G4_Ce
  specific = 4
FEATURE [App::DocumentObjectGroupPython] Pr_element001  label="Pr_element : 1"  # scripted group (container) (typed FeaturePython)
  n = 1
  ref = Pr_element
FEATURE [App::DocumentObjectGroupPython] G4_Pr  # scripted group (container) (typed FeaturePython)
  Dunit = g/cm3
  Dvalue = 6.71
  Group = -> [Pr_element001]
  conduct = 2
  density = 1
  expand = 3
  formula = Pr
  name = G4_Pr
  specific = 4
FEATURE [App::DocumentObjectGroupPython] Nd_element001  label="Nd_element : 1"  # scripted group (container) (typed FeaturePython)
  n = 1
  ref = Nd_element
FEATURE [App::DocumentObjectGroupPython] G4_Nd  # scripted group (container) (typed FeaturePython)
  Dunit = g/cm3
  Dvalue = 6.9
  Group = -> [Nd_element001]
  conduct = 2
  density = 1
  expand = 3
  formula = Nd
  name = G4_Nd
  specific = 4
FEATURE [App::DocumentObjectGroupPython] Pm_element001  label="Pm_element : 1"  # scripted group (container) (typed FeaturePython)
  n = 1
  ref = Pm_element
FEATURE [App::DocumentObjectGroupPython] G4_Pm  # scripted group (container) (typed FeaturePython)
  Dunit = g/cm3
  Dvalue = 7.22
  Group = -> [Pm_element001]
  conduct = 2
  density = 1
  expand = 3
  formula = Pm
  name = G4_Pm
  specific = 4
FEATURE [App::DocumentObjectGroupPython] Sm_element001  label="Sm_element : 1"  # scripted group (container) (typed FeaturePython)
  n = 1
  ref = Sm_element
FEATURE [App::DocumentObjectGroupPython] G4_Sm  # scripted group (container) (typed FeaturePython)
  Dunit = g/cm3
  Dvalue = 7.46
  Group = -> [Sm_element001]
  conduct = 2
  density = 1
  expand = 3
  formula = Sm
  name = G4_Sm
  specific = 4
FEATURE [App::DocumentObjectGroupPython] Eu_element001  label="Eu_element : 1"  # scripted group (container) (typed FeaturePython)
  n = 1
  ref = Eu_element
FEATURE [App::DocumentObjectGroupPython] G4_Eu  # scripted group (container) (typed FeaturePython)
  Dunit = g/cm3
  Dvalue = 5.243
  Group = -> [Eu_element001]
  conduct = 2
  density = 1
  expand = 3
  formula = Eu
  name = G4_Eu
  specific = 4
FEATURE [App::DocumentObjectGroupPython] Gd_element002  label="Gd_element : 1"  # scripted group (container) (typed FeaturePython)
  n = 1
  ref = Gd_element
FEATURE [App::DocumentObjectGroupPython] G4_Gd  # scripted group (container) (typed FeaturePython)
  Dunit = g/cm3
  Dvalue = 7.9004
  Group = -> [Gd_element002]
  conduct = 2
  density = 1
  expand = 3
  formula = Gd
  name = G4_Gd
  specific = 4
FEATURE [App::DocumentObjectGroupPython] Tb_element001  label="Tb_element : 1"  # scripted group (container) (typed FeaturePython)
  n = 1
  ref = Tb_element
FEATURE [App::DocumentObjectGroupPython] G4_Tb  # scripted group (container) (typed FeaturePython)
  Dunit = g/cm3
  Dvalue = 8.229
  Group = -> [Tb_element001]
  conduct = 2
  density = 1
  expand = 3
  formula = Tb
  name = G4_Tb
  specific = 4
FEATURE [App::DocumentObjectGroupPython] Dy_element001  label="Dy_element : 1"  # scripted group (container) (typed FeaturePython)
  n = 1
  ref = Dy_element
FEATURE [App::DocumentObjectGroupPython] G4_Dy  # scripted group (container) (typed FeaturePython)
  Dunit = g/cm3
  Dvalue = 8.55
  Group = -> [Dy_element001]
  conduct = 2
  density = 1
  expand = 3
  formula = Dy
  name = G4_Dy
  specific = 4
FEATURE [App::DocumentObjectGroupPython] Ho_element001  label="Ho_element : 1"  # scripted group (container) (typed FeaturePython)
  n = 1
  ref = Ho_element
FEATURE [App::DocumentObjectGroupPython] G4_Ho  # scripted group (container) (typed FeaturePython)
  Dunit = g/cm3
  Dvalue = 8.795
  Group = -> [Ho_element001]
  conduct = 2
  density = 1
  expand = 3
  formula = Ho
  name = G4_Ho
  specific = 4
FEATURE [App::DocumentObjectGroupPython] Er_element001  label="Er_element : 1"  # scripted group (container) (typed FeaturePython)
  n = 1
  ref = Er_element
FEATURE [App::DocumentObjectGroupPython] G4_Er  # scripted group (container) (typed FeaturePython)
  Dunit = g/cm3
  Dvalue = 9.066
  Group = -> [Er_element001]
  conduct = 2
  density = 1
  expand = 3
  formula = Er
  name = G4_Er
  specific = 4
FEATURE [App::DocumentObjectGroupPython] Tm_element001  label="Tm_element : 1"  # scripted group (container) (typed FeaturePython)
  n = 1
  ref = Tm_element
FEATURE [App::DocumentObjectGroupPython] G4_Tm  # scripted group (container) (typed FeaturePython)
  Dunit = g/cm3
  Dvalue = 9.321
  Group = -> [Tm_element001]
  conduct = 2
  density = 1
  expand = 3
  formula = Tm
  name = G4_Tm
  specific = 4
FEATURE [App::DocumentObjectGroupPython] Yb_element001  label="Yb_element : 1"  # scripted group (container) (typed FeaturePython)
  n = 1
  ref = Yb_element
FEATURE [App::DocumentObjectGroupPython] G4_Yb  # scripted group (container) (typed FeaturePython)
  Dunit = g/cm3
  Dvalue = 6.73
  Group = -> [Yb_element001]
  conduct = 2
  density = 1
  expand = 3
  formula = Yb
  name = G4_Yb
  specific = 4
FEATURE [App::DocumentObjectGroupPython] Lu_element001  label="Lu_element : 1"  # scripted group (container) (typed FeaturePython)
  n = 1
  ref = Lu_element
FEATURE [App::DocumentObjectGroupPython] G4_Lu  # scripted group (container) (typed FeaturePython)
  Dunit = g/cm3
  Dvalue = 9.84
  Group = -> [Lu_element001]
  conduct = 2
  density = 1
  expand = 3
  formula = Lu
  name = G4_Lu
  specific = 4
FEATURE [App::DocumentObjectGroupPython] Hf_element001  label="Hf_element : 1"  # scripted group (container) (typed FeaturePython)
  n = 1
  ref = Hf_element
FEATURE [App::DocumentObjectGroupPython] G4_Hf  # scripted group (container) (typed FeaturePython)
  Dunit = g/cm3
  Dvalue = 13.31
  Group = -> [Hf_element001]
  conduct = 2
  density = 1
  expand = 3
  formula = Hf
  name = G4_Hf
  specific = 4
FEATURE [App::DocumentObjectGroupPython] Ta_element001  label="Ta_element : 1"  # scripted group (container) (typed FeaturePython)
  n = 1
  ref = Ta_element
FEATURE [App::DocumentObjectGroupPython] G4_Ta  # scripted group (container) (typed FeaturePython)
  Dunit = g/cm3
  Dvalue = 16.654
  Group = -> [Ta_element001]
  conduct = 2
  density = 1
  expand = 3
  formula = Ta
  name = G4_Ta
  specific = 4
FEATURE [App::DocumentObjectGroupPython] W_element004  label="W_element : 004"  # scripted group (container) (typed FeaturePython)
  n = 1
  ref = W_element
FEATURE [App::DocumentObjectGroupPython] G4_W  # scripted group (container) (typed FeaturePython)
  Dunit = g/cm3
  Dvalue = 19.3
  Group = -> [W_element004]
  conduct = 2
  density = 1
  expand = 3
  formula = W
  name = G4_W
  specific = 4
FEATURE [App::DocumentObjectGroupPython] Re_element001  label="Re_element : 1"  # scripted group (container) (typed FeaturePython)
  n = 1
  ref = Re_element
FEATURE [App::DocumentObjectGroupPython] G4_Re  # scripted group (container) (typed FeaturePython)
  Dunit = g/cm3
  Dvalue = 21.02
  Group = -> [Re_element001]
  conduct = 2
  density = 1
  expand = 3
  formula = Re
  name = G4_Re
  specific = 4
FEATURE [App::DocumentObjectGroupPython] Os_element001  label="Os_element : 1"  # scripted group (container) (typed FeaturePython)
  n = 1
  ref = Os_element
FEATURE [App::DocumentObjectGroupPython] G4_Os  # scripted group (container) (typed FeaturePython)
  Dunit = g/cm3
  Dvalue = 22.57
  Group = -> [Os_element001]
  conduct = 2
  density = 1
  expand = 3
  formula = Os
  name = G4_Os
  specific = 4
FEATURE [App::DocumentObjectGroupPython] Ir_element001  label="Ir_element : 1"  # scripted group (container) (typed FeaturePython)
  n = 1
  ref = Ir_element
FEATURE [App::DocumentObjectGroupPython] G4_Ir  # scripted group (container) (typed FeaturePython)
  Dunit = g/cm3
  Dvalue = 22.42
  Group = -> [Ir_element001]
  conduct = 2
  density = 1
  expand = 3
  formula = Ir
  name = G4_Ir
  specific = 4
FEATURE [App::DocumentObjectGroupPython] Pt_element001  label="Pt_element : 1"  # scripted group (container) (typed FeaturePython)
  n = 1
  ref = Pt_element
FEATURE [App::DocumentObjectGroupPython] G4_Pt  # scripted group (container) (typed FeaturePython)
  Dunit = g/cm3
  Dvalue = 21.45
  Group = -> [Pt_element001]
  conduct = 2
  density = 1
  expand = 3
  formula = Pt
  name = G4_Pt
  specific = 4
FEATURE [App::DocumentObjectGroupPython] Au_element001  label="Au_element : 1"  # scripted group (container) (typed FeaturePython)
  n = 1
  ref = Au_element
FEATURE [App::DocumentObjectGroupPython] G4_Au  # scripted group (container) (typed FeaturePython)
  Dunit = g/cm3
  Dvalue = 19.32
  Group = -> [Au_element001]
  conduct = 2
  density = 1
  expand = 3
  formula = Au
  name = G4_Au
  specific = 4
FEATURE [App::DocumentObjectGroupPython] Hg_element002  label="Hg_element : 002"  # scripted group (container) (typed FeaturePython)
  n = 1
  ref = Hg_element
FEATURE [App::DocumentObjectGroupPython] G4_Hg  # scripted group (container) (typed FeaturePython)
  Dunit = g/cm3
  Dvalue = 13.546
  Group = -> [Hg_element002]
  conduct = 2
  density = 1
  expand = 3
  formula = Hg
  name = G4_Hg
  specific = 4
FEATURE [App::DocumentObjectGroupPython] Tl_element002  label="Tl_element : 002"  # scripted group (container) (typed FeaturePython)
  n = 1
  ref = Tl_element
FEATURE [App::DocumentObjectGroupPython] G4_Tl  # scripted group (container) (typed FeaturePython)
  Dunit = g/cm3
  Dvalue = 11.72
  Group = -> [Tl_element002]
  conduct = 2
  density = 1
  expand = 3
  formula = Tl
  name = G4_Tl
  specific = 4
FEATURE [App::DocumentObjectGroupPython] Pb_element003  label="Pb_element : 1"  # scripted group (container) (typed FeaturePython)
  n = 1
  ref = Pb_element
FEATURE [App::DocumentObjectGroupPython] G4_Pb  # scripted group (container) (typed FeaturePython)
  Dunit = g/cm3
  Dvalue = 11.35
  Group = -> [Pb_element003]
  conduct = 2
  density = 1
  expand = 3
  formula = Pb
  name = G4_Pb
  specific = 4
FEATURE [App::DocumentObjectGroupPython] Bi_element002  label="Bi_element : 1"  # scripted group (container) (typed FeaturePython)
  n = 1
  ref = Bi_element
FEATURE [App::DocumentObjectGroupPython] G4_Bi  # scripted group (container) (typed FeaturePython)
  Dunit = g/cm3
  Dvalue = 9.747
  Group = -> [Bi_element002]
  conduct = 2
  density = 1
  expand = 3
  formula = Bi
  name = G4_Bi
  specific = 4
FEATURE [App::DocumentObjectGroupPython] Po_element001  label="Po_element : 1"  # scripted group (container) (typed FeaturePython)
  n = 1
  ref = Po_element
FEATURE [App::DocumentObjectGroupPython] G4_Po  # scripted group (container) (typed FeaturePython)
  Dunit = g/cm3
  Dvalue = 9.32
  Group = -> [Po_element001]
  conduct = 2
  density = 1
  expand = 3
  formula = Po
  name = G4_Po
  specific = 4
FEATURE [App::DocumentObjectGroupPython] At_element001  label="At_element : 1"  # scripted group (container) (typed FeaturePython)
  n = 1
  ref = At_element
FEATURE [App::DocumentObjectGroupPython] G4_At  # scripted group (container) (typed FeaturePython)
  Dunit = g/cm3
  Dvalue = 9.32
  Group = -> [At_element001]
  conduct = 2
  density = 1
  expand = 3
  formula = At
  name = G4_At
  specific = 4
FEATURE [App::DocumentObjectGroupPython] Rn_element001  label="Rn_element : 1"  # scripted group (container) (typed FeaturePython)
  n = 1
  ref = Rn_element
FEATURE [App::DocumentObjectGroupPython] G4_Rn  # scripted group (container) (typed FeaturePython)
  Dunit = g/cm3
  Dvalue = 0.00900662
  Group = -> [Rn_element001]
  conduct = 2
  density = 1
  expand = 3
  formula = Rn
  name = G4_Rn
  specific = 4
FEATURE [App::DocumentObjectGroupPython] Fr_element001  label="Fr_element : 1"  # scripted group (container) (typed FeaturePython)
  n = 1
  ref = Fr_element
FEATURE [App::DocumentObjectGroupPython] G4_Fr  # scripted group (container) (typed FeaturePython)
  Dunit = g/cm3
  Dvalue = 1
  Group = -> [Fr_element001]
  conduct = 2
  density = 1
  expand = 3
  formula = Fr
  name = G4_Fr
  specific = 4
FEATURE [App::DocumentObjectGroupPython] Ra_element001  label="Ra_element : 1"  # scripted group (container) (typed FeaturePython)
  n = 1
  ref = Ra_element
FEATURE [App::DocumentObjectGroupPython] G4_Ra  # scripted group (container) (typed FeaturePython)
  Dunit = g/cm3
  Dvalue = 5
  Group = -> [Ra_element001]
  conduct = 2
  density = 1
  expand = 3
  formula = Ra
  name = G4_Ra
  specific = 4
FEATURE [App::DocumentObjectGroupPython] Ac_element001  label="Ac_element : 1"  # scripted group (container) (typed FeaturePython)
  n = 1
  ref = Ac_element
FEATURE [App::DocumentObjectGroupPython] G4_Ac  # scripted group (container) (typed FeaturePython)
  Dunit = g/cm3
  Dvalue = 10.07
  Group = -> [Ac_element001]
  conduct = 2
  density = 1
  expand = 3
  formula = Ac
  name = G4_Ac
  specific = 4
FEATURE [App::DocumentObjectGroupPython] Th_element001  label="Th_element : 1"  # scripted group (container) (typed FeaturePython)
  n = 1
  ref = Th_element
FEATURE [App::DocumentObjectGroupPython] G4_Th  # scripted group (container) (typed FeaturePython)
  Dunit = g/cm3
  Dvalue = 11.72
  Group = -> [Th_element001]
  conduct = 2
  density = 1
  expand = 3
  formula = Th
  name = G4_Th
  specific = 4
FEATURE [App::DocumentObjectGroupPython] Pa_element001  label="Pa_element : 1"  # scripted group (container) (typed FeaturePython)
  n = 1
  ref = Pa_element
FEATURE [App::DocumentObjectGroupPython] G4_Pa  # scripted group (container) (typed FeaturePython)
  Dunit = g/cm3
  Dvalue = 15.37
  Group = -> [Pa_element001]
  conduct = 2
  density = 1
  expand = 3
  formula = Pa
  name = G4_Pa
  specific = 4
FEATURE [App::DocumentObjectGroupPython] U_element004  label="U_element : 004"  # scripted group (container) (typed FeaturePython)
  n = 1
  ref = U_element
FEATURE [App::DocumentObjectGroupPython] G4_U  # scripted group (container) (typed FeaturePython)
  Dunit = g/cm3
  Dvalue = 18.95
  Group = -> [U_element004]
  conduct = 2
  density = 1
  expand = 3
  formula = U
  name = G4_U
  specific = 4
FEATURE [App::DocumentObjectGroupPython] Np_element001  label="Np_element : 1"  # scripted group (container) (typed FeaturePython)
  n = 1
  ref = Np_element
FEATURE [App::DocumentObjectGroupPython] G4_Np  # scripted group (container) (typed FeaturePython)
  Dunit = g/cm3
  Dvalue = 20.25
  Group = -> [Np_element001]
  conduct = 2
  density = 1
  expand = 3
  formula = Np
  name = G4_Np
  specific = 4
FEATURE [App::DocumentObjectGroupPython] Pu_element002  label="Pu_element : 002"  # scripted group (container) (typed FeaturePython)
  n = 1
  ref = Pu_element
FEATURE [App::DocumentObjectGroupPython] G4_Pu  # scripted group (container) (typed FeaturePython)
  Dunit = g/cm3
  Dvalue = 19.84
  Group = -> [Pu_element002]
  conduct = 2
  density = 1
  expand = 3
  formula = Pu
  name = G4_Pu
  specific = 4
FEATURE [App::DocumentObjectGroupPython] Am_element001  label="Am_element : 1"  # scripted group (container) (typed FeaturePython)
  n = 1
  ref = Am_element
FEATURE [App::DocumentObjectGroupPython] G4_Am  # scripted group (container) (typed FeaturePython)
  Dunit = g/cm3
  Dvalue = 13.67
  Group = -> [Am_element001]
  conduct = 2
  density = 1
  expand = 3
  formula = Am
  name = G4_Am
  specific = 4
FEATURE [App::DocumentObjectGroupPython] Cm_element001  label="Cm_element : 1"  # scripted group (container) (typed FeaturePython)
  n = 1
  ref = Cm_element
FEATURE [App::DocumentObjectGroupPython] G4_Cm  # scripted group (container) (typed FeaturePython)
  Dunit = g/cm3
  Dvalue = 13.51
  Group = -> [Cm_element001]
  conduct = 2
  density = 1
  expand = 3
  formula = Cm
  name = G4_Cm
  specific = 4
FEATURE [App::DocumentObjectGroupPython] Bk_element001  label="Bk_element : 1"  # scripted group (container) (typed FeaturePython)
  n = 1
  ref = Bk_element
FEATURE [App::DocumentObjectGroupPython] G4_Bk  # scripted group (container) (typed FeaturePython)
  Dunit = g/cm3
  Dvalue = 14
  Group = -> [Bk_element001]
  conduct = 2
  density = 1
  expand = 3
  formula = Bk
  name = G4_Bk
  specific = 4
FEATURE [App::DocumentObjectGroupPython] Cf_element001  label="Cf_element : 1"  # scripted group (container) (typed FeaturePython)
  n = 1
  ref = Cf_element
FEATURE [App::DocumentObjectGroupPython] G4_Cf  # scripted group (container) (typed FeaturePython)
  Dunit = g/cm3
  Dvalue = 10
  Group = -> [Cf_element001]
  conduct = 2
  density = 1
  expand = 3
  formula = Cf
  name = G4_Cf
  specific = 4
FEATURE [App::DocumentObjectGroupPython] Element  # scripted group (container) (typed FeaturePython)
  Group = -> [G4_H,G4_He,G4_Li,G4_Be,G4_B,G4_C,G4_N,G4_O,G4_F,G4_Ne,G4_Na,G4_Mg,G4_Al,G4_Si,G4_P,G4_S,G4_Cl,G4_Ar,G4_K,G4_Ca,G4_Sc,G4_Ti,G4_V,G4_Cr,G4_Mn,G4_Fe,G4_Co,G4_Ni,G4_Cu,G4_Zn,G4_Ga,G4_Ge,G4_As,G4_Se,G4_Br,G4_Kr,G4_Rb,G4_Sr,G4_Y,G4_Zr,G4_Nb,G4_Mo,G4_Tc,G4_Ru,G4_Rh,G4_Pd,G4_Ag,G4_Cd,G4_In,G4_Sn,G4_Sb,G4_Te,G4_I,G4_Xe,G4_Cs,G4_Ba,G4_La,G4_Ce,G4_Pr,G4_Nd,G4_Pm,G4_Sm,G4_Eu,G4_Gd,G4_Tb,G4_Dy,G4_Ho,G4_Er,+30 more]
FEATURE [App::DocumentObjectGroupPython] H_element114  label="H_element : 063"  # scripted group (container) (typed FeaturePython)
  n = 2
  ref = H_element
FEATURE [App::DocumentObjectGroupPython] G4_lH2  # scripted group (container) (typed FeaturePython)
  Dunit = g/cm3
  Dvalue = 0.0708
  Group = -> [H_element114]
  conduct = 2
  density = 1
  expand = 3
  formula = G4_lH2
  name = G4_lH2
  specific = 4
FEATURE [App::DocumentObjectGroupPython] N_element049  label="N_element : 022"  # scripted group (container) (typed FeaturePython)
  n = 2
  ref = N_element
FEATURE [App::DocumentObjectGroupPython] G4_lN2  # scripted group (container) (typed FeaturePython)
  Dunit = g/cm3
  Dvalue = 0.807
  Group = -> [N_element049]
  conduct = 2
  density = 1
  expand = 3
  formula = G4_lN2
  name = G4_lN2
  specific = 4
FEATURE [App::DocumentObjectGroupPython] O_element106  label="O_element : 060"  # scripted group (container) (typed FeaturePython)
  n = 2
  ref = O_element
FEATURE [App::DocumentObjectGroupPython] G4_lO2  # scripted group (container) (typed FeaturePython)
  Dunit = g/cm3
  Dvalue = 1.141
  Group = -> [O_element106]
  conduct = 2
  density = 1
  expand = 3
  formula = G4_lO2
  name = G4_lO2
  specific = 4
FEATURE [App::DocumentObjectGroupPython] Ar  label="Ar : 1"  # scripted group (container) (typed FeaturePython)
  n = 1
  ref = Ar
FEATURE [App::DocumentObjectGroupPython] G4_lAr  # scripted group (container) (typed FeaturePython)
  Dunit = g/cm3
  Dvalue = 1.396
  Group = -> [Ar]
  conduct = 2
  density = 1
  expand = 3
  formula = G4_lAr
  name = G4_lAr
  specific = 4
FEATURE [App::DocumentObjectGroupPython] Br  label="Br : 1"  # scripted group (container) (typed FeaturePython)
  n = 1
  ref = Br
FEATURE [App::DocumentObjectGroupPython] G4_lBr  # scripted group (container) (typed FeaturePython)
  Dunit = g/cm3
  Dvalue = 3.1028
  Group = -> [Br]
  conduct = 2
  density = 1
  expand = 3
  formula = G4_lBr
  name = G4_lBr
  specific = 4
FEATURE [App::DocumentObjectGroupPython] Kr  label="Kr : 1"  # scripted group (container) (typed FeaturePython)
  n = 1
  ref = Kr
FEATURE [App::DocumentObjectGroupPython] G4_lKr  # scripted group (container) (typed FeaturePython)
  Dunit = g/cm3
  Dvalue = 2.418
  Group = -> [Kr]
  conduct = 2
  density = 1
  expand = 3
  formula = G4_lKr
  name = G4_lKr
  specific = 4
FEATURE [App::DocumentObjectGroupPython] Xe  label="Xe : 1"  # scripted group (container) (typed FeaturePython)
  n = 1
  ref = Xe
FEATURE [App::DocumentObjectGroupPython] G4_lXe  # scripted group (container) (typed FeaturePython)
  Dunit = g/cm3
  Dvalue = 2.953
  Group = -> [Xe]
  conduct = 2
  density = 1
  expand = 3
  formula = G4_lXe
  name = G4_lXe
  specific = 4
FEATURE [App::DocumentObjectGroupPython] O_element107  label="O_element : 061"  # scripted group (container) (typed FeaturePython)
  n = 4
  ref = O_element
FEATURE [App::DocumentObjectGroupPython] Pb_element004  label="Pb_element : 002"  # scripted group (container) (typed FeaturePython)
  n = 1
  ref = Pb_element
FEATURE [App::DocumentObjectGroupPython] W_element005  label="W_element : 005"  # scripted group (container) (typed FeaturePython)
  n = 1
  ref = W_element
FEATURE [App::DocumentObjectGroupPython] G4_PbWO4  # scripted group (container) (typed FeaturePython)
  Dunit = g/cm3
  Dvalue = 8.28
  Group = -> [O_element107,Pb_element004,W_element005]
  conduct = 2
  density = 1
  expand = 3
  formula = G4_PbWO4
  name = G4_PbWO4
  specific = 4
FEATURE [App::DocumentObjectGroupPython] alactic  label="alactic : 1"  # scripted group (container) (typed FeaturePython)
  n = 1
  ref = alactic
FEATURE [App::DocumentObjectGroupPython] G4_Galactic  # scripted group (container) (typed FeaturePython)
  Dunit = g/cm3
  Dvalue = 0
  Group = -> [alactic]
  conduct = 2
  density = 1
  expand = 3
  formula = G4_Galactic
  name = G4_Galactic
  specific = 4
FEATURE [App::DocumentObjectGroupPython] RAPHITE_POROUS  label="RAPHITE_POROUS : 1"  # scripted group (container) (typed FeaturePython)
  n = 1
  ref = RAPHITE_POROUS
FEATURE [App::DocumentObjectGroupPython] G4_GRAPHITE_POROUS  # scripted group (container) (typed FeaturePython)
  Dunit = g/cm3
  Dvalue = 1.7
  Group = -> [RAPHITE_POROUS]
  conduct = 2
  density = 1
  expand = 3
  formula = G4_GRAPHITE_POROUS
  name = G4_GRAPHITE_POROUS
  specific = 4
FEATURE [App::DocumentObjectGroupPython] H_element115  label="H_element : 0.150"  # scripted group (container) (typed FeaturePython)
  n = 0.080538
FEATURE [App::DocumentObjectGroupPython] C_element125  label="C_element : 0.600"  # scripted group (container) (typed FeaturePython)
  n = 0.599848
FEATURE [App::DocumentObjectGroupPython] O_element108  label="O_element : 0.320"  # scripted group (container) (typed FeaturePython)
  n = 0.319614
FEATURE [App::DocumentObjectGroupPython] G4_LUCITE  # scripted group (container) (typed FeaturePython)
  Dunit = g/cm3
  Dvalue = 1.19
  Group = -> [H_element115,C_element125,O_element108]
  conduct = 2
  density = 1
  expand = 3
  formula = G4_LUCITE
  name = G4_LUCITE
  specific = 4
FEATURE [App::DocumentObjectGroupPython] Cu_element002  label="Cu_element : 62"  # scripted group (container) (typed FeaturePython)
  n = 62
  ref = Cu_element
FEATURE [App::DocumentObjectGroupPython] Zn_element002  label="Zn_element : 35"  # scripted group (container) (typed FeaturePython)
  n = 35
  ref = Zn_element
FEATURE [App::DocumentObjectGroupPython] Pb_element005  label="Pb_element : 3"  # scripted group (container) (typed FeaturePython)
  n = 3
  ref = Pb_element
FEATURE [App::DocumentObjectGroupPython] G4_BRASS  # scripted group (container) (typed FeaturePython)
  Dunit = g/cm3
  Dvalue = 8.52
  Group = -> [Cu_element002,Zn_element002,Pb_element005]
  conduct = 2
  density = 1
  expand = 3
  formula = G4_BRASS
  name = G4_BRASS
  specific = 4
FEATURE [App::DocumentObjectGroupPython] Cu_element003  label="Cu_element : 89"  # scripted group (container) (typed FeaturePython)
  n = 89
  ref = Cu_element
FEATURE [App::DocumentObjectGroupPython] Zn_element003  label="Zn_element : 9"  # scripted group (container) (typed FeaturePython)
  n = 9
  ref = Zn_element
FEATURE [App::DocumentObjectGroupPython] Pb_element006  label="Pb_element : 2"  # scripted group (container) (typed FeaturePython)
  n = 2
  ref = Pb_element
FEATURE [App::DocumentObjectGroupPython] G4_BRONZE  # scripted group (container) (typed FeaturePython)
  Dunit = g/cm3
  Dvalue = 8.82
  Group = -> [Cu_element003,Zn_element003,Pb_element006]
  conduct = 2
  density = 1
  expand = 3
  formula = G4_BRONZE
  name = G4_BRONZE
  specific = 4
FEATURE [App::DocumentObjectGroupPython] Fe_element008  label="Fe_element : 74"  # scripted group (container) (typed FeaturePython)
  n = 74
  ref = Fe_element
FEATURE [App::DocumentObjectGroupPython] Cr_element002  label="Cr_element : 18"  # scripted group (container) (typed FeaturePython)
  n = 18
  ref = Cr_element
FEATURE [App::DocumentObjectGroupPython] Ni_element002  label="Ni_element : 8"  # scripted group (container) (typed FeaturePython)
  n = 8
  ref = Ni_element
FEATURE [App::DocumentObjectGroupPython] G4_STAINLESS_STEEL  label="G4_STAINLESS-STEEL"  # scripted group (container) (typed FeaturePython)
  Dunit = g/cm3
  Dvalue = 8
  Group = -> [Fe_element008,Cr_element002,Ni_element002]
  conduct = 2
  density = 1
  expand = 3
  formula = G4_STAINLESS-STEEL
  name = G4_STAINLESS-STEEL
  specific = 4
FEATURE [App::DocumentObjectGroupPython] H_element116  label="H_element : 064"  # scripted group (container) (typed FeaturePython)
  n = 18
  ref = H_element
FEATURE [App::DocumentObjectGroupPython] C_element126  label="C_element : 071"  # scripted group (container) (typed FeaturePython)
  n = 12
  ref = C_element
FEATURE [App::DocumentObjectGroupPython] O_element109  label="O_element : 062"  # scripted group (container) (typed FeaturePython)
  n = 7
  ref = O_element
FEATURE [App::DocumentObjectGroupPython] G4_CR39  # scripted group (container) (typed FeaturePython)
  Dunit = g/cm3
  Dvalue = 1.32
  Group = -> [H_element116,C_element126,O_element109]
  conduct = 2
  density = 1
  expand = 3
  formula = G4_CR39
  name = G4_CR39
  specific = 4
FEATURE [App::DocumentObjectGroupPython] H_element117  label="H_element : 38"  # scripted group (container) (typed FeaturePython)
  n = 38
  ref = H_element
FEATURE [App::DocumentObjectGroupPython] C_element127  label="C_element : 072"  # scripted group (container) (typed FeaturePython)
  n = 18
  ref = C_element
FEATURE [App::DocumentObjectGroupPython] O_element110  label="O_element : 063"  # scripted group (container) (typed FeaturePython)
  n = 1
  ref = O_element
FEATURE [App::DocumentObjectGroupPython] G4_OCTADECANOL  # scripted group (container) (typed FeaturePython)
  Dunit = g/cm3
  Dvalue = 0.812
  Group = -> [H_element117,C_element127,O_element110]
  conduct = 2
  density = 1
  expand = 3
  formula = G4_OCTADECANOL
  name = G4_OCTADECANOL
  specific = 4
FEATURE [App::DocumentObjectGroupPython] HEP  # scripted group (container) (typed FeaturePython)
  Group = -> [G4_lH2,G4_lN2,G4_lO2,G4_lAr,G4_lBr,G4_lKr,G4_lXe,G4_PbWO4,G4_Galactic,G4_GRAPHITE_POROUS,G4_LUCITE,G4_BRASS,G4_BRONZE,G4_STAINLESS_STEEL,G4_CR39,G4_OCTADECANOL]
FEATURE [App::DocumentObjectGroupPython] C_element128  label="C_element : 073"  # scripted group (container) (typed FeaturePython)
  n = 14
  ref = C_element
FEATURE [App::DocumentObjectGroupPython] H_element118  label="H_element : 065"  # scripted group (container) (typed FeaturePython)
  n = 10
  ref = H_element
FEATURE [App::DocumentObjectGroupPython] O_element111  label="O_element : 064"  # scripted group (container) (typed FeaturePython)
  n = 2
  ref = O_element
FEATURE [App::DocumentObjectGroupPython] N_element050  label="N_element : 023"  # scripted group (container) (typed FeaturePython)
  n = 2
  ref = N_element
FEATURE [App::DocumentObjectGroupPython] G4_KEVLAR  # scripted group (container) (typed FeaturePython)
  Dunit = g/cm3
  Dvalue = 1.44
  Group = -> [C_element128,H_element118,O_element111,N_element050]
  conduct = 2
  density = 1
  expand = 3
  formula = G4_KEVLAR
  name = G4_KEVLAR
  specific = 4
FEATURE [App::DocumentObjectGroupPython] C_element129  label="C_element : 074"  # scripted group (container) (typed FeaturePython)
  n = 10
  ref = C_element
FEATURE [App::DocumentObjectGroupPython] H_element119  label="H_element : 066"  # scripted group (container) (typed FeaturePython)
  n = 8
  ref = H_element
FEATURE [App::DocumentObjectGroupPython] O_element112  label="O_element : 065"  # scripted group (container) (typed FeaturePython)
  n = 4
  ref = O_element
FEATURE [App::DocumentObjectGroupPython] G4_DACRON  # scripted group (container) (typed FeaturePython)
  Dunit = g/cm3
  Dvalue = 1.4
  Group = -> [C_element129,H_element119,O_element112]
  conduct = 2
  density = 1
  expand = 3
  formula = G4_DACRON
  name = G4_DACRON
  specific = 4
FEATURE [App::DocumentObjectGroupPython] C_element130  label="C_element : 075"  # scripted group (container) (typed FeaturePython)
  n = 4
  ref = C_element
FEATURE [App::DocumentObjectGroupPython] H_element120  label="H_element : 067"  # scripted group (container) (typed FeaturePython)
  n = 5
  ref = H_element
FEATURE [App::DocumentObjectGroupPython] Cl_element030  label="Cl_element : 016"  # scripted group (container) (typed FeaturePython)
  n = 1
  ref = Cl_element
FEATURE [App::DocumentObjectGroupPython] G4_NEOPRENE  # scripted group (container) (typed FeaturePython)
  Dunit = g/cm3
  Dvalue = 1.23
  Group = -> [C_element130,H_element120,Cl_element030]
  conduct = 2
  density = 1
  expand = 3
  formula = G4_NEOPRENE
  name = G4_NEOPRENE
  specific = 4
FEATURE [App::DocumentObjectGroupPython] Space  # scripted group (container) (typed FeaturePython)
  Group = -> [G4_KEVLAR,G4_DACRON,G4_NEOPRENE]
FEATURE [App::DocumentObjectGroupPython] H_element121  label="H_element : 068"  # scripted group (container) (typed FeaturePython)
  n = 5
  ref = H_element
FEATURE [App::DocumentObjectGroupPython] C_element131  label="C_element : 076"  # scripted group (container) (typed FeaturePython)
  n = 4
  ref = C_element
FEATURE [App::DocumentObjectGroupPython] N_element051  label="N_element : 3"  # scripted group (container) (typed FeaturePython)
  n = 3
  ref = N_element
FEATURE [App::DocumentObjectGroupPython] O_element113  label="O_element : 066"  # scripted group (container) (typed FeaturePython)
  n = 1
  ref = O_element
FEATURE [App::DocumentObjectGroupPython] G4_CYTOSINE  # scripted group (container) (typed FeaturePython)
  Dunit = g/cm3
  Dvalue = 1.55
  Group = -> [H_element121,C_element131,N_element051,O_element113]
  conduct = 2
  density = 1
  expand = 3
  formula = G4_CYTOSINE
  name = G4_CYTOSINE
  specific = 4
FEATURE [App::DocumentObjectGroupPython] H_element122  label="H_element : 069"  # scripted group (container) (typed FeaturePython)
  n = 6
  ref = H_element
FEATURE [App::DocumentObjectGroupPython] C_element132  label="C_element : 077"  # scripted group (container) (typed FeaturePython)
  n = 5
  ref = C_element
FEATURE [App::DocumentObjectGroupPython] N_element052  label="N_element : 024"  # scripted group (container) (typed FeaturePython)
  n = 2
  ref = N_element
FEATURE [App::DocumentObjectGroupPython] O_element114  label="O_element : 067"  # scripted group (container) (typed FeaturePython)
  n = 2
  ref = O_element
FEATURE [App::DocumentObjectGroupPython] G4_THYMINE  # scripted group (container) (typed FeaturePython)
  Dunit = g/cm3
  Dvalue = 1.23
  Group = -> [H_element122,C_element132,N_element052,O_element114]
  conduct = 2
  density = 1
  expand = 3
  formula = G4_THYMINE
  name = G4_THYMINE
  specific = 4
FEATURE [App::DocumentObjectGroupPython] H_element123  label="H_element : 070"  # scripted group (container) (typed FeaturePython)
  n = 4
  ref = H_element
FEATURE [App::DocumentObjectGroupPython] C_element133  label="C_element : 078"  # scripted group (container) (typed FeaturePython)
  n = 4
  ref = C_element
FEATURE [App::DocumentObjectGroupPython] N_element053  label="N_element : 025"  # scripted group (container) (typed FeaturePython)
  n = 2
  ref = N_element
FEATURE [App::DocumentObjectGroupPython] O_element115  label="O_element : 068"  # scripted group (container) (typed FeaturePython)
  n = 2
  ref = O_element
FEATURE [App::DocumentObjectGroupPython] G4_URACIL  # scripted group (container) (typed FeaturePython)
  Dunit = g/cm3
  Dvalue = 1.32
  Group = -> [H_element123,C_element133,N_element053,O_element115]
  conduct = 2
  density = 1
  expand = 3
  formula = G4_URACIL
  name = G4_URACIL
  specific = 4
FEATURE [App::DocumentObjectGroupPython] H_element124  label="H_element : 071"  # scripted group (container) (typed FeaturePython)
  n = 4
  ref = H_element
FEATURE [App::DocumentObjectGroupPython] C_element134  label="C_element : 079"  # scripted group (container) (typed FeaturePython)
  n = 5
  ref = C_element
FEATURE [App::DocumentObjectGroupPython] N_element054  label="N_element : 026"  # scripted group (container) (typed FeaturePython)
  n = 5
  ref = N_element
FEATURE [App::DocumentObjectGroupPython] G4_DNA_ADENINE  # scripted group (container) (typed FeaturePython)
  Dunit = g/cm3
  Dvalue = 1
  Group = -> [H_element124,C_element134,N_element054]
  conduct = 2
  density = 1
  expand = 3
  formula = G4_DNA_ADENINE
  name = G4_DNA_ADENINE
  specific = 4
FEATURE [App::DocumentObjectGroupPython] H_element125  label="H_element : 072"  # scripted group (container) (typed FeaturePython)
  n = 4
  ref = H_element
FEATURE [App::DocumentObjectGroupPython] C_element135  label="C_element : 080"  # scripted group (container) (typed FeaturePython)
  n = 5
  ref = C_element
FEATURE [App::DocumentObjectGroupPython] N_element055  label="N_element : 027"  # scripted group (container) (typed FeaturePython)
  n = 5
  ref = N_element
FEATURE [App::DocumentObjectGroupPython] O_element116  label="O_element : 069"  # scripted group (container) (typed FeaturePython)
  n = 1
  ref = O_element
FEATURE [App::DocumentObjectGroupPython] G4_DNA_GUANINE  # scripted group (container) (typed FeaturePython)
  Dunit = g/cm3
  Dvalue = 1
  Group = -> [H_element125,C_element135,N_element055,O_element116]
  conduct = 2
  density = 1
  expand = 3
  formula = G4_DNA_GUANINE
  name = G4_DNA_GUANINE
  specific = 4
FEATURE [App::DocumentObjectGroupPython] H_element126  label="H_element : 073"  # scripted group (container) (typed FeaturePython)
  n = 4
  ref = H_element
FEATURE [App::DocumentObjectGroupPython] C_element136  label="C_element : 081"  # scripted group (container) (typed FeaturePython)
  n = 4
  ref = C_element
FEATURE [App::DocumentObjectGroupPython] N_element056  label="N_element : 028"  # scripted group (container) (typed FeaturePython)
  n = 3
  ref = N_element
FEATURE [App::DocumentObjectGroupPython] O_element117  label="O_element : 070"  # scripted group (container) (typed FeaturePython)
  n = 1
  ref = O_element
FEATURE [App::DocumentObjectGroupPython] G4_DNA_CYTOSINE  # scripted group (container) (typed FeaturePython)
  Dunit = g/cm3
  Dvalue = 1
  Group = -> [H_element126,C_element136,N_element056,O_element117]
  conduct = 2
  density = 1
  expand = 3
  formula = G4_DNA_CYTOSINE
  name = G4_DNA_CYTOSINE
  specific = 4
FEATURE [App::DocumentObjectGroupPython] H_element127  label="H_element : 074"  # scripted group (container) (typed FeaturePython)
  n = 5
  ref = H_element
FEATURE [App::DocumentObjectGroupPython] C_element137  label="C_element : 082"  # scripted group (container) (typed FeaturePython)
  n = 5
  ref = C_element
FEATURE [App::DocumentObjectGroupPython] N_element057  label="N_element : 029"  # scripted group (container) (typed FeaturePython)
  n = 2
  ref = N_element
FEATURE [App::DocumentObjectGroupPython] O_element118  label="O_element : 071"  # scripted group (container) (typed FeaturePython)
  n = 2
  ref = O_element
FEATURE [App::DocumentObjectGroupPython] G4_DNA_THYMINE  # scripted group (container) (typed FeaturePython)
  Dunit = g/cm3
  Dvalue = 1
  Group = -> [H_element127,C_element137,N_element057,O_element118]
  conduct = 2
  density = 1
  expand = 3
  formula = G4_DNA_THYMINE
  name = G4_DNA_THYMINE
  specific = 4
FEATURE [App::DocumentObjectGroupPython] H_element128  label="H_element : 075"  # scripted group (container) (typed FeaturePython)
  n = 3
  ref = H_element
FEATURE [App::DocumentObjectGroupPython] C_element138  label="C_element : 083"  # scripted group (container) (typed FeaturePython)
  n = 4
  ref = C_element
FEATURE [App::DocumentObjectGroupPython] N_element058  label="N_element : 030"  # scripted group (container) (typed FeaturePython)
  n = 2
  ref = N_element
FEATURE [App::DocumentObjectGroupPython] O_element119  label="O_element : 072"  # scripted group (container) (typed FeaturePython)
  n = 2
  ref = O_element
FEATURE [App::DocumentObjectGroupPython] G4_DNA_URACIL  # scripted group (container) (typed FeaturePython)
  Dunit = g/cm3
  Dvalue = 1
  Group = -> [H_element128,C_element138,N_element058,O_element119]
  conduct = 2
  density = 1
  expand = 3
  formula = G4_DNA_URACIL
  name = G4_DNA_URACIL
  specific = 4
FEATURE [App::DocumentObjectGroupPython] H_element129  label="H_element : 076"  # scripted group (container) (typed FeaturePython)
  n = 10
  ref = H_element
FEATURE [App::DocumentObjectGroupPython] C_element139  label="C_element : 084"  # scripted group (container) (typed FeaturePython)
  n = 10
  ref = C_element
FEATURE [App::DocumentObjectGroupPython] N_element059  label="N_element : 031"  # scripted group (container) (typed FeaturePython)
  n = 5
  ref = N_element
FEATURE [App::DocumentObjectGroupPython] O_element120  label="O_element : 073"  # scripted group (container) (typed FeaturePython)
  n = 4
  ref = O_element
FEATURE [App::DocumentObjectGroupPython] G4_DNA_ADENOSINE  # scripted group (container) (typed FeaturePython)
  Dunit = g/cm3
  Dvalue = 1
  Group = -> [H_element129,C_element139,N_element059,O_element120]
  conduct = 2
  density = 1
  expand = 3
  formula = G4_DNA_ADENOSINE
  name = G4_DNA_ADENOSINE
  specific = 4
FEATURE [App::DocumentObjectGroupPython] H_element130  label="H_element : 077"  # scripted group (container) (typed FeaturePython)
  n = 10
  ref = H_element
FEATURE [App::DocumentObjectGroupPython] C_element140  label="C_element : 085"  # scripted group (container) (typed FeaturePython)
  n = 10
  ref = C_element
FEATURE [App::DocumentObjectGroupPython] N_element060  label="N_element : 032"  # scripted group (container) (typed FeaturePython)
  n = 5
  ref = N_element
FEATURE [App::DocumentObjectGroupPython] O_element121  label="O_element : 074"  # scripted group (container) (typed FeaturePython)
  n = 5
  ref = O_element
FEATURE [App::DocumentObjectGroupPython] G4_DNA_GUANOSINE  # scripted group (container) (typed FeaturePython)
  Dunit = g/cm3
  Dvalue = 1
  Group = -> [H_element130,C_element140,N_element060,O_element121]
  conduct = 2
  density = 1
  expand = 3
  formula = G4_DNA_GUANOSINE
  name = G4_DNA_GUANOSINE
  specific = 4
FEATURE [App::DocumentObjectGroupPython] H_element131  label="H_element : 078"  # scripted group (container) (typed FeaturePython)
  n = 10
  ref = H_element
FEATURE [App::DocumentObjectGroupPython] C_element141  label="C_element : 086"  # scripted group (container) (typed FeaturePython)
  n = 9
  ref = C_element
FEATURE [App::DocumentObjectGroupPython] N_element061  label="N_element : 033"  # scripted group (container) (typed FeaturePython)
  n = 3
  ref = N_element
FEATURE [App::DocumentObjectGroupPython] O_element122  label="O_element : 075"  # scripted group (container) (typed FeaturePython)
  n = 5
  ref = O_element
FEATURE [App::DocumentObjectGroupPython] G4_DNA_CYTIDINE  # scripted group (container) (typed FeaturePython)
  Dunit = g/cm3
  Dvalue = 1
  Group = -> [H_element131,C_element141,N_element061,O_element122]
  conduct = 2
  density = 1
  expand = 3
  formula = G4_DNA_CYTIDINE
  name = G4_DNA_CYTIDINE
  specific = 4
FEATURE [App::DocumentObjectGroupPython] H_element132  label="H_element : 079"  # scripted group (container) (typed FeaturePython)
  n = 9
  ref = H_element
FEATURE [App::DocumentObjectGroupPython] C_element142  label="C_element : 087"  # scripted group (container) (typed FeaturePython)
  n = 9
  ref = C_element
FEATURE [App::DocumentObjectGroupPython] N_element062  label="N_element : 034"  # scripted group (container) (typed FeaturePython)
  n = 2
  ref = N_element
FEATURE [App::DocumentObjectGroupPython] O_element123  label="O_element : 076"  # scripted group (container) (typed FeaturePython)
  n = 6
  ref = O_element
FEATURE [App::DocumentObjectGroupPython] G4_DNA_URIDINE  # scripted group (container) (typed FeaturePython)
  Dunit = g/cm3
  Dvalue = 1
  Group = -> [H_element132,C_element142,N_element062,O_element123]
  conduct = 2
  density = 1
  expand = 3
  formula = G4_DNA_URIDINE
  name = G4_DNA_URIDINE
  specific = 4
FEATURE [App::DocumentObjectGroupPython] H_element133  label="H_element : 080"  # scripted group (container) (typed FeaturePython)
  n = 11
  ref = H_element
FEATURE [App::DocumentObjectGroupPython] C_element143  label="C_element : 088"  # scripted group (container) (typed FeaturePython)
  n = 10
  ref = C_element
FEATURE [App::DocumentObjectGroupPython] N_element063  label="N_element : 035"  # scripted group (container) (typed FeaturePython)
  n = 2
  ref = N_element
FEATURE [App::DocumentObjectGroupPython] O_element124  label="O_element : 077"  # scripted group (container) (typed FeaturePython)
  n = 6
  ref = O_element
FEATURE [App::DocumentObjectGroupPython] G4_DNA_METHYLURIDINE  # scripted group (container) (typed FeaturePython)
  Dunit = g/cm3
  Dvalue = 1
  Group = -> [H_element133,C_element143,N_element063,O_element124]
  conduct = 2
  density = 1
  expand = 3
  formula = G4_DNA_METHYLURIDINE
  name = G4_DNA_METHYLURIDINE
  specific = 4
FEATURE [App::DocumentObjectGroupPython] P_element014  label="P_element : 003"  # scripted group (container) (typed FeaturePython)
  n = 1
  ref = P_element
FEATURE [App::DocumentObjectGroupPython] O_element125  label="O_element : 078"  # scripted group (container) (typed FeaturePython)
  n = 3
  ref = O_element
FEATURE [App::DocumentObjectGroupPython] G4_DNA_MONOPHOSPHATE  # scripted group (container) (typed FeaturePython)
  Dunit = g/cm3
  Dvalue = 1
  Group = -> [P_element014,O_element125]
  conduct = 2
  density = 1
  expand = 3
  formula = G4_DNA_MONOPHOSPHATE
  name = G4_DNA_MONOPHOSPHATE
  specific = 4
FEATURE [App::DocumentObjectGroupPython] H_element134  label="H_element : 081"  # scripted group (container) (typed FeaturePython)
  n = 10
  ref = H_element
FEATURE [App::DocumentObjectGroupPython] C_element144  label="C_element : 089"  # scripted group (container) (typed FeaturePython)
  n = 10
  ref = C_element
FEATURE [App::DocumentObjectGroupPython] N_element064  label="N_element : 036"  # scripted group (container) (typed FeaturePython)
  n = 5
  ref = N_element
FEATURE [App::DocumentObjectGroupPython] O_element126  label="O_element : 079"  # scripted group (container) (typed FeaturePython)
  n = 7
  ref = O_element
FEATURE [App::DocumentObjectGroupPython] P_element015  label="P_element : 004"  # scripted group (container) (typed FeaturePython)
  n = 1
  ref = P_element
FEATURE [App::DocumentObjectGroupPython] G4_DNA_A  # scripted group (container) (typed FeaturePython)
  Dunit = g/cm3
  Dvalue = 1
  Group = -> [H_element134,C_element144,N_element064,O_element126,P_element015]
  conduct = 2
  density = 1
  expand = 3
  formula = G4_DNA_A
  name = G4_DNA_A
  specific = 4
FEATURE [App::DocumentObjectGroupPython] H_element135  label="H_element : 082"  # scripted group (container) (typed FeaturePython)
  n = 10
  ref = H_element
FEATURE [App::DocumentObjectGroupPython] C_element145  label="C_element : 090"  # scripted group (container) (typed FeaturePython)
  n = 10
  ref = C_element
FEATURE [App::DocumentObjectGroupPython] N_element065  label="N_element : 037"  # scripted group (container) (typed FeaturePython)
  n = 5
  ref = N_element
FEATURE [App::DocumentObjectGroupPython] O_element127  label="O_element : 8"  # scripted group (container) (typed FeaturePython)
  n = 8
  ref = O_element
FEATURE [App::DocumentObjectGroupPython] P_element016  label="P_element : 005"  # scripted group (container) (typed FeaturePython)
  n = 1
  ref = P_element
FEATURE [App::DocumentObjectGroupPython] G4_DNA_G  # scripted group (container) (typed FeaturePython)
  Dunit = g/cm3
  Dvalue = 1
  Group = -> [H_element135,C_element145,N_element065,O_element127,P_element016]
  conduct = 2
  density = 1
  expand = 3
  formula = G4_DNA_G
  name = G4_DNA_G
  specific = 4
FEATURE [App::DocumentObjectGroupPython] H_element136  label="H_element : 083"  # scripted group (container) (typed FeaturePython)
  n = 10
  ref = H_element
FEATURE [App::DocumentObjectGroupPython] C_element146  label="C_element : 091"  # scripted group (container) (typed FeaturePython)
  n = 9
  ref = C_element
FEATURE [App::DocumentObjectGroupPython] N_element066  label="N_element : 038"  # scripted group (container) (typed FeaturePython)
  n = 3
  ref = N_element
FEATURE [App::DocumentObjectGroupPython] O_element128  label="O_element : 080"  # scripted group (container) (typed FeaturePython)
  n = 8
  ref = O_element
FEATURE [App::DocumentObjectGroupPython] P_element017  label="P_element : 006"  # scripted group (container) (typed FeaturePython)
  n = 1
  ref = P_element
FEATURE [App::DocumentObjectGroupPython] G4_DNA_C  # scripted group (container) (typed FeaturePython)
  Dunit = g/cm3
  Dvalue = 1
  Group = -> [H_element136,C_element146,N_element066,O_element128,P_element017]
  conduct = 2
  density = 1
  expand = 3
  formula = G4_DNA_C
  name = G4_DNA_C
  specific = 4
FEATURE [App::DocumentObjectGroupPython] H_element137  label="H_element : 084"  # scripted group (container) (typed FeaturePython)
  n = 9
  ref = H_element
FEATURE [App::DocumentObjectGroupPython] C_element147  label="C_element : 092"  # scripted group (container) (typed FeaturePython)
  n = 9
  ref = C_element
FEATURE [App::DocumentObjectGroupPython] N_element067  label="N_element : 039"  # scripted group (container) (typed FeaturePython)
  n = 2
  ref = N_element
FEATURE [App::DocumentObjectGroupPython] O_element129  label="O_element : 9"  # scripted group (container) (typed FeaturePython)
  n = 9
  ref = O_element
FEATURE [App::DocumentObjectGroupPython] P_element018  label="P_element : 007"  # scripted group (container) (typed FeaturePython)
  n = 1
  ref = P_element
FEATURE [App::DocumentObjectGroupPython] G4_DNA_U  # scripted group (container) (typed FeaturePython)
  Dunit = g/cm3
  Dvalue = 1
  Group = -> [H_element137,C_element147,N_element067,O_element129,P_element018]
  conduct = 2
  density = 1
  expand = 3
  formula = G4_DNA_U
  name = G4_DNA_U
  specific = 4
FEATURE [App::DocumentObjectGroupPython] H_element138  label="H_element : 085"  # scripted group (container) (typed FeaturePython)
  n = 11
  ref = H_element
FEATURE [App::DocumentObjectGroupPython] C_element148  label="C_element : 093"  # scripted group (container) (typed FeaturePython)
  n = 10
  ref = C_element
FEATURE [App::DocumentObjectGroupPython] N_element068  label="N_element : 040"  # scripted group (container) (typed FeaturePython)
  n = 2
  ref = N_element
FEATURE [App::DocumentObjectGroupPython] O_element130  label="O_element : 081"  # scripted group (container) (typed FeaturePython)
  n = 9
  ref = O_element
FEATURE [App::DocumentObjectGroupPython] P_element019  label="P_element : 008"  # scripted group (container) (typed FeaturePython)
  n = 1
  ref = P_element
FEATURE [App::DocumentObjectGroupPython] G4_DNA_MU  # scripted group (container) (typed FeaturePython)
  Dunit = g/cm3
  Dvalue = 1
  Group = -> [H_element138,C_element148,N_element068,O_element130,P_element019]
  conduct = 2
  density = 1
  expand = 3
  formula = G4_DNA_MU
  name = G4_DNA_MU
  specific = 4
FEATURE [App::DocumentObjectGroupPython] BioChemical  # scripted group (container) (typed FeaturePython)
  Group = -> [G4_CYTOSINE,G4_THYMINE,G4_URACIL,G4_DNA_ADENINE,G4_DNA_GUANINE,G4_DNA_CYTOSINE,G4_DNA_THYMINE,G4_DNA_URACIL,G4_DNA_ADENOSINE,G4_DNA_GUANOSINE,G4_DNA_CYTIDINE,G4_DNA_URIDINE,G4_DNA_METHYLURIDINE,G4_DNA_MONOPHOSPHATE,G4_DNA_A,G4_DNA_G,G4_DNA_C,G4_DNA_U,G4_DNA_MU]
FEATURE [App::DocumentObjectGroupPython] G4Materials  # scripted group (container) (typed FeaturePython)
  Group = -> [NIST,Element,HEP,Space,BioChemical]
  version = 1
FEATURE [App::DocumentObjectGroupPython] Geant4  # scripted group (container) (typed FeaturePython)
  Group = -> [G4Isotopes,G4Elements,G4Materials]
FEATURE [App::DocumentObjectGroupPython] Materials  # scripted group (container) (typed FeaturePython)
  Group = -> [Geant4]
FEATURE [Part::FeaturePython] GDMLBox_WorldBox  # WARN: FeaturePython — macro-defined, semantics opaque (R4)
  lunit = 2
  material = 5
  x = 100
  y = 100
  z = 100
FEATURE [Part::Box] Box  label="Cube"
  AttacherType = Attacher::AttachEngine3D
  Height = 5
  Length = 5
  Placement = pos=(5,0,0) rot=(0,0,1;0rad)
  Width = 5
FEATURE [Part::FeaturePython] Array001  # Draft array (typed FeaturePython)
  Angle = 360
  ArrayType = 0
  Axis = (0,0,1)
  Base = -> Box
  Center = (0,0,0)
  Fuse = false
  IntervalAxis = (0,0,0)
  IntervalX = (50,0,0)
  IntervalY = (0,30,0)
  IntervalZ = (0,0,100)
  NumberCircles = 3
  NumberPolar = 5
  NumberX = 2
  NumberY = 2
  NumberZ = 1
  Placement = pos=(-20,-14,0) rot=(0,0,1;0rad)
  RadialDistance = 50
  Symmetry = 1
  TangentialDistance = 25
FEATURE [App::Part] Part
  Group = -> [Array001]
  Origin = -> Origin002
FEATURE [App::Part] worldVOL
  Group = -> [GDMLBox_WorldBox,Part]
  Origin = -> Origin
